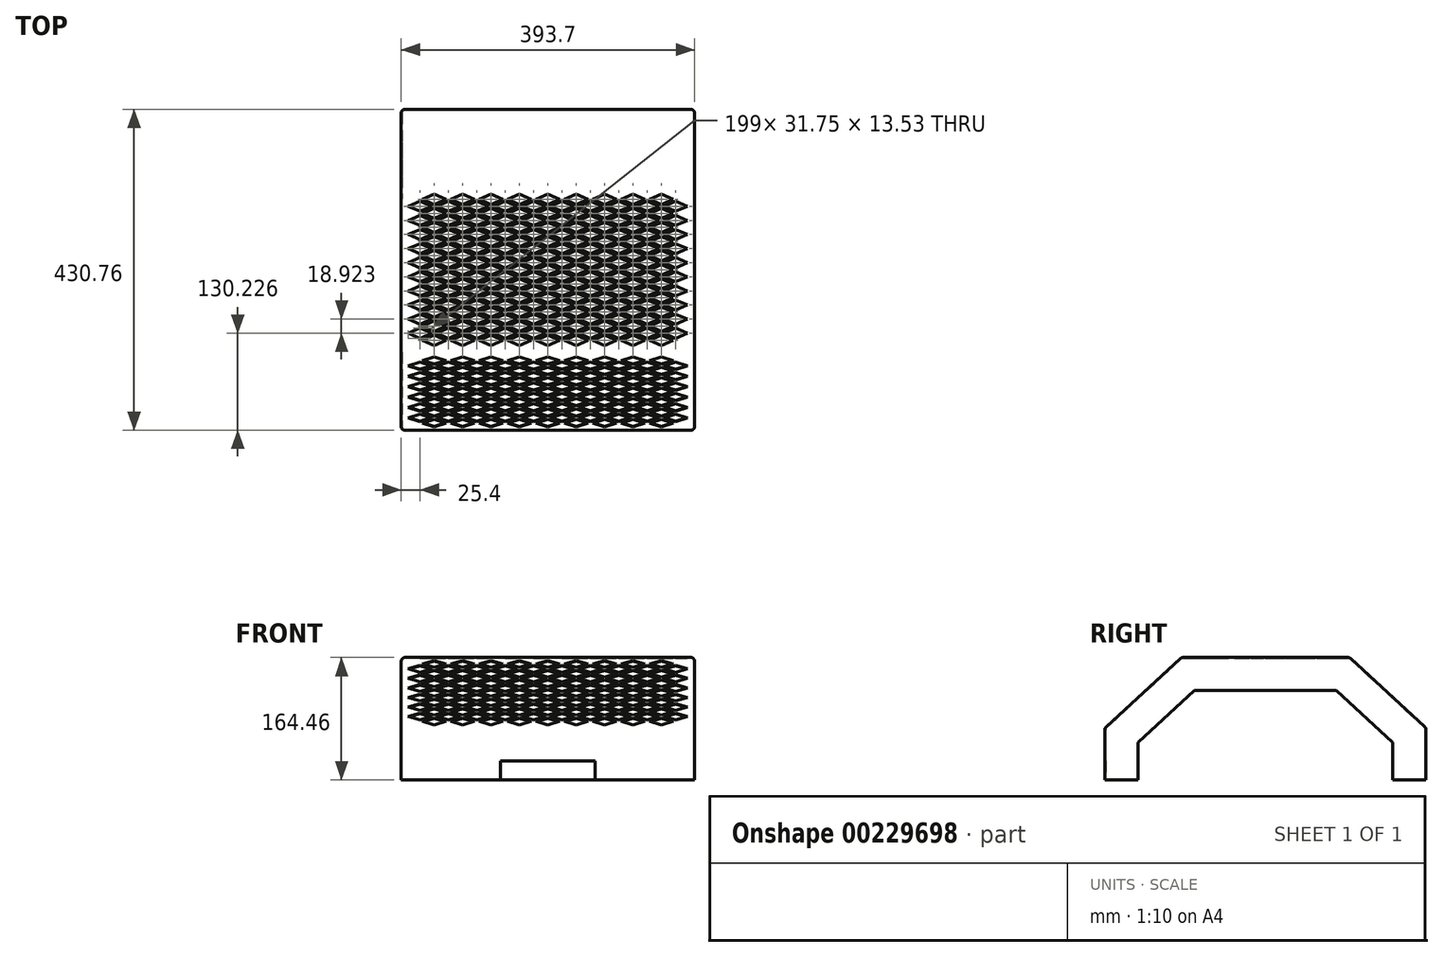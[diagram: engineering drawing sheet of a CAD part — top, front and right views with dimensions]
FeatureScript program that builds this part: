
annotation { "Feature Type Name" : "Feature", "Feature Type Description" : "" }
export const myFeature = defineFeature(function(context is Context, id is Id, definition is map)
    precondition{}
    {
        {
            var Q0;
            Q0=qCreatedBy(makeId("Right.planeOp"),FACE);
            var sketch = newSketch(context, id + "F0", { "sketchPlane" : qUnion([Q0])});
            skLineSegment(sketch, "E0", {"start": v(0, 0) * mm, "end": v(0, 169.27) * mm, "construction": true});
            skLineSegment(sketch, "E1", {"start": v(0, 164.46) * mm, "end": v(112.6, 164.46) * mm});
            skLineSegment(sketch, "E2", {"start": v(112.6, 164.46) * mm, "end": v(215.38, 69.85) * mm});
            skLineSegment(sketch, "E3", {"start": v(215.38, 69.85) * mm, "end": v(215.38, 0) * mm});
            skLineSegment(sketch, "E4", {"start": v(215.38, 0) * mm, "end": v(170.93, 0) * mm});
            skLineSegment(sketch, "E5", {"start": v(170.93, 0) * mm, "end": v(170.93, 50.35) * mm});
            skLineSegment(sketch, "E6", {"start": v(170.93, 50.35) * mm, "end": v(95.25, 120.01) * mm});
            skLineSegment(sketch, "E7", {"start": v(95.25, 120.01) * mm, "end": v(0, 120.01) * mm});
            skLineSegment(sketch, "E8.MirrorCS", {"start": v(0, 164.46) * mm, "end": v(-112.6, 164.46) * mm});
            skLineSegment(sketch, "E9.MirrorCS", {"start": v(-215.38, 0) * mm, "end": v(-170.93, 0) * mm});
            skLineSegment(sketch, "E10.MirrorCS", {"start": v(-170.93, 0) * mm, "end": v(-170.93, 50.35) * mm});
            skLineSegment(sketch, "E11.MirrorCS", {"start": v(-215.38, 69.85) * mm, "end": v(-215.38, 0) * mm});
            skLineSegment(sketch, "E12.MirrorCS", {"start": v(-95.25, 120.01) * mm, "end": v(0, 120.01) * mm});
            skLineSegment(sketch, "E13.MirrorCS", {"start": v(-112.6, 164.46) * mm, "end": v(-215.38, 69.85) * mm});
            skLineSegment(sketch, "E14.MirrorCS", {"start": v(-170.93, 50.35) * mm, "end": v(-95.25, 120.01) * mm});
            skSolve(sketch);
        }
        {
            var Q0;
            Q0 = qSketchRegion(id + "F0", true);
            extrude(context, id + "F1", {"entities" : qUnion([Q0]), "endBound" : BoundingType.SYMMETRIC, "depth" : 393.7 * mm});
        }
        {
            var Q0;
            Q0=makeQuery(id+"F1.opExtrude","CAP_EDGE",EDGE,{"disambiguationData":[OSD([sQuery(id+"F0.wireOp",EDGE,"E1"),sQuery(id+"F0.wireOp",EDGE,"E8.MirrorCS")])],"isStart":true});
            var Q1;
            Q1=makeQuery(id+"F1.opExtrude","CAP_EDGE",EDGE,{"disambiguationData":[OSD([sQuery(id+"F0.wireOp",EDGE,"E1"),sQuery(id+"F0.wireOp",EDGE,"E8.MirrorCS")])],"isStart":false});
            var Q2;
            Q2=makeQuery(id+"F1.opExtrude","CAP_EDGE",EDGE,{"disambiguationData":[OSD([sQuery(id+"F0.wireOp",EDGE,"E13.MirrorCS")])],"isStart":false});
            var Q3;
            Q3=makeQuery(id+"F1.opExtrude","CAP_EDGE",EDGE,{"disambiguationData":[OSD([sQuery(id+"F0.wireOp",EDGE,"E11.MirrorCS")])],"isStart":false});
            var Q4;
            Q4=makeQuery(id+"F1.opExtrude","CAP_EDGE",EDGE,{"disambiguationData":[OSD([sQuery(id+"F0.wireOp",EDGE,"E2")])],"isStart":false});
            var Q5;
            Q5=makeQuery(id+"F1.opExtrude","CAP_EDGE",EDGE,{"disambiguationData":[OSD([sQuery(id+"F0.wireOp",EDGE,"E3")])],"isStart":false});
            var Q6;
            Q6=makeQuery(id+"F1.opExtrude","CAP_EDGE",EDGE,{"disambiguationData":[OSD([sQuery(id+"F0.wireOp",EDGE,"E3")])],"isStart":true});
            var Q7;
            Q7=makeQuery(id+"F1.opExtrude","CAP_EDGE",EDGE,{"disambiguationData":[OSD([sQuery(id+"F0.wireOp",EDGE,"E2")])],"isStart":true});
            var Q8;
            Q8=makeQuery(id+"F1.opExtrude","CAP_EDGE",EDGE,{"disambiguationData":[OSD([sQuery(id+"F0.wireOp",EDGE,"E13.MirrorCS")])],"isStart":true});
            var Q9;
            Q9=makeQuery(id+"F1.opExtrude","CAP_EDGE",EDGE,{"disambiguationData":[OSD([sQuery(id+"F0.wireOp",EDGE,"E11.MirrorCS")])],"isStart":true});
            var Q10;
            Q10=makeQuery(id+"F1.opExtrude","SWEPT_EDGE",EDGE,{"disambiguationData":[OSD([sQuery(id+"F0.wireOp",EDGE,"E11.MirrorCS"),sQuery(id+"F0.wireOp",EDGE,"E13.MirrorCS")])]});
            var Q11;
            Q11=makeQuery(id+"F1.opExtrude","SWEPT_EDGE",EDGE,{"disambiguationData":[OSD([sQuery(id+"F0.wireOp",EDGE,"E8.MirrorCS"),sQuery(id+"F0.wireOp",EDGE,"E13.MirrorCS")])]});
            var Q12;
            Q12=makeQuery(id+"F1.opExtrude","SWEPT_EDGE",EDGE,{"disambiguationData":[OSD([sQuery(id+"F0.wireOp",EDGE,"E1"),sQuery(id+"F0.wireOp",EDGE,"E2")])]});
            var Q13;
            Q13=makeQuery(id+"F1.opExtrude","SWEPT_EDGE",EDGE,{"disambiguationData":[OSD([sQuery(id+"F0.wireOp",EDGE,"E2"),sQuery(id+"F0.wireOp",EDGE,"E3")])]});
            fillet(context, id + "F2", {"entities" : qUnion([Q0, Q1, Q2, Q3, Q4, Q5, Q6, Q7, Q8, Q9, Q10, Q11, Q12, Q13]), "radius" : 5.08 * mm, "tangentPropagation" : true, "allowEdgeOverflow" : false});
        }
        {
            var Q0;
            Q0=makeQuery(id+"F1.opExtrude","SWEPT_FACE",FACE,{"disambiguationData":[OSD([sQuery(id+"F0.wireOp",EDGE,"E7"),sQuery(id+"F0.wireOp",EDGE,"E12.MirrorCS")])]});
            var Q1;
            Q1=makeQuery(id+"F1.opExtrude","SWEPT_FACE",FACE,{"disambiguationData":[OSD([sQuery(id+"F0.wireOp",EDGE,"E6")])]});
            var Q2;
            Q2=makeQuery(id+"F1.opExtrude","SWEPT_FACE",FACE,{"disambiguationData":[OSD([sQuery(id+"F0.wireOp",EDGE,"E5")])]});
            var Q3;
            Q3=makeQuery(id+"F1.opExtrude","SWEPT_FACE",FACE,{"disambiguationData":[OSD([sQuery(id+"F0.wireOp",EDGE,"E4")])]});
            var Q4;
            Q4=makeQuery(id+"F1.opExtrude","SWEPT_FACE",FACE,{"disambiguationData":[OSD([sQuery(id+"F0.wireOp",EDGE,"E14.MirrorCS")])]});
            var Q5;
            Q5=makeQuery(id+"F1.opExtrude","SWEPT_FACE",FACE,{"disambiguationData":[OSD([sQuery(id+"F0.wireOp",EDGE,"E10.MirrorCS")])]});
            var Q6;
            Q6=makeQuery(id+"F1.opExtrude","SWEPT_FACE",FACE,{"disambiguationData":[OSD([sQuery(id+"F0.wireOp",EDGE,"E9.MirrorCS")])]});
            shell(context, id + "F3", {"entities" : qUnion([Q0, Q1, Q2, Q3, Q4, Q5, Q6]), "thickness" : 0.95 * mm});
        }
        {
            var Q0;
            Q0=makeQuery(id+"F1.opExtrude","SWEPT_FACE",FACE,{"disambiguationData":[OSD([sQuery(id+"F0.wireOp",EDGE,"E11.MirrorCS")])]});
            var sketch = newSketch(context, id + "F4", { "sketchPlane" : qUnion([Q0])});
            skLineSegment(sketch, "E15.bottom", {"start": v(-63.5, 0) * mm, "end": v(63.5, 0) * mm});
            skLineSegment(sketch, "E15.top", {"start": v(-63.5, 25.4) * mm, "end": v(63.5, 25.4) * mm});
            skLineSegment(sketch, "E15.left", {"start": v(-63.5, 0) * mm, "end": v(-63.5, 25.4) * mm});
            skLineSegment(sketch, "E15.right", {"start": v(63.5, 0) * mm, "end": v(63.5, 25.4) * mm});
            skSolve(sketch);
        }
        {
            var Q0;
            Q0 = qSketchRegion(id + "F4", true);
            extrude(context, id + "F5", {"entities" : qUnion([Q0]), "operationType" : NewBodyOperationType.REMOVE, "oppositeDirection" : true, "depth" : 25.4 * mm});
        }
        {
            var Q0;
            Q0=makeQuery(id+"F1.opExtrude","SWEPT_FACE",FACE,{"disambiguationData":[OSD([sQuery(id+"F0.wireOp",EDGE,"E1"),sQuery(id+"F0.wireOp",EDGE,"E8.MirrorCS")])]});
            var sketch = newSketch(context, id + "F6", { "sketchPlane" : qUnion([Q0])});
            skLineSegment(sketch, "E16", {"start": v(-15.88, 0) * mm, "end": v(0, 6.76) * mm});
            skLineSegment(sketch, "E17", {"start": v(0, 6.76) * mm, "end": v(15.88, 0) * mm});
            skLineSegment(sketch, "E18", {"start": v(15.88, 0) * mm, "end": v(0, -6.76) * mm});
            skLineSegment(sketch, "E19", {"start": v(0, -6.76) * mm, "end": v(-15.88, 0) * mm});
            skLineSegment(sketch, "E20.0.1.0", {"start": v(-15.88, 18.92) * mm, "end": v(0, 25.69) * mm});
            skLineSegment(sketch, "E20.0.1.1", {"start": v(15.88, 18.92) * mm, "end": v(0, 12.16) * mm});
            skLineSegment(sketch, "E20.0.1.2", {"start": v(0, 12.16) * mm, "end": v(-15.88, 18.92) * mm});
            skLineSegment(sketch, "E20.0.1.3", {"start": v(0, 25.69) * mm, "end": v(15.88, 18.92) * mm});
            skLineSegment(sketch, "E20.0.2.0", {"start": v(-15.88, 37.85) * mm, "end": v(0, 44.6) * mm});
            skLineSegment(sketch, "E20.0.2.1", {"start": v(15.88, 37.85) * mm, "end": v(0, 31.08) * mm});
            skLineSegment(sketch, "E20.0.2.2", {"start": v(0, 31.08) * mm, "end": v(-15.88, 37.85) * mm});
            skLineSegment(sketch, "E20.0.2.3", {"start": v(0, 44.6) * mm, "end": v(15.88, 37.85) * mm});
            skLineSegment(sketch, "E20.0.3.0", {"start": v(-15.88, 56.77) * mm, "end": v(0, 63.53) * mm});
            skLineSegment(sketch, "E20.0.3.1", {"start": v(15.88, 56.77) * mm, "end": v(0, 50) * mm});
            skLineSegment(sketch, "E20.0.3.2", {"start": v(0, 50) * mm, "end": v(-15.88, 56.77) * mm});
            skLineSegment(sketch, "E20.0.3.3", {"start": v(0, 63.53) * mm, "end": v(15.88, 56.77) * mm});
            skLineSegment(sketch, "E20.0.4.0", {"start": v(-15.88, 75.7) * mm, "end": v(0, 82.45) * mm});
            skLineSegment(sketch, "E20.0.4.1", {"start": v(15.88, 75.7) * mm, "end": v(0, 68.93) * mm});
            skLineSegment(sketch, "E20.0.4.2", {"start": v(0, 68.93) * mm, "end": v(-15.88, 75.7) * mm});
            skLineSegment(sketch, "E20.0.4.3", {"start": v(0, 82.45) * mm, "end": v(15.88, 75.7) * mm});
            skLineSegment(sketch, "E20.0.5.0", {"start": v(-15.88, 94.62) * mm, "end": v(0, 101.38) * mm});
            skLineSegment(sketch, "E20.0.5.1", {"start": v(15.88, 94.62) * mm, "end": v(0, 87.85) * mm});
            skLineSegment(sketch, "E20.0.5.2", {"start": v(0, 87.85) * mm, "end": v(-15.88, 94.62) * mm});
            skLineSegment(sketch, "E20.0.5.3", {"start": v(0, 101.38) * mm, "end": v(15.88, 94.62) * mm});
            skLineSegment(sketch, "E20.1.0.0", {"start": v(22.23, 0) * mm, "end": v(38.1, 6.76) * mm});
            skLineSegment(sketch, "E20.1.0.1", {"start": v(53.98, 0) * mm, "end": v(38.1, -6.76) * mm});
            skLineSegment(sketch, "E20.1.0.2", {"start": v(38.1, -6.76) * mm, "end": v(22.22, 0) * mm});
            skLineSegment(sketch, "E20.1.0.3", {"start": v(38.1, 6.76) * mm, "end": v(53.98, 0) * mm});
            skLineSegment(sketch, "E20.1.1.0", {"start": v(22.23, 18.92) * mm, "end": v(38.1, 25.69) * mm});
            skLineSegment(sketch, "E20.1.1.1", {"start": v(53.98, 18.92) * mm, "end": v(38.1, 12.16) * mm});
            skLineSegment(sketch, "E20.1.1.2", {"start": v(38.1, 12.16) * mm, "end": v(22.22, 18.92) * mm});
            skLineSegment(sketch, "E20.1.1.3", {"start": v(38.1, 25.69) * mm, "end": v(53.98, 18.92) * mm});
            skLineSegment(sketch, "E20.1.2.0", {"start": v(22.23, 37.85) * mm, "end": v(38.1, 44.6) * mm});
            skLineSegment(sketch, "E20.1.2.1", {"start": v(53.98, 37.85) * mm, "end": v(38.1, 31.08) * mm});
            skLineSegment(sketch, "E20.1.2.2", {"start": v(38.1, 31.08) * mm, "end": v(22.22, 37.85) * mm});
            skLineSegment(sketch, "E20.1.2.3", {"start": v(38.1, 44.6) * mm, "end": v(53.98, 37.85) * mm});
            skLineSegment(sketch, "E20.1.3.0", {"start": v(22.23, 56.77) * mm, "end": v(38.1, 63.53) * mm});
            skLineSegment(sketch, "E20.1.3.1", {"start": v(53.98, 56.77) * mm, "end": v(38.1, 50) * mm});
            skLineSegment(sketch, "E20.1.3.2", {"start": v(38.1, 50) * mm, "end": v(22.22, 56.77) * mm});
            skLineSegment(sketch, "E20.1.3.3", {"start": v(38.1, 63.53) * mm, "end": v(53.98, 56.77) * mm});
            skLineSegment(sketch, "E20.1.4.0", {"start": v(22.23, 75.7) * mm, "end": v(38.1, 82.45) * mm});
            skLineSegment(sketch, "E20.1.4.1", {"start": v(53.98, 75.7) * mm, "end": v(38.1, 68.93) * mm});
            skLineSegment(sketch, "E20.1.4.2", {"start": v(38.1, 68.93) * mm, "end": v(22.22, 75.7) * mm});
            skLineSegment(sketch, "E20.1.4.3", {"start": v(38.1, 82.45) * mm, "end": v(53.98, 75.7) * mm});
            skLineSegment(sketch, "E20.1.5.0", {"start": v(22.23, 94.62) * mm, "end": v(38.1, 101.38) * mm});
            skLineSegment(sketch, "E20.1.5.1", {"start": v(53.98, 94.62) * mm, "end": v(38.1, 87.85) * mm});
            skLineSegment(sketch, "E20.1.5.2", {"start": v(38.1, 87.85) * mm, "end": v(22.22, 94.62) * mm});
            skLineSegment(sketch, "E20.1.5.3", {"start": v(38.1, 101.38) * mm, "end": v(53.98, 94.62) * mm});
            skLineSegment(sketch, "E20.2.0.0", {"start": v(60.33, 0) * mm, "end": v(76.2, 6.76) * mm});
            skLineSegment(sketch, "E20.2.0.1", {"start": v(92.08, 0) * mm, "end": v(76.2, -6.76) * mm});
            skLineSegment(sketch, "E20.2.0.2", {"start": v(76.2, -6.76) * mm, "end": v(60.33, 0) * mm});
            skLineSegment(sketch, "E20.2.0.3", {"start": v(76.2, 6.76) * mm, "end": v(92.08, 0) * mm});
            skLineSegment(sketch, "E20.2.1.0", {"start": v(60.33, 18.92) * mm, "end": v(76.2, 25.69) * mm});
            skLineSegment(sketch, "E20.2.1.1", {"start": v(92.08, 18.92) * mm, "end": v(76.2, 12.16) * mm});
            skLineSegment(sketch, "E20.2.1.2", {"start": v(76.2, 12.16) * mm, "end": v(60.33, 18.92) * mm});
            skLineSegment(sketch, "E20.2.1.3", {"start": v(76.2, 25.69) * mm, "end": v(92.08, 18.92) * mm});
            skLineSegment(sketch, "E20.2.2.0", {"start": v(60.33, 37.85) * mm, "end": v(76.2, 44.6) * mm});
            skLineSegment(sketch, "E20.2.2.1", {"start": v(92.08, 37.85) * mm, "end": v(76.2, 31.08) * mm});
            skLineSegment(sketch, "E20.2.2.2", {"start": v(76.2, 31.08) * mm, "end": v(60.33, 37.85) * mm});
            skLineSegment(sketch, "E20.2.2.3", {"start": v(76.2, 44.6) * mm, "end": v(92.08, 37.85) * mm});
            skLineSegment(sketch, "E20.2.3.0", {"start": v(60.33, 56.77) * mm, "end": v(76.2, 63.53) * mm});
            skLineSegment(sketch, "E20.2.3.1", {"start": v(92.08, 56.77) * mm, "end": v(76.2, 50) * mm});
            skLineSegment(sketch, "E20.2.3.2", {"start": v(76.2, 50) * mm, "end": v(60.33, 56.77) * mm});
            skLineSegment(sketch, "E20.2.3.3", {"start": v(76.2, 63.53) * mm, "end": v(92.08, 56.77) * mm});
            skLineSegment(sketch, "E20.2.4.0", {"start": v(60.33, 75.7) * mm, "end": v(76.2, 82.45) * mm});
            skLineSegment(sketch, "E20.2.4.1", {"start": v(92.08, 75.7) * mm, "end": v(76.2, 68.93) * mm});
            skLineSegment(sketch, "E20.2.4.2", {"start": v(76.2, 68.93) * mm, "end": v(60.33, 75.7) * mm});
            skLineSegment(sketch, "E20.2.4.3", {"start": v(76.2, 82.45) * mm, "end": v(92.08, 75.7) * mm});
            skLineSegment(sketch, "E20.2.5.0", {"start": v(60.33, 94.62) * mm, "end": v(76.2, 101.38) * mm});
            skLineSegment(sketch, "E20.2.5.1", {"start": v(92.08, 94.62) * mm, "end": v(76.2, 87.85) * mm});
            skLineSegment(sketch, "E20.2.5.2", {"start": v(76.2, 87.85) * mm, "end": v(60.33, 94.62) * mm});
            skLineSegment(sketch, "E20.2.5.3", {"start": v(76.2, 101.38) * mm, "end": v(92.08, 94.62) * mm});
            skLineSegment(sketch, "E20.3.0.0", {"start": v(98.43, 0) * mm, "end": v(114.3, 6.76) * mm});
            skLineSegment(sketch, "E20.3.0.1", {"start": v(130.18, 0) * mm, "end": v(114.3, -6.76) * mm});
            skLineSegment(sketch, "E20.3.0.2", {"start": v(114.3, -6.76) * mm, "end": v(98.43, 0) * mm});
            skLineSegment(sketch, "E20.3.0.3", {"start": v(114.3, 6.76) * mm, "end": v(130.18, 0) * mm});
            skLineSegment(sketch, "E20.3.1.0", {"start": v(98.43, 18.92) * mm, "end": v(114.3, 25.69) * mm});
            skLineSegment(sketch, "E20.3.1.1", {"start": v(130.18, 18.92) * mm, "end": v(114.3, 12.16) * mm});
            skLineSegment(sketch, "E20.3.1.2", {"start": v(114.3, 12.16) * mm, "end": v(98.43, 18.92) * mm});
            skLineSegment(sketch, "E20.3.1.3", {"start": v(114.3, 25.69) * mm, "end": v(130.18, 18.92) * mm});
            skLineSegment(sketch, "E20.3.2.0", {"start": v(98.43, 37.85) * mm, "end": v(114.3, 44.6) * mm});
            skLineSegment(sketch, "E20.3.2.1", {"start": v(130.18, 37.85) * mm, "end": v(114.3, 31.08) * mm});
            skLineSegment(sketch, "E20.3.2.2", {"start": v(114.3, 31.08) * mm, "end": v(98.43, 37.85) * mm});
            skLineSegment(sketch, "E20.3.2.3", {"start": v(114.3, 44.6) * mm, "end": v(130.18, 37.85) * mm});
            skLineSegment(sketch, "E20.3.3.0", {"start": v(98.43, 56.77) * mm, "end": v(114.3, 63.53) * mm});
            skLineSegment(sketch, "E20.3.3.1", {"start": v(130.18, 56.77) * mm, "end": v(114.3, 50) * mm});
            skLineSegment(sketch, "E20.3.3.2", {"start": v(114.3, 50) * mm, "end": v(98.43, 56.77) * mm});
            skLineSegment(sketch, "E20.3.3.3", {"start": v(114.3, 63.53) * mm, "end": v(130.18, 56.77) * mm});
            skLineSegment(sketch, "E20.3.4.0", {"start": v(98.43, 75.7) * mm, "end": v(114.3, 82.45) * mm});
            skLineSegment(sketch, "E20.3.4.1", {"start": v(130.18, 75.7) * mm, "end": v(114.3, 68.93) * mm});
            skLineSegment(sketch, "E20.3.4.2", {"start": v(114.3, 68.93) * mm, "end": v(98.43, 75.7) * mm});
            skLineSegment(sketch, "E20.3.4.3", {"start": v(114.3, 82.45) * mm, "end": v(130.18, 75.7) * mm});
            skLineSegment(sketch, "E20.3.5.0", {"start": v(98.43, 94.62) * mm, "end": v(114.3, 101.38) * mm});
            skLineSegment(sketch, "E20.3.5.1", {"start": v(130.18, 94.62) * mm, "end": v(114.3, 87.85) * mm});
            skLineSegment(sketch, "E20.3.5.2", {"start": v(114.3, 87.85) * mm, "end": v(98.43, 94.62) * mm});
            skLineSegment(sketch, "E20.3.5.3", {"start": v(114.3, 101.38) * mm, "end": v(130.18, 94.62) * mm});
            skLineSegment(sketch, "E20.4.0.0", {"start": v(136.53, 0) * mm, "end": v(152.4, 6.76) * mm});
            skLineSegment(sketch, "E20.4.0.1", {"start": v(168.28, 0) * mm, "end": v(152.4, -6.76) * mm});
            skLineSegment(sketch, "E20.4.0.2", {"start": v(152.4, -6.76) * mm, "end": v(136.53, 0) * mm});
            skLineSegment(sketch, "E20.4.0.3", {"start": v(152.4, 6.76) * mm, "end": v(168.28, 0) * mm});
            skLineSegment(sketch, "E20.4.1.0", {"start": v(136.53, 18.92) * mm, "end": v(152.4, 25.69) * mm});
            skLineSegment(sketch, "E20.4.1.1", {"start": v(168.28, 18.92) * mm, "end": v(152.4, 12.16) * mm});
            skLineSegment(sketch, "E20.4.1.2", {"start": v(152.4, 12.16) * mm, "end": v(136.53, 18.92) * mm});
            skLineSegment(sketch, "E20.4.1.3", {"start": v(152.4, 25.69) * mm, "end": v(168.28, 18.92) * mm});
            skLineSegment(sketch, "E20.4.2.0", {"start": v(136.53, 37.85) * mm, "end": v(152.4, 44.6) * mm});
            skLineSegment(sketch, "E20.4.2.1", {"start": v(168.28, 37.85) * mm, "end": v(152.4, 31.08) * mm});
            skLineSegment(sketch, "E20.4.2.2", {"start": v(152.4, 31.08) * mm, "end": v(136.53, 37.85) * mm});
            skLineSegment(sketch, "E20.4.2.3", {"start": v(152.4, 44.6) * mm, "end": v(168.28, 37.85) * mm});
            skLineSegment(sketch, "E20.4.3.0", {"start": v(136.53, 56.77) * mm, "end": v(152.4, 63.53) * mm});
            skLineSegment(sketch, "E20.4.3.1", {"start": v(168.28, 56.77) * mm, "end": v(152.4, 50) * mm});
            skLineSegment(sketch, "E20.4.3.2", {"start": v(152.4, 50) * mm, "end": v(136.53, 56.77) * mm});
            skLineSegment(sketch, "E20.4.3.3", {"start": v(152.4, 63.53) * mm, "end": v(168.28, 56.77) * mm});
            skLineSegment(sketch, "E20.4.4.0", {"start": v(136.53, 75.7) * mm, "end": v(152.4, 82.45) * mm});
            skLineSegment(sketch, "E20.4.4.1", {"start": v(168.28, 75.7) * mm, "end": v(152.4, 68.93) * mm});
            skLineSegment(sketch, "E20.4.4.2", {"start": v(152.4, 68.93) * mm, "end": v(136.53, 75.7) * mm});
            skLineSegment(sketch, "E20.4.4.3", {"start": v(152.4, 82.45) * mm, "end": v(168.28, 75.7) * mm});
            skLineSegment(sketch, "E20.4.5.0", {"start": v(136.53, 94.62) * mm, "end": v(152.4, 101.38) * mm});
            skLineSegment(sketch, "E20.4.5.1", {"start": v(168.28, 94.62) * mm, "end": v(152.4, 87.85) * mm});
            skLineSegment(sketch, "E20.4.5.2", {"start": v(152.4, 87.85) * mm, "end": v(136.53, 94.62) * mm});
            skLineSegment(sketch, "E20.4.5.3", {"start": v(152.4, 101.38) * mm, "end": v(168.28, 94.62) * mm});
            skLineSegment(sketch, "E20.direction1", {"start": v(-15.88, 0) * mm, "end": v(22.22, 0) * mm, "construction": true});
            skLineSegment(sketch, "E20.direction2", {"start": v(-15.88, 0) * mm, "end": v(-15.88, 18.92) * mm, "construction": true});
            skLineSegment(sketch, "E21.0.1.0", {"start": v(0, -25.69) * mm, "end": v(-15.88, -18.92) * mm});
            skLineSegment(sketch, "E21.0.1.1", {"start": v(15.88, -18.92) * mm, "end": v(0, -25.69) * mm});
            skLineSegment(sketch, "E21.0.1.2", {"start": v(0, -12.16) * mm, "end": v(15.88, -18.92) * mm});
            skLineSegment(sketch, "E21.0.1.3", {"start": v(-15.88, -18.92) * mm, "end": v(0, -12.16) * mm});
            skLineSegment(sketch, "E21.0.1.4", {"start": v(114.3, -12.16) * mm, "end": v(130.18, -18.92) * mm});
            skLineSegment(sketch, "E21.0.1.5", {"start": v(38.1, -12.16) * mm, "end": v(53.98, -18.92) * mm});
            skLineSegment(sketch, "E21.0.1.6", {"start": v(152.4, -12.16) * mm, "end": v(168.28, -18.92) * mm});
            skLineSegment(sketch, "E21.0.1.7", {"start": v(76.2, -12.16) * mm, "end": v(92.08, -18.92) * mm});
            skLineSegment(sketch, "E21.0.1.8", {"start": v(114.3, -25.69) * mm, "end": v(98.43, -18.92) * mm});
            skLineSegment(sketch, "E21.0.1.9", {"start": v(38.1, -25.69) * mm, "end": v(22.22, -18.92) * mm});
            skLineSegment(sketch, "E21.0.1.10", {"start": v(76.2, -25.69) * mm, "end": v(60.33, -18.92) * mm});
            skLineSegment(sketch, "E21.0.1.11", {"start": v(130.18, -18.92) * mm, "end": v(114.3, -25.69) * mm});
            skLineSegment(sketch, "E21.0.1.12", {"start": v(53.98, -18.92) * mm, "end": v(38.1, -25.69) * mm});
            skLineSegment(sketch, "E21.0.1.13", {"start": v(152.4, -25.69) * mm, "end": v(136.53, -18.92) * mm});
            skLineSegment(sketch, "E21.0.1.14", {"start": v(98.43, -18.92) * mm, "end": v(114.3, -12.16) * mm});
            skLineSegment(sketch, "E21.0.1.15", {"start": v(-15.88, -18.92) * mm, "end": v(22.22, -18.92) * mm, "construction": true});
            skLineSegment(sketch, "E21.0.1.16", {"start": v(22.23, -18.92) * mm, "end": v(38.1, -12.16) * mm});
            skLineSegment(sketch, "E21.0.1.17", {"start": v(168.28, -18.92) * mm, "end": v(152.4, -25.69) * mm});
            skLineSegment(sketch, "E21.0.1.18", {"start": v(92.08, -18.92) * mm, "end": v(76.2, -25.69) * mm});
            skLineSegment(sketch, "E21.0.1.19", {"start": v(136.53, -18.92) * mm, "end": v(152.4, -12.16) * mm});
            skLineSegment(sketch, "E21.0.1.20", {"start": v(60.33, -18.92) * mm, "end": v(76.2, -12.16) * mm});
            skLineSegment(sketch, "E21.0.2.0", {"start": v(0, -44.6) * mm, "end": v(-15.88, -37.85) * mm});
            skLineSegment(sketch, "E21.0.2.1", {"start": v(15.88, -37.85) * mm, "end": v(0, -44.6) * mm});
            skLineSegment(sketch, "E21.0.2.2", {"start": v(0, -31.08) * mm, "end": v(15.88, -37.85) * mm});
            skLineSegment(sketch, "E21.0.2.3", {"start": v(-15.88, -37.85) * mm, "end": v(0, -31.08) * mm});
            skLineSegment(sketch, "E21.0.2.4", {"start": v(114.3, -31.08) * mm, "end": v(130.18, -37.85) * mm});
            skLineSegment(sketch, "E21.0.2.5", {"start": v(38.1, -31.08) * mm, "end": v(53.98, -37.85) * mm});
            skLineSegment(sketch, "E21.0.2.6", {"start": v(152.4, -31.08) * mm, "end": v(168.28, -37.85) * mm});
            skLineSegment(sketch, "E21.0.2.7", {"start": v(76.2, -31.08) * mm, "end": v(92.08, -37.85) * mm});
            skLineSegment(sketch, "E21.0.2.8", {"start": v(114.3, -44.6) * mm, "end": v(98.43, -37.85) * mm});
            skLineSegment(sketch, "E21.0.2.9", {"start": v(38.1, -44.6) * mm, "end": v(22.22, -37.85) * mm});
            skLineSegment(sketch, "E21.0.2.10", {"start": v(76.2, -44.6) * mm, "end": v(60.33, -37.85) * mm});
            skLineSegment(sketch, "E21.0.2.11", {"start": v(130.18, -37.85) * mm, "end": v(114.3, -44.6) * mm});
            skLineSegment(sketch, "E21.0.2.12", {"start": v(53.98, -37.85) * mm, "end": v(38.1, -44.6) * mm});
            skLineSegment(sketch, "E21.0.2.13", {"start": v(152.4, -44.6) * mm, "end": v(136.53, -37.85) * mm});
            skLineSegment(sketch, "E21.0.2.14", {"start": v(98.43, -37.85) * mm, "end": v(114.3, -31.08) * mm});
            skLineSegment(sketch, "E21.0.2.15", {"start": v(-15.88, -37.85) * mm, "end": v(22.22, -37.85) * mm, "construction": true});
            skLineSegment(sketch, "E21.0.2.16", {"start": v(22.23, -37.85) * mm, "end": v(38.1, -31.08) * mm});
            skLineSegment(sketch, "E21.0.2.17", {"start": v(168.28, -37.85) * mm, "end": v(152.4, -44.6) * mm});
            skLineSegment(sketch, "E21.0.2.18", {"start": v(92.08, -37.85) * mm, "end": v(76.2, -44.6) * mm});
            skLineSegment(sketch, "E21.0.2.19", {"start": v(136.53, -37.85) * mm, "end": v(152.4, -31.08) * mm});
            skLineSegment(sketch, "E21.0.2.20", {"start": v(60.33, -37.85) * mm, "end": v(76.2, -31.08) * mm});
            skLineSegment(sketch, "E21.0.3.0", {"start": v(0, -63.53) * mm, "end": v(-15.88, -56.77) * mm});
            skLineSegment(sketch, "E21.0.3.1", {"start": v(15.88, -56.77) * mm, "end": v(0, -63.53) * mm});
            skLineSegment(sketch, "E21.0.3.2", {"start": v(0, -50) * mm, "end": v(15.88, -56.77) * mm});
            skLineSegment(sketch, "E21.0.3.3", {"start": v(-15.88, -56.77) * mm, "end": v(0, -50) * mm});
            skLineSegment(sketch, "E21.0.3.4", {"start": v(114.3, -50) * mm, "end": v(130.18, -56.77) * mm});
            skLineSegment(sketch, "E21.0.3.5", {"start": v(38.1, -50) * mm, "end": v(53.98, -56.77) * mm});
            skLineSegment(sketch, "E21.0.3.6", {"start": v(152.4, -50) * mm, "end": v(168.28, -56.77) * mm});
            skLineSegment(sketch, "E21.0.3.7", {"start": v(76.2, -50) * mm, "end": v(92.08, -56.77) * mm});
            skLineSegment(sketch, "E21.0.3.8", {"start": v(114.3, -63.53) * mm, "end": v(98.43, -56.77) * mm});
            skLineSegment(sketch, "E21.0.3.9", {"start": v(38.1, -63.53) * mm, "end": v(22.22, -56.77) * mm});
            skLineSegment(sketch, "E21.0.3.10", {"start": v(76.2, -63.53) * mm, "end": v(60.33, -56.77) * mm});
            skLineSegment(sketch, "E21.0.3.11", {"start": v(130.18, -56.77) * mm, "end": v(114.3, -63.53) * mm});
            skLineSegment(sketch, "E21.0.3.12", {"start": v(53.98, -56.77) * mm, "end": v(38.1, -63.53) * mm});
            skLineSegment(sketch, "E21.0.3.13", {"start": v(152.4, -63.53) * mm, "end": v(136.53, -56.77) * mm});
            skLineSegment(sketch, "E21.0.3.14", {"start": v(98.43, -56.77) * mm, "end": v(114.3, -50) * mm});
            skLineSegment(sketch, "E21.0.3.15", {"start": v(-15.88, -56.77) * mm, "end": v(22.22, -56.77) * mm, "construction": true});
            skLineSegment(sketch, "E21.0.3.16", {"start": v(22.23, -56.77) * mm, "end": v(38.1, -50) * mm});
            skLineSegment(sketch, "E21.0.3.17", {"start": v(168.28, -56.77) * mm, "end": v(152.4, -63.53) * mm});
            skLineSegment(sketch, "E21.0.3.18", {"start": v(92.08, -56.77) * mm, "end": v(76.2, -63.53) * mm});
            skLineSegment(sketch, "E21.0.3.19", {"start": v(136.53, -56.77) * mm, "end": v(152.4, -50) * mm});
            skLineSegment(sketch, "E21.0.3.20", {"start": v(60.33, -56.77) * mm, "end": v(76.2, -50) * mm});
            skLineSegment(sketch, "E21.0.4.0", {"start": v(0, -82.45) * mm, "end": v(-15.88, -75.7) * mm});
            skLineSegment(sketch, "E21.0.4.1", {"start": v(15.88, -75.7) * mm, "end": v(0, -82.45) * mm});
            skLineSegment(sketch, "E21.0.4.2", {"start": v(0, -68.93) * mm, "end": v(15.88, -75.7) * mm});
            skLineSegment(sketch, "E21.0.4.3", {"start": v(-15.88, -75.7) * mm, "end": v(0, -68.93) * mm});
            skLineSegment(sketch, "E21.0.4.4", {"start": v(114.3, -68.93) * mm, "end": v(130.18, -75.7) * mm});
            skLineSegment(sketch, "E21.0.4.5", {"start": v(38.1, -68.93) * mm, "end": v(53.98, -75.7) * mm});
            skLineSegment(sketch, "E21.0.4.6", {"start": v(152.4, -68.93) * mm, "end": v(168.28, -75.7) * mm});
            skLineSegment(sketch, "E21.0.4.7", {"start": v(76.2, -68.93) * mm, "end": v(92.08, -75.7) * mm});
            skLineSegment(sketch, "E21.0.4.8", {"start": v(114.3, -82.45) * mm, "end": v(98.43, -75.7) * mm});
            skLineSegment(sketch, "E21.0.4.9", {"start": v(38.1, -82.45) * mm, "end": v(22.22, -75.7) * mm});
            skLineSegment(sketch, "E21.0.4.10", {"start": v(76.2, -82.45) * mm, "end": v(60.33, -75.7) * mm});
            skLineSegment(sketch, "E21.0.4.11", {"start": v(130.18, -75.7) * mm, "end": v(114.3, -82.45) * mm});
            skLineSegment(sketch, "E21.0.4.12", {"start": v(53.98, -75.7) * mm, "end": v(38.1, -82.45) * mm});
            skLineSegment(sketch, "E21.0.4.13", {"start": v(152.4, -82.45) * mm, "end": v(136.53, -75.7) * mm});
            skLineSegment(sketch, "E21.0.4.14", {"start": v(98.43, -75.7) * mm, "end": v(114.3, -68.93) * mm});
            skLineSegment(sketch, "E21.0.4.15", {"start": v(-15.88, -75.7) * mm, "end": v(22.22, -75.7) * mm, "construction": true});
            skLineSegment(sketch, "E21.0.4.16", {"start": v(22.23, -75.7) * mm, "end": v(38.1, -68.93) * mm});
            skLineSegment(sketch, "E21.0.4.17", {"start": v(168.28, -75.7) * mm, "end": v(152.4, -82.45) * mm});
            skLineSegment(sketch, "E21.0.4.18", {"start": v(92.08, -75.7) * mm, "end": v(76.2, -82.45) * mm});
            skLineSegment(sketch, "E21.0.4.19", {"start": v(136.53, -75.7) * mm, "end": v(152.4, -68.93) * mm});
            skLineSegment(sketch, "E21.0.4.20", {"start": v(60.33, -75.7) * mm, "end": v(76.2, -68.93) * mm});
            skLineSegment(sketch, "E21.0.5.0", {"start": v(0, -101.38) * mm, "end": v(-15.88, -94.61) * mm});
            skLineSegment(sketch, "E21.0.5.1", {"start": v(15.88, -94.62) * mm, "end": v(0, -101.38) * mm});
            skLineSegment(sketch, "E21.0.5.2", {"start": v(0, -87.85) * mm, "end": v(15.88, -94.62) * mm});
            skLineSegment(sketch, "E21.0.5.3", {"start": v(-15.88, -94.62) * mm, "end": v(0, -87.85) * mm});
            skLineSegment(sketch, "E21.0.5.4", {"start": v(114.3, -87.85) * mm, "end": v(130.18, -94.62) * mm});
            skLineSegment(sketch, "E21.0.5.5", {"start": v(38.1, -87.85) * mm, "end": v(53.98, -94.62) * mm});
            skLineSegment(sketch, "E21.0.5.6", {"start": v(152.4, -87.85) * mm, "end": v(168.28, -94.62) * mm});
            skLineSegment(sketch, "E21.0.5.7", {"start": v(76.2, -87.85) * mm, "end": v(92.08, -94.62) * mm});
            skLineSegment(sketch, "E21.0.5.8", {"start": v(114.3, -101.38) * mm, "end": v(98.43, -94.61) * mm});
            skLineSegment(sketch, "E21.0.5.9", {"start": v(38.1, -101.38) * mm, "end": v(22.22, -94.61) * mm});
            skLineSegment(sketch, "E21.0.5.10", {"start": v(76.2, -101.38) * mm, "end": v(60.33, -94.61) * mm});
            skLineSegment(sketch, "E21.0.5.11", {"start": v(130.18, -94.62) * mm, "end": v(114.3, -101.38) * mm});
            skLineSegment(sketch, "E21.0.5.12", {"start": v(53.98, -94.62) * mm, "end": v(38.1, -101.38) * mm});
            skLineSegment(sketch, "E21.0.5.13", {"start": v(152.4, -101.38) * mm, "end": v(136.53, -94.61) * mm});
            skLineSegment(sketch, "E21.0.5.14", {"start": v(98.43, -94.62) * mm, "end": v(114.3, -87.85) * mm});
            skLineSegment(sketch, "E21.0.5.15", {"start": v(-15.88, -94.62) * mm, "end": v(22.22, -94.62) * mm, "construction": true});
            skLineSegment(sketch, "E21.0.5.16", {"start": v(22.23, -94.62) * mm, "end": v(38.1, -87.85) * mm});
            skLineSegment(sketch, "E21.0.5.17", {"start": v(168.28, -94.62) * mm, "end": v(152.4, -101.38) * mm});
            skLineSegment(sketch, "E21.0.5.18", {"start": v(92.08, -94.62) * mm, "end": v(76.2, -101.38) * mm});
            skLineSegment(sketch, "E21.0.5.19", {"start": v(136.53, -94.62) * mm, "end": v(152.4, -87.85) * mm});
            skLineSegment(sketch, "E21.0.5.20", {"start": v(60.33, -94.62) * mm, "end": v(76.2, -87.85) * mm});
            skLineSegment(sketch, "E21.direction1", {"start": v(-15.88, 0) * mm, "end": v(9.52, 0) * mm, "construction": true});
            skLineSegment(sketch, "E21.direction2", {"start": v(-15.88, 0) * mm, "end": v(-15.88, -18.92) * mm, "construction": true});
            skLineSegment(sketch, "E22.1.0.0", {"start": v(-38.1, -50) * mm, "end": v(-22.23, -56.77) * mm});
            skLineSegment(sketch, "E22.1.0.1", {"start": v(-38.1, 87.85) * mm, "end": v(-53.98, 94.62) * mm});
            skLineSegment(sketch, "E22.1.0.2", {"start": v(-53.98, 56.77) * mm, "end": v(-38.1, 63.53) * mm});
            skLineSegment(sketch, "E22.1.0.3", {"start": v(-38.1, 44.6) * mm, "end": v(-22.23, 37.85) * mm});
            skLineSegment(sketch, "E22.1.0.4", {"start": v(-38.1, 31.08) * mm, "end": v(-53.98, 37.85) * mm});
            skLineSegment(sketch, "E22.1.0.5", {"start": v(-22.23, 37.85) * mm, "end": v(-38.1, 31.08) * mm});
            skLineSegment(sketch, "E22.1.0.6", {"start": v(-53.98, 37.85) * mm, "end": v(-38.1, 44.6) * mm});
            skLineSegment(sketch, "E22.1.0.7", {"start": v(-38.1, 25.69) * mm, "end": v(-22.23, 18.92) * mm});
            skLineSegment(sketch, "E22.1.0.8", {"start": v(-38.1, 12.16) * mm, "end": v(-53.98, 18.92) * mm});
            skLineSegment(sketch, "E22.1.0.9", {"start": v(-22.23, 18.92) * mm, "end": v(-38.1, 12.16) * mm});
            skLineSegment(sketch, "E22.1.0.10", {"start": v(-53.98, 18.92) * mm, "end": v(-38.1, 25.69) * mm});
            skLineSegment(sketch, "E22.1.0.11", {"start": v(-38.1, -6.76) * mm, "end": v(-53.98, 0) * mm});
            skLineSegment(sketch, "E22.1.0.12", {"start": v(-22.23, 0) * mm, "end": v(-38.1, -6.76) * mm});
            skLineSegment(sketch, "E22.1.0.13", {"start": v(-38.1, 6.76) * mm, "end": v(-22.23, 0) * mm});
            skLineSegment(sketch, "E22.1.0.14", {"start": v(-53.98, 0) * mm, "end": v(-38.1, 6.76) * mm});
            skLineSegment(sketch, "E22.1.0.15", {"start": v(-22.23, -56.77) * mm, "end": v(-38.1, -63.53) * mm});
            skLineSegment(sketch, "E22.1.0.16", {"start": v(-38.1, 63.53) * mm, "end": v(-22.23, 56.77) * mm});
            skLineSegment(sketch, "E22.1.0.17", {"start": v(-38.1, 50) * mm, "end": v(-53.98, 56.77) * mm});
            skLineSegment(sketch, "E22.1.0.18", {"start": v(-22.23, 56.77) * mm, "end": v(-38.1, 50) * mm});
            skLineSegment(sketch, "E22.1.0.19", {"start": v(-22.23, 94.62) * mm, "end": v(-38.1, 87.85) * mm});
            skLineSegment(sketch, "E22.1.0.20", {"start": v(-38.1, -63.53) * mm, "end": v(-53.98, -56.77) * mm});
            skLineSegment(sketch, "E22.1.0.21", {"start": v(-53.98, 94.62) * mm, "end": v(-38.1, 101.38) * mm});
            skLineSegment(sketch, "E22.1.0.22", {"start": v(-38.1, 82.45) * mm, "end": v(-22.23, 75.7) * mm});
            skLineSegment(sketch, "E22.1.0.23", {"start": v(-38.1, 68.93) * mm, "end": v(-53.98, 75.7) * mm});
            skLineSegment(sketch, "E22.1.0.24", {"start": v(-53.98, -37.85) * mm, "end": v(-38.1, -31.08) * mm});
            skLineSegment(sketch, "E22.1.0.25", {"start": v(-22.23, 75.7) * mm, "end": v(-38.1, 68.93) * mm});
            skLineSegment(sketch, "E22.1.0.26", {"start": v(-53.98, -94.62) * mm, "end": v(-38.1, -87.85) * mm});
            skLineSegment(sketch, "E22.1.0.27", {"start": v(-38.1, -31.08) * mm, "end": v(-22.23, -37.85) * mm});
            skLineSegment(sketch, "E22.1.0.28", {"start": v(-38.1, -87.85) * mm, "end": v(-22.23, -94.62) * mm});
            skLineSegment(sketch, "E22.1.0.29", {"start": v(-22.23, -37.85) * mm, "end": v(-38.1, -44.6) * mm});
            skLineSegment(sketch, "E22.1.0.30", {"start": v(-53.98, 75.7) * mm, "end": v(-38.1, 82.45) * mm});
            skLineSegment(sketch, "E22.1.0.31", {"start": v(-22.23, -94.62) * mm, "end": v(-38.1, -101.38) * mm});
            skLineSegment(sketch, "E22.1.0.32", {"start": v(-38.1, -44.6) * mm, "end": v(-53.98, -37.85) * mm});
            skLineSegment(sketch, "E22.1.0.33", {"start": v(-22.23, -75.7) * mm, "end": v(-38.1, -82.45) * mm});
            skLineSegment(sketch, "E22.1.0.34", {"start": v(-38.1, -25.69) * mm, "end": v(-53.98, -18.92) * mm});
            skLineSegment(sketch, "E22.1.0.35", {"start": v(-38.1, -101.38) * mm, "end": v(-53.98, -94.61) * mm});
            skLineSegment(sketch, "E22.1.0.36", {"start": v(-38.1, -82.45) * mm, "end": v(-53.98, -75.7) * mm});
            skLineSegment(sketch, "E22.1.0.37", {"start": v(-53.98, -75.7) * mm, "end": v(-38.1, -68.93) * mm});
            skLineSegment(sketch, "E22.1.0.38", {"start": v(-38.1, -12.16) * mm, "end": v(-22.23, -18.92) * mm});
            skLineSegment(sketch, "E22.1.0.39", {"start": v(-53.98, -18.92) * mm, "end": v(-38.1, -12.16) * mm});
            skLineSegment(sketch, "E22.1.0.40", {"start": v(-53.98, -56.77) * mm, "end": v(-38.1, -50) * mm});
            skLineSegment(sketch, "E22.1.0.41", {"start": v(-38.1, 101.38) * mm, "end": v(-22.23, 94.62) * mm});
            skLineSegment(sketch, "E22.1.0.42", {"start": v(-22.23, -18.92) * mm, "end": v(-38.1, -25.69) * mm});
            skLineSegment(sketch, "E22.1.0.43", {"start": v(-38.1, -68.93) * mm, "end": v(-22.23, -75.7) * mm});
            skLineSegment(sketch, "E22.2.0.0", {"start": v(-76.2, -50) * mm, "end": v(-60.33, -56.77) * mm});
            skLineSegment(sketch, "E22.2.0.1", {"start": v(-76.2, 87.85) * mm, "end": v(-92.08, 94.62) * mm});
            skLineSegment(sketch, "E22.2.0.2", {"start": v(-92.08, 56.77) * mm, "end": v(-76.2, 63.53) * mm});
            skLineSegment(sketch, "E22.2.0.3", {"start": v(-76.2, 44.6) * mm, "end": v(-60.33, 37.85) * mm});
            skLineSegment(sketch, "E22.2.0.4", {"start": v(-76.2, 31.08) * mm, "end": v(-92.08, 37.85) * mm});
            skLineSegment(sketch, "E22.2.0.5", {"start": v(-60.33, 37.85) * mm, "end": v(-76.2, 31.08) * mm});
            skLineSegment(sketch, "E22.2.0.6", {"start": v(-92.08, 37.85) * mm, "end": v(-76.2, 44.6) * mm});
            skLineSegment(sketch, "E22.2.0.7", {"start": v(-76.2, 25.69) * mm, "end": v(-60.33, 18.92) * mm});
            skLineSegment(sketch, "E22.2.0.8", {"start": v(-76.2, 12.16) * mm, "end": v(-92.08, 18.92) * mm});
            skLineSegment(sketch, "E22.2.0.9", {"start": v(-60.33, 18.92) * mm, "end": v(-76.2, 12.16) * mm});
            skLineSegment(sketch, "E22.2.0.10", {"start": v(-92.08, 18.92) * mm, "end": v(-76.2, 25.69) * mm});
            skLineSegment(sketch, "E22.2.0.11", {"start": v(-76.2, -6.76) * mm, "end": v(-92.08, 0) * mm});
            skLineSegment(sketch, "E22.2.0.12", {"start": v(-60.33, 0) * mm, "end": v(-76.2, -6.76) * mm});
            skLineSegment(sketch, "E22.2.0.13", {"start": v(-76.2, 6.76) * mm, "end": v(-60.33, 0) * mm});
            skLineSegment(sketch, "E22.2.0.14", {"start": v(-92.08, 0) * mm, "end": v(-76.2, 6.76) * mm});
            skLineSegment(sketch, "E22.2.0.15", {"start": v(-60.33, -56.77) * mm, "end": v(-76.2, -63.53) * mm});
            skLineSegment(sketch, "E22.2.0.16", {"start": v(-76.2, 63.53) * mm, "end": v(-60.33, 56.77) * mm});
            skLineSegment(sketch, "E22.2.0.17", {"start": v(-76.2, 50) * mm, "end": v(-92.08, 56.77) * mm});
            skLineSegment(sketch, "E22.2.0.18", {"start": v(-60.33, 56.77) * mm, "end": v(-76.2, 50) * mm});
            skLineSegment(sketch, "E22.2.0.19", {"start": v(-60.33, 94.62) * mm, "end": v(-76.2, 87.85) * mm});
            skLineSegment(sketch, "E22.2.0.20", {"start": v(-76.2, -63.53) * mm, "end": v(-92.08, -56.77) * mm});
            skLineSegment(sketch, "E22.2.0.21", {"start": v(-92.08, 94.62) * mm, "end": v(-76.2, 101.38) * mm});
            skLineSegment(sketch, "E22.2.0.22", {"start": v(-76.2, 82.45) * mm, "end": v(-60.33, 75.7) * mm});
            skLineSegment(sketch, "E22.2.0.23", {"start": v(-76.2, 68.93) * mm, "end": v(-92.08, 75.7) * mm});
            skLineSegment(sketch, "E22.2.0.24", {"start": v(-92.08, -37.85) * mm, "end": v(-76.2, -31.08) * mm});
            skLineSegment(sketch, "E22.2.0.25", {"start": v(-60.33, 75.7) * mm, "end": v(-76.2, 68.93) * mm});
            skLineSegment(sketch, "E22.2.0.26", {"start": v(-92.08, -94.62) * mm, "end": v(-76.2, -87.85) * mm});
            skLineSegment(sketch, "E22.2.0.27", {"start": v(-76.2, -31.08) * mm, "end": v(-60.33, -37.85) * mm});
            skLineSegment(sketch, "E22.2.0.28", {"start": v(-76.2, -87.85) * mm, "end": v(-60.33, -94.62) * mm});
            skLineSegment(sketch, "E22.2.0.29", {"start": v(-60.33, -37.85) * mm, "end": v(-76.2, -44.6) * mm});
            skLineSegment(sketch, "E22.2.0.30", {"start": v(-92.08, 75.7) * mm, "end": v(-76.2, 82.45) * mm});
            skLineSegment(sketch, "E22.2.0.31", {"start": v(-60.33, -94.62) * mm, "end": v(-76.2, -101.38) * mm});
            skLineSegment(sketch, "E22.2.0.32", {"start": v(-76.2, -44.6) * mm, "end": v(-92.08, -37.85) * mm});
            skLineSegment(sketch, "E22.2.0.33", {"start": v(-60.33, -75.7) * mm, "end": v(-76.2, -82.45) * mm});
            skLineSegment(sketch, "E22.2.0.34", {"start": v(-76.2, -25.69) * mm, "end": v(-92.08, -18.92) * mm});
            skLineSegment(sketch, "E22.2.0.35", {"start": v(-76.2, -101.38) * mm, "end": v(-92.08, -94.61) * mm});
            skLineSegment(sketch, "E22.2.0.36", {"start": v(-76.2, -82.45) * mm, "end": v(-92.08, -75.7) * mm});
            skLineSegment(sketch, "E22.2.0.37", {"start": v(-92.08, -75.7) * mm, "end": v(-76.2, -68.93) * mm});
            skLineSegment(sketch, "E22.2.0.38", {"start": v(-76.2, -12.16) * mm, "end": v(-60.33, -18.92) * mm});
            skLineSegment(sketch, "E22.2.0.39", {"start": v(-92.08, -18.92) * mm, "end": v(-76.2, -12.16) * mm});
            skLineSegment(sketch, "E22.2.0.40", {"start": v(-92.08, -56.77) * mm, "end": v(-76.2, -50) * mm});
            skLineSegment(sketch, "E22.2.0.41", {"start": v(-76.2, 101.38) * mm, "end": v(-60.33, 94.62) * mm});
            skLineSegment(sketch, "E22.2.0.42", {"start": v(-60.33, -18.92) * mm, "end": v(-76.2, -25.69) * mm});
            skLineSegment(sketch, "E22.2.0.43", {"start": v(-76.2, -68.93) * mm, "end": v(-60.33, -75.7) * mm});
            skLineSegment(sketch, "E22.3.0.0", {"start": v(-114.3, -50) * mm, "end": v(-98.43, -56.77) * mm});
            skLineSegment(sketch, "E22.3.0.1", {"start": v(-114.3, 87.85) * mm, "end": v(-130.18, 94.62) * mm});
            skLineSegment(sketch, "E22.3.0.2", {"start": v(-130.18, 56.77) * mm, "end": v(-114.3, 63.53) * mm});
            skLineSegment(sketch, "E22.3.0.3", {"start": v(-114.3, 44.6) * mm, "end": v(-98.43, 37.85) * mm});
            skLineSegment(sketch, "E22.3.0.4", {"start": v(-114.3, 31.08) * mm, "end": v(-130.18, 37.85) * mm});
            skLineSegment(sketch, "E22.3.0.5", {"start": v(-98.43, 37.85) * mm, "end": v(-114.3, 31.08) * mm});
            skLineSegment(sketch, "E22.3.0.6", {"start": v(-130.18, 37.85) * mm, "end": v(-114.3, 44.6) * mm});
            skLineSegment(sketch, "E22.3.0.7", {"start": v(-114.3, 25.69) * mm, "end": v(-98.43, 18.92) * mm});
            skLineSegment(sketch, "E22.3.0.8", {"start": v(-114.3, 12.16) * mm, "end": v(-130.18, 18.92) * mm});
            skLineSegment(sketch, "E22.3.0.9", {"start": v(-98.43, 18.92) * mm, "end": v(-114.3, 12.16) * mm});
            skLineSegment(sketch, "E22.3.0.10", {"start": v(-130.18, 18.92) * mm, "end": v(-114.3, 25.69) * mm});
            skLineSegment(sketch, "E22.3.0.11", {"start": v(-114.3, -6.76) * mm, "end": v(-130.18, 0) * mm});
            skLineSegment(sketch, "E22.3.0.12", {"start": v(-98.43, 0) * mm, "end": v(-114.3, -6.76) * mm});
            skLineSegment(sketch, "E22.3.0.13", {"start": v(-114.3, 6.76) * mm, "end": v(-98.43, 0) * mm});
            skLineSegment(sketch, "E22.3.0.14", {"start": v(-130.18, 0) * mm, "end": v(-114.3, 6.76) * mm});
            skLineSegment(sketch, "E22.3.0.15", {"start": v(-98.43, -56.77) * mm, "end": v(-114.3, -63.53) * mm});
            skLineSegment(sketch, "E22.3.0.16", {"start": v(-114.3, 63.53) * mm, "end": v(-98.43, 56.77) * mm});
            skLineSegment(sketch, "E22.3.0.17", {"start": v(-114.3, 50) * mm, "end": v(-130.18, 56.77) * mm});
            skLineSegment(sketch, "E22.3.0.18", {"start": v(-98.43, 56.77) * mm, "end": v(-114.3, 50) * mm});
            skLineSegment(sketch, "E22.3.0.19", {"start": v(-98.43, 94.62) * mm, "end": v(-114.3, 87.85) * mm});
            skLineSegment(sketch, "E22.3.0.20", {"start": v(-114.3, -63.53) * mm, "end": v(-130.18, -56.77) * mm});
            skLineSegment(sketch, "E22.3.0.21", {"start": v(-130.18, 94.62) * mm, "end": v(-114.3, 101.38) * mm});
            skLineSegment(sketch, "E22.3.0.22", {"start": v(-114.3, 82.45) * mm, "end": v(-98.43, 75.7) * mm});
            skLineSegment(sketch, "E22.3.0.23", {"start": v(-114.3, 68.93) * mm, "end": v(-130.18, 75.7) * mm});
            skLineSegment(sketch, "E22.3.0.24", {"start": v(-130.18, -37.85) * mm, "end": v(-114.3, -31.08) * mm});
            skLineSegment(sketch, "E22.3.0.25", {"start": v(-98.43, 75.7) * mm, "end": v(-114.3, 68.93) * mm});
            skLineSegment(sketch, "E22.3.0.26", {"start": v(-130.18, -94.62) * mm, "end": v(-114.3, -87.85) * mm});
            skLineSegment(sketch, "E22.3.0.27", {"start": v(-114.3, -31.08) * mm, "end": v(-98.43, -37.85) * mm});
            skLineSegment(sketch, "E22.3.0.28", {"start": v(-114.3, -87.85) * mm, "end": v(-98.43, -94.62) * mm});
            skLineSegment(sketch, "E22.3.0.29", {"start": v(-98.43, -37.85) * mm, "end": v(-114.3, -44.6) * mm});
            skLineSegment(sketch, "E22.3.0.30", {"start": v(-130.18, 75.7) * mm, "end": v(-114.3, 82.45) * mm});
            skLineSegment(sketch, "E22.3.0.31", {"start": v(-98.43, -94.62) * mm, "end": v(-114.3, -101.38) * mm});
            skLineSegment(sketch, "E22.3.0.32", {"start": v(-114.3, -44.6) * mm, "end": v(-130.18, -37.85) * mm});
            skLineSegment(sketch, "E22.3.0.33", {"start": v(-98.43, -75.7) * mm, "end": v(-114.3, -82.45) * mm});
            skLineSegment(sketch, "E22.3.0.34", {"start": v(-114.3, -25.69) * mm, "end": v(-130.18, -18.92) * mm});
            skLineSegment(sketch, "E22.3.0.35", {"start": v(-114.3, -101.38) * mm, "end": v(-130.18, -94.61) * mm});
            skLineSegment(sketch, "E22.3.0.36", {"start": v(-114.3, -82.45) * mm, "end": v(-130.18, -75.7) * mm});
            skLineSegment(sketch, "E22.3.0.37", {"start": v(-130.18, -75.7) * mm, "end": v(-114.3, -68.93) * mm});
            skLineSegment(sketch, "E22.3.0.38", {"start": v(-114.3, -12.16) * mm, "end": v(-98.43, -18.92) * mm});
            skLineSegment(sketch, "E22.3.0.39", {"start": v(-130.18, -18.92) * mm, "end": v(-114.3, -12.16) * mm});
            skLineSegment(sketch, "E22.3.0.40", {"start": v(-130.18, -56.77) * mm, "end": v(-114.3, -50) * mm});
            skLineSegment(sketch, "E22.3.0.41", {"start": v(-114.3, 101.38) * mm, "end": v(-98.43, 94.62) * mm});
            skLineSegment(sketch, "E22.3.0.42", {"start": v(-98.43, -18.92) * mm, "end": v(-114.3, -25.69) * mm});
            skLineSegment(sketch, "E22.3.0.43", {"start": v(-114.3, -68.93) * mm, "end": v(-98.43, -75.7) * mm});
            skLineSegment(sketch, "E22.4.0.0", {"start": v(-152.4, -50) * mm, "end": v(-136.53, -56.77) * mm});
            skLineSegment(sketch, "E22.4.0.1", {"start": v(-152.4, 87.85) * mm, "end": v(-168.28, 94.62) * mm});
            skLineSegment(sketch, "E22.4.0.2", {"start": v(-168.28, 56.77) * mm, "end": v(-152.4, 63.53) * mm});
            skLineSegment(sketch, "E22.4.0.3", {"start": v(-152.4, 44.6) * mm, "end": v(-136.53, 37.85) * mm});
            skLineSegment(sketch, "E22.4.0.4", {"start": v(-152.4, 31.08) * mm, "end": v(-168.28, 37.85) * mm});
            skLineSegment(sketch, "E22.4.0.5", {"start": v(-136.53, 37.85) * mm, "end": v(-152.4, 31.08) * mm});
            skLineSegment(sketch, "E22.4.0.6", {"start": v(-168.28, 37.85) * mm, "end": v(-152.4, 44.6) * mm});
            skLineSegment(sketch, "E22.4.0.7", {"start": v(-152.4, 25.69) * mm, "end": v(-136.53, 18.92) * mm});
            skLineSegment(sketch, "E22.4.0.8", {"start": v(-152.4, 12.16) * mm, "end": v(-168.28, 18.92) * mm});
            skLineSegment(sketch, "E22.4.0.9", {"start": v(-136.53, 18.92) * mm, "end": v(-152.4, 12.16) * mm});
            skLineSegment(sketch, "E22.4.0.10", {"start": v(-168.28, 18.92) * mm, "end": v(-152.4, 25.69) * mm});
            skLineSegment(sketch, "E22.4.0.11", {"start": v(-152.4, -6.76) * mm, "end": v(-168.28, 0) * mm});
            skLineSegment(sketch, "E22.4.0.12", {"start": v(-136.53, 0) * mm, "end": v(-152.4, -6.76) * mm});
            skLineSegment(sketch, "E22.4.0.13", {"start": v(-152.4, 6.76) * mm, "end": v(-136.53, 0) * mm});
            skLineSegment(sketch, "E22.4.0.14", {"start": v(-168.28, 0) * mm, "end": v(-152.4, 6.76) * mm});
            skLineSegment(sketch, "E22.4.0.15", {"start": v(-136.53, -56.77) * mm, "end": v(-152.4, -63.53) * mm});
            skLineSegment(sketch, "E22.4.0.16", {"start": v(-152.4, 63.53) * mm, "end": v(-136.53, 56.77) * mm});
            skLineSegment(sketch, "E22.4.0.17", {"start": v(-152.4, 50) * mm, "end": v(-168.28, 56.77) * mm});
            skLineSegment(sketch, "E22.4.0.18", {"start": v(-136.53, 56.77) * mm, "end": v(-152.4, 50) * mm});
            skLineSegment(sketch, "E22.4.0.19", {"start": v(-136.53, 94.62) * mm, "end": v(-152.4, 87.85) * mm});
            skLineSegment(sketch, "E22.4.0.20", {"start": v(-152.4, -63.53) * mm, "end": v(-168.28, -56.77) * mm});
            skLineSegment(sketch, "E22.4.0.21", {"start": v(-168.28, 94.62) * mm, "end": v(-152.4, 101.38) * mm});
            skLineSegment(sketch, "E22.4.0.22", {"start": v(-152.4, 82.45) * mm, "end": v(-136.53, 75.7) * mm});
            skLineSegment(sketch, "E22.4.0.23", {"start": v(-152.4, 68.93) * mm, "end": v(-168.28, 75.7) * mm});
            skLineSegment(sketch, "E22.4.0.24", {"start": v(-168.28, -37.85) * mm, "end": v(-152.4, -31.08) * mm});
            skLineSegment(sketch, "E22.4.0.25", {"start": v(-136.53, 75.7) * mm, "end": v(-152.4, 68.93) * mm});
            skLineSegment(sketch, "E22.4.0.26", {"start": v(-168.28, -94.62) * mm, "end": v(-152.4, -87.85) * mm});
            skLineSegment(sketch, "E22.4.0.27", {"start": v(-152.4, -31.08) * mm, "end": v(-136.53, -37.85) * mm});
            skLineSegment(sketch, "E22.4.0.28", {"start": v(-152.4, -87.85) * mm, "end": v(-136.53, -94.62) * mm});
            skLineSegment(sketch, "E22.4.0.29", {"start": v(-136.53, -37.85) * mm, "end": v(-152.4, -44.6) * mm});
            skLineSegment(sketch, "E22.4.0.30", {"start": v(-168.28, 75.7) * mm, "end": v(-152.4, 82.45) * mm});
            skLineSegment(sketch, "E22.4.0.31", {"start": v(-136.53, -94.62) * mm, "end": v(-152.4, -101.38) * mm});
            skLineSegment(sketch, "E22.4.0.32", {"start": v(-152.4, -44.6) * mm, "end": v(-168.28, -37.85) * mm});
            skLineSegment(sketch, "E22.4.0.33", {"start": v(-136.53, -75.7) * mm, "end": v(-152.4, -82.45) * mm});
            skLineSegment(sketch, "E22.4.0.34", {"start": v(-152.4, -25.69) * mm, "end": v(-168.28, -18.92) * mm});
            skLineSegment(sketch, "E22.4.0.35", {"start": v(-152.4, -101.38) * mm, "end": v(-168.28, -94.61) * mm});
            skLineSegment(sketch, "E22.4.0.36", {"start": v(-152.4, -82.45) * mm, "end": v(-168.28, -75.7) * mm});
            skLineSegment(sketch, "E22.4.0.37", {"start": v(-168.28, -75.7) * mm, "end": v(-152.4, -68.93) * mm});
            skLineSegment(sketch, "E22.4.0.38", {"start": v(-152.4, -12.16) * mm, "end": v(-136.53, -18.92) * mm});
            skLineSegment(sketch, "E22.4.0.39", {"start": v(-168.28, -18.92) * mm, "end": v(-152.4, -12.16) * mm});
            skLineSegment(sketch, "E22.4.0.40", {"start": v(-168.28, -56.77) * mm, "end": v(-152.4, -50) * mm});
            skLineSegment(sketch, "E22.4.0.41", {"start": v(-152.4, 101.38) * mm, "end": v(-136.53, 94.62) * mm});
            skLineSegment(sketch, "E22.4.0.42", {"start": v(-136.53, -18.92) * mm, "end": v(-152.4, -25.69) * mm});
            skLineSegment(sketch, "E22.4.0.43", {"start": v(-152.4, -68.93) * mm, "end": v(-136.53, -75.7) * mm});
            skLineSegment(sketch, "E22.direction1", {"start": v(-15.88, -94.62) * mm, "end": v(-53.98, -94.62) * mm, "construction": true});
            skLineSegment(sketch, "E23", {"start": v(155.57, -85.15) * mm, "end": v(171.45, -78.4) * mm});
            skLineSegment(sketch, "E24", {"start": v(171.45, -78.4) * mm, "end": v(187.32, -85.15) * mm});
            skLineSegment(sketch, "E25", {"start": v(187.32, -85.15) * mm, "end": v(171.45, -91.92) * mm});
            skLineSegment(sketch, "E26", {"start": v(171.45, -91.92) * mm, "end": v(155.57, -85.15) * mm});
            skLineSegment(sketch, "E27.0.1.0", {"start": v(171.45, -73) * mm, "end": v(155.57, -66.23) * mm});
            skLineSegment(sketch, "E27.0.1.1", {"start": v(155.57, -66.23) * mm, "end": v(171.45, -59.47) * mm});
            skLineSegment(sketch, "E27.0.1.2", {"start": v(171.45, -59.47) * mm, "end": v(187.32, -66.23) * mm});
            skLineSegment(sketch, "E27.0.1.3", {"start": v(187.32, -66.23) * mm, "end": v(171.45, -73) * mm});
            skLineSegment(sketch, "E27.0.2.0", {"start": v(171.45, -54.07) * mm, "end": v(155.57, -47.3) * mm});
            skLineSegment(sketch, "E27.0.2.1", {"start": v(155.57, -47.3) * mm, "end": v(171.45, -40.54) * mm});
            skLineSegment(sketch, "E27.0.2.2", {"start": v(171.45, -40.54) * mm, "end": v(187.32, -47.3) * mm});
            skLineSegment(sketch, "E27.0.2.3", {"start": v(187.32, -47.3) * mm, "end": v(171.45, -54.07) * mm});
            skLineSegment(sketch, "E27.0.3.0", {"start": v(171.45, -35.15) * mm, "end": v(155.57, -28.38) * mm});
            skLineSegment(sketch, "E27.0.3.1", {"start": v(155.57, -28.38) * mm, "end": v(171.45, -21.62) * mm});
            skLineSegment(sketch, "E27.0.3.2", {"start": v(171.45, -21.62) * mm, "end": v(187.32, -28.38) * mm});
            skLineSegment(sketch, "E27.0.3.3", {"start": v(187.32, -28.38) * mm, "end": v(171.45, -35.15) * mm});
            skLineSegment(sketch, "E27.0.4.0", {"start": v(171.45, -16.22) * mm, "end": v(155.57, -9.46) * mm});
            skLineSegment(sketch, "E27.0.4.1", {"start": v(155.57, -9.46) * mm, "end": v(171.45, -2.7) * mm});
            skLineSegment(sketch, "E27.0.4.2", {"start": v(171.45, -2.7) * mm, "end": v(187.32, -9.46) * mm});
            skLineSegment(sketch, "E27.0.4.3", {"start": v(187.32, -9.46) * mm, "end": v(171.45, -16.22) * mm});
            skLineSegment(sketch, "E27.0.5.0", {"start": v(171.45, 2.7) * mm, "end": v(155.57, 9.46) * mm});
            skLineSegment(sketch, "E27.0.5.1", {"start": v(155.57, 9.46) * mm, "end": v(171.45, 16.22) * mm});
            skLineSegment(sketch, "E27.0.5.2", {"start": v(171.45, 16.22) * mm, "end": v(187.32, 9.46) * mm});
            skLineSegment(sketch, "E27.0.5.3", {"start": v(187.32, 9.46) * mm, "end": v(171.45, 2.7) * mm});
            skLineSegment(sketch, "E27.0.6.0", {"start": v(171.45, 21.62) * mm, "end": v(155.57, 28.38) * mm});
            skLineSegment(sketch, "E27.0.6.1", {"start": v(155.57, 28.38) * mm, "end": v(171.45, 35.15) * mm});
            skLineSegment(sketch, "E27.0.6.2", {"start": v(171.45, 35.15) * mm, "end": v(187.32, 28.38) * mm});
            skLineSegment(sketch, "E27.0.6.3", {"start": v(187.32, 28.38) * mm, "end": v(171.45, 21.62) * mm});
            skLineSegment(sketch, "E27.0.7.0", {"start": v(171.45, 40.54) * mm, "end": v(155.57, 47.3) * mm});
            skLineSegment(sketch, "E27.0.7.1", {"start": v(155.57, 47.3) * mm, "end": v(171.45, 54.07) * mm});
            skLineSegment(sketch, "E27.0.7.2", {"start": v(171.45, 54.07) * mm, "end": v(187.32, 47.3) * mm});
            skLineSegment(sketch, "E27.0.7.3", {"start": v(187.32, 47.3) * mm, "end": v(171.45, 40.54) * mm});
            skLineSegment(sketch, "E27.0.8.0", {"start": v(171.45, 59.47) * mm, "end": v(155.57, 66.23) * mm});
            skLineSegment(sketch, "E27.0.8.1", {"start": v(155.57, 66.23) * mm, "end": v(171.45, 73) * mm});
            skLineSegment(sketch, "E27.0.8.2", {"start": v(171.45, 73) * mm, "end": v(187.32, 66.23) * mm});
            skLineSegment(sketch, "E27.0.8.3", {"start": v(187.32, 66.23) * mm, "end": v(171.45, 59.47) * mm});
            skLineSegment(sketch, "E27.0.9.0", {"start": v(171.45, 78.4) * mm, "end": v(155.57, 85.15) * mm});
            skLineSegment(sketch, "E27.0.9.1", {"start": v(155.57, 85.15) * mm, "end": v(171.45, 91.92) * mm});
            skLineSegment(sketch, "E27.0.9.2", {"start": v(171.45, 91.92) * mm, "end": v(187.32, 85.15) * mm});
            skLineSegment(sketch, "E27.0.9.3", {"start": v(187.32, 85.15) * mm, "end": v(171.45, 78.4) * mm});
            skLineSegment(sketch, "E27.1.0.0", {"start": v(133.35, -91.92) * mm, "end": v(117.47, -85.15) * mm});
            skLineSegment(sketch, "E27.1.0.1", {"start": v(117.47, -85.15) * mm, "end": v(133.35, -78.4) * mm});
            skLineSegment(sketch, "E27.1.0.2", {"start": v(133.35, -78.4) * mm, "end": v(149.22, -85.15) * mm});
            skLineSegment(sketch, "E27.1.0.3", {"start": v(149.22, -85.15) * mm, "end": v(133.35, -91.92) * mm});
            skLineSegment(sketch, "E27.1.1.0", {"start": v(133.35, -73) * mm, "end": v(117.47, -66.23) * mm});
            skLineSegment(sketch, "E27.1.1.1", {"start": v(117.47, -66.23) * mm, "end": v(133.35, -59.47) * mm});
            skLineSegment(sketch, "E27.1.1.2", {"start": v(133.35, -59.47) * mm, "end": v(149.22, -66.23) * mm});
            skLineSegment(sketch, "E27.1.1.3", {"start": v(149.22, -66.23) * mm, "end": v(133.35, -73) * mm});
            skLineSegment(sketch, "E27.1.2.0", {"start": v(133.35, -54.07) * mm, "end": v(117.47, -47.3) * mm});
            skLineSegment(sketch, "E27.1.2.1", {"start": v(117.47, -47.3) * mm, "end": v(133.35, -40.54) * mm});
            skLineSegment(sketch, "E27.1.2.2", {"start": v(133.35, -40.54) * mm, "end": v(149.22, -47.3) * mm});
            skLineSegment(sketch, "E27.1.2.3", {"start": v(149.22, -47.3) * mm, "end": v(133.35, -54.07) * mm});
            skLineSegment(sketch, "E27.1.3.0", {"start": v(133.35, -35.15) * mm, "end": v(117.47, -28.38) * mm});
            skLineSegment(sketch, "E27.1.3.1", {"start": v(117.47, -28.38) * mm, "end": v(133.35, -21.62) * mm});
            skLineSegment(sketch, "E27.1.3.2", {"start": v(133.35, -21.62) * mm, "end": v(149.22, -28.38) * mm});
            skLineSegment(sketch, "E27.1.3.3", {"start": v(149.22, -28.38) * mm, "end": v(133.35, -35.15) * mm});
            skLineSegment(sketch, "E27.1.4.0", {"start": v(133.35, -16.22) * mm, "end": v(117.47, -9.46) * mm});
            skLineSegment(sketch, "E27.1.4.1", {"start": v(117.47, -9.46) * mm, "end": v(133.35, -2.7) * mm});
            skLineSegment(sketch, "E27.1.4.2", {"start": v(133.35, -2.7) * mm, "end": v(149.22, -9.46) * mm});
            skLineSegment(sketch, "E27.1.4.3", {"start": v(149.22, -9.46) * mm, "end": v(133.35, -16.22) * mm});
            skLineSegment(sketch, "E27.1.5.0", {"start": v(133.35, 2.7) * mm, "end": v(117.47, 9.46) * mm});
            skLineSegment(sketch, "E27.1.5.1", {"start": v(117.47, 9.46) * mm, "end": v(133.35, 16.22) * mm});
            skLineSegment(sketch, "E27.1.5.2", {"start": v(133.35, 16.22) * mm, "end": v(149.22, 9.46) * mm});
            skLineSegment(sketch, "E27.1.5.3", {"start": v(149.22, 9.46) * mm, "end": v(133.35, 2.7) * mm});
            skLineSegment(sketch, "E27.1.6.0", {"start": v(133.35, 21.62) * mm, "end": v(117.47, 28.38) * mm});
            skLineSegment(sketch, "E27.1.6.1", {"start": v(117.47, 28.38) * mm, "end": v(133.35, 35.15) * mm});
            skLineSegment(sketch, "E27.1.6.2", {"start": v(133.35, 35.15) * mm, "end": v(149.22, 28.38) * mm});
            skLineSegment(sketch, "E27.1.6.3", {"start": v(149.22, 28.38) * mm, "end": v(133.35, 21.62) * mm});
            skLineSegment(sketch, "E27.1.7.0", {"start": v(133.35, 40.54) * mm, "end": v(117.47, 47.3) * mm});
            skLineSegment(sketch, "E27.1.7.1", {"start": v(117.47, 47.3) * mm, "end": v(133.35, 54.07) * mm});
            skLineSegment(sketch, "E27.1.7.2", {"start": v(133.35, 54.07) * mm, "end": v(149.22, 47.3) * mm});
            skLineSegment(sketch, "E27.1.7.3", {"start": v(149.22, 47.3) * mm, "end": v(133.35, 40.54) * mm});
            skLineSegment(sketch, "E27.1.8.0", {"start": v(133.35, 59.47) * mm, "end": v(117.47, 66.23) * mm});
            skLineSegment(sketch, "E27.1.8.1", {"start": v(117.47, 66.23) * mm, "end": v(133.35, 73) * mm});
            skLineSegment(sketch, "E27.1.8.2", {"start": v(133.35, 73) * mm, "end": v(149.22, 66.23) * mm});
            skLineSegment(sketch, "E27.1.8.3", {"start": v(149.22, 66.23) * mm, "end": v(133.35, 59.47) * mm});
            skLineSegment(sketch, "E27.1.9.0", {"start": v(133.35, 78.4) * mm, "end": v(117.47, 85.15) * mm});
            skLineSegment(sketch, "E27.1.9.1", {"start": v(117.47, 85.15) * mm, "end": v(133.35, 91.92) * mm});
            skLineSegment(sketch, "E27.1.9.2", {"start": v(133.35, 91.92) * mm, "end": v(149.22, 85.15) * mm});
            skLineSegment(sketch, "E27.1.9.3", {"start": v(149.22, 85.15) * mm, "end": v(133.35, 78.4) * mm});
            skLineSegment(sketch, "E27.2.0.0", {"start": v(95.25, -91.92) * mm, "end": v(79.37, -85.15) * mm});
            skLineSegment(sketch, "E27.2.0.1", {"start": v(79.37, -85.15) * mm, "end": v(95.25, -78.4) * mm});
            skLineSegment(sketch, "E27.2.0.2", {"start": v(95.25, -78.4) * mm, "end": v(111.12, -85.15) * mm});
            skLineSegment(sketch, "E27.2.0.3", {"start": v(111.12, -85.15) * mm, "end": v(95.25, -91.92) * mm});
            skLineSegment(sketch, "E27.2.1.0", {"start": v(95.25, -73) * mm, "end": v(79.37, -66.23) * mm});
            skLineSegment(sketch, "E27.2.1.1", {"start": v(79.37, -66.23) * mm, "end": v(95.25, -59.47) * mm});
            skLineSegment(sketch, "E27.2.1.2", {"start": v(95.25, -59.47) * mm, "end": v(111.12, -66.23) * mm});
            skLineSegment(sketch, "E27.2.1.3", {"start": v(111.12, -66.23) * mm, "end": v(95.25, -73) * mm});
            skLineSegment(sketch, "E27.2.2.0", {"start": v(95.25, -54.07) * mm, "end": v(79.37, -47.3) * mm});
            skLineSegment(sketch, "E27.2.2.1", {"start": v(79.37, -47.3) * mm, "end": v(95.25, -40.54) * mm});
            skLineSegment(sketch, "E27.2.2.2", {"start": v(95.25, -40.54) * mm, "end": v(111.12, -47.3) * mm});
            skLineSegment(sketch, "E27.2.2.3", {"start": v(111.12, -47.3) * mm, "end": v(95.25, -54.07) * mm});
            skLineSegment(sketch, "E27.2.3.0", {"start": v(95.25, -35.15) * mm, "end": v(79.37, -28.38) * mm});
            skLineSegment(sketch, "E27.2.3.1", {"start": v(79.37, -28.38) * mm, "end": v(95.25, -21.62) * mm});
            skLineSegment(sketch, "E27.2.3.2", {"start": v(95.25, -21.62) * mm, "end": v(111.12, -28.38) * mm});
            skLineSegment(sketch, "E27.2.3.3", {"start": v(111.12, -28.38) * mm, "end": v(95.25, -35.15) * mm});
            skLineSegment(sketch, "E27.2.4.0", {"start": v(95.25, -16.22) * mm, "end": v(79.37, -9.46) * mm});
            skLineSegment(sketch, "E27.2.4.1", {"start": v(79.37, -9.46) * mm, "end": v(95.25, -2.7) * mm});
            skLineSegment(sketch, "E27.2.4.2", {"start": v(95.25, -2.7) * mm, "end": v(111.12, -9.46) * mm});
            skLineSegment(sketch, "E27.2.4.3", {"start": v(111.12, -9.46) * mm, "end": v(95.25, -16.22) * mm});
            skLineSegment(sketch, "E27.2.5.0", {"start": v(95.25, 2.7) * mm, "end": v(79.37, 9.46) * mm});
            skLineSegment(sketch, "E27.2.5.1", {"start": v(79.37, 9.46) * mm, "end": v(95.25, 16.22) * mm});
            skLineSegment(sketch, "E27.2.5.2", {"start": v(95.25, 16.22) * mm, "end": v(111.12, 9.46) * mm});
            skLineSegment(sketch, "E27.2.5.3", {"start": v(111.12, 9.46) * mm, "end": v(95.25, 2.7) * mm});
            skLineSegment(sketch, "E27.2.6.0", {"start": v(95.25, 21.62) * mm, "end": v(79.37, 28.38) * mm});
            skLineSegment(sketch, "E27.2.6.1", {"start": v(79.37, 28.38) * mm, "end": v(95.25, 35.15) * mm});
            skLineSegment(sketch, "E27.2.6.2", {"start": v(95.25, 35.15) * mm, "end": v(111.12, 28.38) * mm});
            skLineSegment(sketch, "E27.2.6.3", {"start": v(111.12, 28.38) * mm, "end": v(95.25, 21.62) * mm});
            skLineSegment(sketch, "E27.2.7.0", {"start": v(95.25, 40.54) * mm, "end": v(79.37, 47.3) * mm});
            skLineSegment(sketch, "E27.2.7.1", {"start": v(79.37, 47.3) * mm, "end": v(95.25, 54.07) * mm});
            skLineSegment(sketch, "E27.2.7.2", {"start": v(95.25, 54.07) * mm, "end": v(111.12, 47.3) * mm});
            skLineSegment(sketch, "E27.2.7.3", {"start": v(111.12, 47.3) * mm, "end": v(95.25, 40.54) * mm});
            skLineSegment(sketch, "E27.2.8.0", {"start": v(95.25, 59.47) * mm, "end": v(79.37, 66.23) * mm});
            skLineSegment(sketch, "E27.2.8.1", {"start": v(79.37, 66.23) * mm, "end": v(95.25, 73) * mm});
            skLineSegment(sketch, "E27.2.8.2", {"start": v(95.25, 73) * mm, "end": v(111.12, 66.23) * mm});
            skLineSegment(sketch, "E27.2.8.3", {"start": v(111.12, 66.23) * mm, "end": v(95.25, 59.47) * mm});
            skLineSegment(sketch, "E27.2.9.0", {"start": v(95.25, 78.4) * mm, "end": v(79.37, 85.15) * mm});
            skLineSegment(sketch, "E27.2.9.1", {"start": v(79.37, 85.15) * mm, "end": v(95.25, 91.92) * mm});
            skLineSegment(sketch, "E27.2.9.2", {"start": v(95.25, 91.92) * mm, "end": v(111.12, 85.15) * mm});
            skLineSegment(sketch, "E27.2.9.3", {"start": v(111.12, 85.15) * mm, "end": v(95.25, 78.4) * mm});
            skLineSegment(sketch, "E27.3.0.0", {"start": v(57.15, -91.92) * mm, "end": v(41.27, -85.15) * mm});
            skLineSegment(sketch, "E27.3.0.1", {"start": v(41.27, -85.15) * mm, "end": v(57.15, -78.4) * mm});
            skLineSegment(sketch, "E27.3.0.2", {"start": v(57.15, -78.4) * mm, "end": v(73.02, -85.15) * mm});
            skLineSegment(sketch, "E27.3.0.3", {"start": v(73.02, -85.15) * mm, "end": v(57.15, -91.92) * mm});
            skLineSegment(sketch, "E27.3.1.0", {"start": v(57.15, -73) * mm, "end": v(41.27, -66.23) * mm});
            skLineSegment(sketch, "E27.3.1.1", {"start": v(41.27, -66.23) * mm, "end": v(57.15, -59.47) * mm});
            skLineSegment(sketch, "E27.3.1.2", {"start": v(57.15, -59.47) * mm, "end": v(73.02, -66.23) * mm});
            skLineSegment(sketch, "E27.3.1.3", {"start": v(73.02, -66.23) * mm, "end": v(57.15, -73) * mm});
            skLineSegment(sketch, "E27.3.2.0", {"start": v(57.15, -54.07) * mm, "end": v(41.27, -47.3) * mm});
            skLineSegment(sketch, "E27.3.2.1", {"start": v(41.27, -47.3) * mm, "end": v(57.15, -40.54) * mm});
            skLineSegment(sketch, "E27.3.2.2", {"start": v(57.15, -40.54) * mm, "end": v(73.02, -47.3) * mm});
            skLineSegment(sketch, "E27.3.2.3", {"start": v(73.02, -47.3) * mm, "end": v(57.15, -54.07) * mm});
            skLineSegment(sketch, "E27.3.3.0", {"start": v(57.15, -35.15) * mm, "end": v(41.27, -28.38) * mm});
            skLineSegment(sketch, "E27.3.3.1", {"start": v(41.27, -28.38) * mm, "end": v(57.15, -21.62) * mm});
            skLineSegment(sketch, "E27.3.3.2", {"start": v(57.15, -21.62) * mm, "end": v(73.02, -28.38) * mm});
            skLineSegment(sketch, "E27.3.3.3", {"start": v(73.02, -28.38) * mm, "end": v(57.15, -35.15) * mm});
            skLineSegment(sketch, "E27.3.4.0", {"start": v(57.15, -16.22) * mm, "end": v(41.27, -9.46) * mm});
            skLineSegment(sketch, "E27.3.4.1", {"start": v(41.27, -9.46) * mm, "end": v(57.15, -2.7) * mm});
            skLineSegment(sketch, "E27.3.4.2", {"start": v(57.15, -2.7) * mm, "end": v(73.02, -9.46) * mm});
            skLineSegment(sketch, "E27.3.4.3", {"start": v(73.02, -9.46) * mm, "end": v(57.15, -16.22) * mm});
            skLineSegment(sketch, "E27.3.5.0", {"start": v(57.15, 2.7) * mm, "end": v(41.27, 9.46) * mm});
            skLineSegment(sketch, "E27.3.5.1", {"start": v(41.27, 9.46) * mm, "end": v(57.15, 16.22) * mm});
            skLineSegment(sketch, "E27.3.5.2", {"start": v(57.15, 16.22) * mm, "end": v(73.02, 9.46) * mm});
            skLineSegment(sketch, "E27.3.5.3", {"start": v(73.02, 9.46) * mm, "end": v(57.15, 2.7) * mm});
            skLineSegment(sketch, "E27.3.6.0", {"start": v(57.15, 21.62) * mm, "end": v(41.27, 28.38) * mm});
            skLineSegment(sketch, "E27.3.6.1", {"start": v(41.27, 28.38) * mm, "end": v(57.15, 35.15) * mm});
            skLineSegment(sketch, "E27.3.6.2", {"start": v(57.15, 35.15) * mm, "end": v(73.02, 28.38) * mm});
            skLineSegment(sketch, "E27.3.6.3", {"start": v(73.02, 28.38) * mm, "end": v(57.15, 21.62) * mm});
            skLineSegment(sketch, "E27.3.7.0", {"start": v(57.15, 40.54) * mm, "end": v(41.27, 47.3) * mm});
            skLineSegment(sketch, "E27.3.7.1", {"start": v(41.27, 47.3) * mm, "end": v(57.15, 54.07) * mm});
            skLineSegment(sketch, "E27.3.7.2", {"start": v(57.15, 54.07) * mm, "end": v(73.02, 47.3) * mm});
            skLineSegment(sketch, "E27.3.7.3", {"start": v(73.02, 47.3) * mm, "end": v(57.15, 40.54) * mm});
            skLineSegment(sketch, "E27.3.8.0", {"start": v(57.15, 59.47) * mm, "end": v(41.27, 66.23) * mm});
            skLineSegment(sketch, "E27.3.8.1", {"start": v(41.27, 66.23) * mm, "end": v(57.15, 73) * mm});
            skLineSegment(sketch, "E27.3.8.2", {"start": v(57.15, 73) * mm, "end": v(73.02, 66.23) * mm});
            skLineSegment(sketch, "E27.3.8.3", {"start": v(73.02, 66.23) * mm, "end": v(57.15, 59.47) * mm});
            skLineSegment(sketch, "E27.3.9.0", {"start": v(57.15, 78.4) * mm, "end": v(41.27, 85.15) * mm});
            skLineSegment(sketch, "E27.3.9.1", {"start": v(41.27, 85.15) * mm, "end": v(57.15, 91.92) * mm});
            skLineSegment(sketch, "E27.3.9.2", {"start": v(57.15, 91.92) * mm, "end": v(73.02, 85.15) * mm});
            skLineSegment(sketch, "E27.3.9.3", {"start": v(73.02, 85.15) * mm, "end": v(57.15, 78.4) * mm});
            skLineSegment(sketch, "E27.4.0.0", {"start": v(19.05, -91.92) * mm, "end": v(3.17, -85.15) * mm});
            skLineSegment(sketch, "E27.4.0.1", {"start": v(3.17, -85.15) * mm, "end": v(19.05, -78.4) * mm});
            skLineSegment(sketch, "E27.4.0.2", {"start": v(19.05, -78.4) * mm, "end": v(34.92, -85.15) * mm});
            skLineSegment(sketch, "E27.4.0.3", {"start": v(34.92, -85.15) * mm, "end": v(19.05, -91.92) * mm});
            skLineSegment(sketch, "E27.4.1.0", {"start": v(19.05, -73) * mm, "end": v(3.17, -66.23) * mm});
            skLineSegment(sketch, "E27.4.1.1", {"start": v(3.17, -66.23) * mm, "end": v(19.05, -59.47) * mm});
            skLineSegment(sketch, "E27.4.1.2", {"start": v(19.05, -59.47) * mm, "end": v(34.92, -66.23) * mm});
            skLineSegment(sketch, "E27.4.1.3", {"start": v(34.92, -66.23) * mm, "end": v(19.05, -73) * mm});
            skLineSegment(sketch, "E27.4.2.0", {"start": v(19.05, -54.07) * mm, "end": v(3.17, -47.3) * mm});
            skLineSegment(sketch, "E27.4.2.1", {"start": v(3.17, -47.3) * mm, "end": v(19.05, -40.54) * mm});
            skLineSegment(sketch, "E27.4.2.2", {"start": v(19.05, -40.54) * mm, "end": v(34.92, -47.3) * mm});
            skLineSegment(sketch, "E27.4.2.3", {"start": v(34.92, -47.3) * mm, "end": v(19.05, -54.07) * mm});
            skLineSegment(sketch, "E27.4.3.0", {"start": v(19.05, -35.15) * mm, "end": v(3.17, -28.38) * mm});
            skLineSegment(sketch, "E27.4.3.1", {"start": v(3.17, -28.38) * mm, "end": v(19.05, -21.62) * mm});
            skLineSegment(sketch, "E27.4.3.2", {"start": v(19.05, -21.62) * mm, "end": v(34.92, -28.38) * mm});
            skLineSegment(sketch, "E27.4.3.3", {"start": v(34.92, -28.38) * mm, "end": v(19.05, -35.15) * mm});
            skLineSegment(sketch, "E27.4.4.0", {"start": v(19.05, -16.22) * mm, "end": v(3.17, -9.46) * mm});
            skLineSegment(sketch, "E27.4.4.1", {"start": v(3.17, -9.46) * mm, "end": v(19.05, -2.7) * mm});
            skLineSegment(sketch, "E27.4.4.2", {"start": v(19.05, -2.7) * mm, "end": v(34.92, -9.46) * mm});
            skLineSegment(sketch, "E27.4.4.3", {"start": v(34.92, -9.46) * mm, "end": v(19.05, -16.22) * mm});
            skLineSegment(sketch, "E27.4.5.0", {"start": v(19.05, 2.7) * mm, "end": v(3.17, 9.46) * mm});
            skLineSegment(sketch, "E27.4.5.1", {"start": v(3.17, 9.46) * mm, "end": v(19.05, 16.22) * mm});
            skLineSegment(sketch, "E27.4.5.2", {"start": v(19.05, 16.22) * mm, "end": v(34.92, 9.46) * mm});
            skLineSegment(sketch, "E27.4.5.3", {"start": v(34.92, 9.46) * mm, "end": v(19.05, 2.7) * mm});
            skLineSegment(sketch, "E27.4.6.0", {"start": v(19.05, 21.62) * mm, "end": v(3.17, 28.38) * mm});
            skLineSegment(sketch, "E27.4.6.1", {"start": v(3.17, 28.38) * mm, "end": v(19.05, 35.15) * mm});
            skLineSegment(sketch, "E27.4.6.2", {"start": v(19.05, 35.15) * mm, "end": v(34.92, 28.38) * mm});
            skLineSegment(sketch, "E27.4.6.3", {"start": v(34.92, 28.38) * mm, "end": v(19.05, 21.62) * mm});
            skLineSegment(sketch, "E27.4.7.0", {"start": v(19.05, 40.54) * mm, "end": v(3.17, 47.3) * mm});
            skLineSegment(sketch, "E27.4.7.1", {"start": v(3.17, 47.3) * mm, "end": v(19.05, 54.07) * mm});
            skLineSegment(sketch, "E27.4.7.2", {"start": v(19.05, 54.07) * mm, "end": v(34.92, 47.3) * mm});
            skLineSegment(sketch, "E27.4.7.3", {"start": v(34.92, 47.3) * mm, "end": v(19.05, 40.54) * mm});
            skLineSegment(sketch, "E27.4.8.0", {"start": v(19.05, 59.47) * mm, "end": v(3.17, 66.23) * mm});
            skLineSegment(sketch, "E27.4.8.1", {"start": v(3.17, 66.23) * mm, "end": v(19.05, 73) * mm});
            skLineSegment(sketch, "E27.4.8.2", {"start": v(19.05, 73) * mm, "end": v(34.92, 66.23) * mm});
            skLineSegment(sketch, "E27.4.8.3", {"start": v(34.92, 66.23) * mm, "end": v(19.05, 59.47) * mm});
            skLineSegment(sketch, "E27.4.9.0", {"start": v(19.05, 78.4) * mm, "end": v(3.17, 85.15) * mm});
            skLineSegment(sketch, "E27.4.9.1", {"start": v(3.17, 85.15) * mm, "end": v(19.05, 91.92) * mm});
            skLineSegment(sketch, "E27.4.9.2", {"start": v(19.05, 91.92) * mm, "end": v(34.92, 85.15) * mm});
            skLineSegment(sketch, "E27.4.9.3", {"start": v(34.92, 85.15) * mm, "end": v(19.05, 78.4) * mm});
            skLineSegment(sketch, "E27.5.0.0", {"start": v(-19.05, -91.92) * mm, "end": v(-34.93, -85.15) * mm});
            skLineSegment(sketch, "E27.5.0.1", {"start": v(-34.93, -85.15) * mm, "end": v(-19.05, -78.4) * mm});
            skLineSegment(sketch, "E27.5.0.2", {"start": v(-19.05, -78.4) * mm, "end": v(-3.18, -85.15) * mm});
            skLineSegment(sketch, "E27.5.0.3", {"start": v(-3.18, -85.15) * mm, "end": v(-19.05, -91.92) * mm});
            skLineSegment(sketch, "E27.5.1.0", {"start": v(-19.05, -73) * mm, "end": v(-34.93, -66.23) * mm});
            skLineSegment(sketch, "E27.5.1.1", {"start": v(-34.93, -66.23) * mm, "end": v(-19.05, -59.47) * mm});
            skLineSegment(sketch, "E27.5.1.2", {"start": v(-19.05, -59.47) * mm, "end": v(-3.18, -66.23) * mm});
            skLineSegment(sketch, "E27.5.1.3", {"start": v(-3.18, -66.23) * mm, "end": v(-19.05, -73) * mm});
            skLineSegment(sketch, "E27.5.2.0", {"start": v(-19.05, -54.07) * mm, "end": v(-34.93, -47.3) * mm});
            skLineSegment(sketch, "E27.5.2.1", {"start": v(-34.93, -47.3) * mm, "end": v(-19.05, -40.54) * mm});
            skLineSegment(sketch, "E27.5.2.2", {"start": v(-19.05, -40.54) * mm, "end": v(-3.18, -47.3) * mm});
            skLineSegment(sketch, "E27.5.2.3", {"start": v(-3.18, -47.3) * mm, "end": v(-19.05, -54.07) * mm});
            skLineSegment(sketch, "E27.5.3.0", {"start": v(-19.05, -35.15) * mm, "end": v(-34.93, -28.38) * mm});
            skLineSegment(sketch, "E27.5.3.1", {"start": v(-34.93, -28.38) * mm, "end": v(-19.05, -21.62) * mm});
            skLineSegment(sketch, "E27.5.3.2", {"start": v(-19.05, -21.62) * mm, "end": v(-3.18, -28.38) * mm});
            skLineSegment(sketch, "E27.5.3.3", {"start": v(-3.18, -28.38) * mm, "end": v(-19.05, -35.15) * mm});
            skLineSegment(sketch, "E27.5.4.0", {"start": v(-19.05, -16.22) * mm, "end": v(-34.93, -9.46) * mm});
            skLineSegment(sketch, "E27.5.4.1", {"start": v(-34.93, -9.46) * mm, "end": v(-19.05, -2.7) * mm});
            skLineSegment(sketch, "E27.5.4.2", {"start": v(-19.05, -2.7) * mm, "end": v(-3.18, -9.46) * mm});
            skLineSegment(sketch, "E27.5.4.3", {"start": v(-3.18, -9.46) * mm, "end": v(-19.05, -16.22) * mm});
            skLineSegment(sketch, "E27.5.5.0", {"start": v(-19.05, 2.7) * mm, "end": v(-34.93, 9.46) * mm});
            skLineSegment(sketch, "E27.5.5.1", {"start": v(-34.93, 9.46) * mm, "end": v(-19.05, 16.22) * mm});
            skLineSegment(sketch, "E27.5.5.2", {"start": v(-19.05, 16.22) * mm, "end": v(-3.18, 9.46) * mm});
            skLineSegment(sketch, "E27.5.5.3", {"start": v(-3.18, 9.46) * mm, "end": v(-19.05, 2.7) * mm});
            skLineSegment(sketch, "E27.5.6.0", {"start": v(-19.05, 21.62) * mm, "end": v(-34.93, 28.38) * mm});
            skLineSegment(sketch, "E27.5.6.1", {"start": v(-34.93, 28.38) * mm, "end": v(-19.05, 35.15) * mm});
            skLineSegment(sketch, "E27.5.6.2", {"start": v(-19.05, 35.15) * mm, "end": v(-3.18, 28.38) * mm});
            skLineSegment(sketch, "E27.5.6.3", {"start": v(-3.18, 28.38) * mm, "end": v(-19.05, 21.62) * mm});
            skLineSegment(sketch, "E27.5.7.0", {"start": v(-19.05, 40.54) * mm, "end": v(-34.93, 47.3) * mm});
            skLineSegment(sketch, "E27.5.7.1", {"start": v(-34.93, 47.3) * mm, "end": v(-19.05, 54.07) * mm});
            skLineSegment(sketch, "E27.5.7.2", {"start": v(-19.05, 54.07) * mm, "end": v(-3.18, 47.3) * mm});
            skLineSegment(sketch, "E27.5.7.3", {"start": v(-3.18, 47.3) * mm, "end": v(-19.05, 40.54) * mm});
            skLineSegment(sketch, "E27.5.8.0", {"start": v(-19.05, 59.47) * mm, "end": v(-34.93, 66.23) * mm});
            skLineSegment(sketch, "E27.5.8.1", {"start": v(-34.93, 66.23) * mm, "end": v(-19.05, 73) * mm});
            skLineSegment(sketch, "E27.5.8.2", {"start": v(-19.05, 73) * mm, "end": v(-3.18, 66.23) * mm});
            skLineSegment(sketch, "E27.5.8.3", {"start": v(-3.18, 66.23) * mm, "end": v(-19.05, 59.47) * mm});
            skLineSegment(sketch, "E27.5.9.0", {"start": v(-19.05, 78.4) * mm, "end": v(-34.93, 85.15) * mm});
            skLineSegment(sketch, "E27.5.9.1", {"start": v(-34.93, 85.15) * mm, "end": v(-19.05, 91.92) * mm});
            skLineSegment(sketch, "E27.5.9.2", {"start": v(-19.05, 91.92) * mm, "end": v(-3.18, 85.15) * mm});
            skLineSegment(sketch, "E27.5.9.3", {"start": v(-3.18, 85.15) * mm, "end": v(-19.05, 78.4) * mm});
            skLineSegment(sketch, "E27.6.0.0", {"start": v(-57.15, -91.92) * mm, "end": v(-73.03, -85.15) * mm});
            skLineSegment(sketch, "E27.6.0.1", {"start": v(-73.03, -85.15) * mm, "end": v(-57.15, -78.4) * mm});
            skLineSegment(sketch, "E27.6.0.2", {"start": v(-57.15, -78.4) * mm, "end": v(-41.28, -85.15) * mm});
            skLineSegment(sketch, "E27.6.0.3", {"start": v(-41.28, -85.15) * mm, "end": v(-57.15, -91.92) * mm});
            skLineSegment(sketch, "E27.6.1.0", {"start": v(-57.15, -73) * mm, "end": v(-73.03, -66.23) * mm});
            skLineSegment(sketch, "E27.6.1.1", {"start": v(-73.03, -66.23) * mm, "end": v(-57.15, -59.47) * mm});
            skLineSegment(sketch, "E27.6.1.2", {"start": v(-57.15, -59.47) * mm, "end": v(-41.28, -66.23) * mm});
            skLineSegment(sketch, "E27.6.1.3", {"start": v(-41.28, -66.23) * mm, "end": v(-57.15, -73) * mm});
            skLineSegment(sketch, "E27.6.2.0", {"start": v(-57.15, -54.07) * mm, "end": v(-73.03, -47.3) * mm});
            skLineSegment(sketch, "E27.6.2.1", {"start": v(-73.03, -47.3) * mm, "end": v(-57.15, -40.54) * mm});
            skLineSegment(sketch, "E27.6.2.2", {"start": v(-57.15, -40.54) * mm, "end": v(-41.28, -47.3) * mm});
            skLineSegment(sketch, "E27.6.2.3", {"start": v(-41.28, -47.3) * mm, "end": v(-57.15, -54.07) * mm});
            skLineSegment(sketch, "E27.6.3.0", {"start": v(-57.15, -35.15) * mm, "end": v(-73.03, -28.38) * mm});
            skLineSegment(sketch, "E27.6.3.1", {"start": v(-73.03, -28.38) * mm, "end": v(-57.15, -21.62) * mm});
            skLineSegment(sketch, "E27.6.3.2", {"start": v(-57.15, -21.62) * mm, "end": v(-41.28, -28.38) * mm});
            skLineSegment(sketch, "E27.6.3.3", {"start": v(-41.28, -28.38) * mm, "end": v(-57.15, -35.15) * mm});
            skLineSegment(sketch, "E27.6.4.0", {"start": v(-57.15, -16.22) * mm, "end": v(-73.03, -9.46) * mm});
            skLineSegment(sketch, "E27.6.4.1", {"start": v(-73.03, -9.46) * mm, "end": v(-57.15, -2.7) * mm});
            skLineSegment(sketch, "E27.6.4.2", {"start": v(-57.15, -2.7) * mm, "end": v(-41.28, -9.46) * mm});
            skLineSegment(sketch, "E27.6.4.3", {"start": v(-41.28, -9.46) * mm, "end": v(-57.15, -16.22) * mm});
            skLineSegment(sketch, "E27.6.5.0", {"start": v(-57.15, 2.7) * mm, "end": v(-73.03, 9.46) * mm});
            skLineSegment(sketch, "E27.6.5.1", {"start": v(-73.03, 9.46) * mm, "end": v(-57.15, 16.22) * mm});
            skLineSegment(sketch, "E27.6.5.2", {"start": v(-57.15, 16.22) * mm, "end": v(-41.28, 9.46) * mm});
            skLineSegment(sketch, "E27.6.5.3", {"start": v(-41.28, 9.46) * mm, "end": v(-57.15, 2.7) * mm});
            skLineSegment(sketch, "E27.6.6.0", {"start": v(-57.15, 21.62) * mm, "end": v(-73.03, 28.38) * mm});
            skLineSegment(sketch, "E27.6.6.1", {"start": v(-73.03, 28.38) * mm, "end": v(-57.15, 35.15) * mm});
            skLineSegment(sketch, "E27.6.6.2", {"start": v(-57.15, 35.15) * mm, "end": v(-41.28, 28.38) * mm});
            skLineSegment(sketch, "E27.6.6.3", {"start": v(-41.28, 28.38) * mm, "end": v(-57.15, 21.62) * mm});
            skLineSegment(sketch, "E27.6.7.0", {"start": v(-57.15, 40.54) * mm, "end": v(-73.03, 47.3) * mm});
            skLineSegment(sketch, "E27.6.7.1", {"start": v(-73.03, 47.3) * mm, "end": v(-57.15, 54.07) * mm});
            skLineSegment(sketch, "E27.6.7.2", {"start": v(-57.15, 54.07) * mm, "end": v(-41.28, 47.3) * mm});
            skLineSegment(sketch, "E27.6.7.3", {"start": v(-41.28, 47.3) * mm, "end": v(-57.15, 40.54) * mm});
            skLineSegment(sketch, "E27.6.8.0", {"start": v(-57.15, 59.47) * mm, "end": v(-73.03, 66.23) * mm});
            skLineSegment(sketch, "E27.6.8.1", {"start": v(-73.03, 66.23) * mm, "end": v(-57.15, 73) * mm});
            skLineSegment(sketch, "E27.6.8.2", {"start": v(-57.15, 73) * mm, "end": v(-41.28, 66.23) * mm});
            skLineSegment(sketch, "E27.6.8.3", {"start": v(-41.28, 66.23) * mm, "end": v(-57.15, 59.47) * mm});
            skLineSegment(sketch, "E27.6.9.0", {"start": v(-57.15, 78.4) * mm, "end": v(-73.03, 85.15) * mm});
            skLineSegment(sketch, "E27.6.9.1", {"start": v(-73.03, 85.15) * mm, "end": v(-57.15, 91.92) * mm});
            skLineSegment(sketch, "E27.6.9.2", {"start": v(-57.15, 91.92) * mm, "end": v(-41.28, 85.15) * mm});
            skLineSegment(sketch, "E27.6.9.3", {"start": v(-41.28, 85.15) * mm, "end": v(-57.15, 78.4) * mm});
            skLineSegment(sketch, "E27.7.0.0", {"start": v(-95.25, -91.92) * mm, "end": v(-111.13, -85.15) * mm});
            skLineSegment(sketch, "E27.7.0.1", {"start": v(-111.13, -85.15) * mm, "end": v(-95.25, -78.4) * mm});
            skLineSegment(sketch, "E27.7.0.2", {"start": v(-95.25, -78.4) * mm, "end": v(-79.38, -85.15) * mm});
            skLineSegment(sketch, "E27.7.0.3", {"start": v(-79.38, -85.15) * mm, "end": v(-95.25, -91.92) * mm});
            skLineSegment(sketch, "E27.7.1.0", {"start": v(-95.25, -73) * mm, "end": v(-111.13, -66.23) * mm});
            skLineSegment(sketch, "E27.7.1.1", {"start": v(-111.13, -66.23) * mm, "end": v(-95.25, -59.47) * mm});
            skLineSegment(sketch, "E27.7.1.2", {"start": v(-95.25, -59.47) * mm, "end": v(-79.38, -66.23) * mm});
            skLineSegment(sketch, "E27.7.1.3", {"start": v(-79.38, -66.23) * mm, "end": v(-95.25, -73) * mm});
            skLineSegment(sketch, "E27.7.2.0", {"start": v(-95.25, -54.07) * mm, "end": v(-111.13, -47.3) * mm});
            skLineSegment(sketch, "E27.7.2.1", {"start": v(-111.13, -47.3) * mm, "end": v(-95.25, -40.54) * mm});
            skLineSegment(sketch, "E27.7.2.2", {"start": v(-95.25, -40.54) * mm, "end": v(-79.38, -47.3) * mm});
            skLineSegment(sketch, "E27.7.2.3", {"start": v(-79.38, -47.3) * mm, "end": v(-95.25, -54.07) * mm});
            skLineSegment(sketch, "E27.7.3.0", {"start": v(-95.25, -35.15) * mm, "end": v(-111.13, -28.38) * mm});
            skLineSegment(sketch, "E27.7.3.1", {"start": v(-111.13, -28.38) * mm, "end": v(-95.25, -21.62) * mm});
            skLineSegment(sketch, "E27.7.3.2", {"start": v(-95.25, -21.62) * mm, "end": v(-79.38, -28.38) * mm});
            skLineSegment(sketch, "E27.7.3.3", {"start": v(-79.38, -28.38) * mm, "end": v(-95.25, -35.15) * mm});
            skLineSegment(sketch, "E27.7.4.0", {"start": v(-95.25, -16.22) * mm, "end": v(-111.13, -9.46) * mm});
            skLineSegment(sketch, "E27.7.4.1", {"start": v(-111.13, -9.46) * mm, "end": v(-95.25, -2.7) * mm});
            skLineSegment(sketch, "E27.7.4.2", {"start": v(-95.25, -2.7) * mm, "end": v(-79.38, -9.46) * mm});
            skLineSegment(sketch, "E27.7.4.3", {"start": v(-79.38, -9.46) * mm, "end": v(-95.25, -16.22) * mm});
            skLineSegment(sketch, "E27.7.5.0", {"start": v(-95.25, 2.7) * mm, "end": v(-111.13, 9.46) * mm});
            skLineSegment(sketch, "E27.7.5.1", {"start": v(-111.13, 9.46) * mm, "end": v(-95.25, 16.22) * mm});
            skLineSegment(sketch, "E27.7.5.2", {"start": v(-95.25, 16.22) * mm, "end": v(-79.38, 9.46) * mm});
            skLineSegment(sketch, "E27.7.5.3", {"start": v(-79.38, 9.46) * mm, "end": v(-95.25, 2.7) * mm});
            skLineSegment(sketch, "E27.7.6.0", {"start": v(-95.25, 21.62) * mm, "end": v(-111.13, 28.38) * mm});
            skLineSegment(sketch, "E27.7.6.1", {"start": v(-111.13, 28.38) * mm, "end": v(-95.25, 35.15) * mm});
            skLineSegment(sketch, "E27.7.6.2", {"start": v(-95.25, 35.15) * mm, "end": v(-79.38, 28.38) * mm});
            skLineSegment(sketch, "E27.7.6.3", {"start": v(-79.38, 28.38) * mm, "end": v(-95.25, 21.62) * mm});
            skLineSegment(sketch, "E27.7.7.0", {"start": v(-95.25, 40.54) * mm, "end": v(-111.13, 47.3) * mm});
            skLineSegment(sketch, "E27.7.7.1", {"start": v(-111.13, 47.3) * mm, "end": v(-95.25, 54.07) * mm});
            skLineSegment(sketch, "E27.7.7.2", {"start": v(-95.25, 54.07) * mm, "end": v(-79.38, 47.3) * mm});
            skLineSegment(sketch, "E27.7.7.3", {"start": v(-79.38, 47.3) * mm, "end": v(-95.25, 40.54) * mm});
            skLineSegment(sketch, "E27.7.8.0", {"start": v(-95.25, 59.47) * mm, "end": v(-111.13, 66.23) * mm});
            skLineSegment(sketch, "E27.7.8.1", {"start": v(-111.13, 66.23) * mm, "end": v(-95.25, 73) * mm});
            skLineSegment(sketch, "E27.7.8.2", {"start": v(-95.25, 73) * mm, "end": v(-79.38, 66.23) * mm});
            skLineSegment(sketch, "E27.7.8.3", {"start": v(-79.38, 66.23) * mm, "end": v(-95.25, 59.47) * mm});
            skLineSegment(sketch, "E27.7.9.0", {"start": v(-95.25, 78.4) * mm, "end": v(-111.13, 85.15) * mm});
            skLineSegment(sketch, "E27.7.9.1", {"start": v(-111.13, 85.15) * mm, "end": v(-95.25, 91.92) * mm});
            skLineSegment(sketch, "E27.7.9.2", {"start": v(-95.25, 91.92) * mm, "end": v(-79.38, 85.15) * mm});
            skLineSegment(sketch, "E27.7.9.3", {"start": v(-79.38, 85.15) * mm, "end": v(-95.25, 78.4) * mm});
            skLineSegment(sketch, "E27.8.0.0", {"start": v(-133.35, -91.92) * mm, "end": v(-149.23, -85.15) * mm});
            skLineSegment(sketch, "E27.8.0.1", {"start": v(-149.23, -85.15) * mm, "end": v(-133.35, -78.4) * mm});
            skLineSegment(sketch, "E27.8.0.2", {"start": v(-133.35, -78.4) * mm, "end": v(-117.48, -85.15) * mm});
            skLineSegment(sketch, "E27.8.0.3", {"start": v(-117.48, -85.15) * mm, "end": v(-133.35, -91.92) * mm});
            skLineSegment(sketch, "E27.8.1.0", {"start": v(-133.35, -73) * mm, "end": v(-149.23, -66.23) * mm});
            skLineSegment(sketch, "E27.8.1.1", {"start": v(-149.23, -66.23) * mm, "end": v(-133.35, -59.47) * mm});
            skLineSegment(sketch, "E27.8.1.2", {"start": v(-133.35, -59.47) * mm, "end": v(-117.48, -66.23) * mm});
            skLineSegment(sketch, "E27.8.1.3", {"start": v(-117.48, -66.23) * mm, "end": v(-133.35, -73) * mm});
            skLineSegment(sketch, "E27.8.2.0", {"start": v(-133.35, -54.07) * mm, "end": v(-149.23, -47.3) * mm});
            skLineSegment(sketch, "E27.8.2.1", {"start": v(-149.23, -47.3) * mm, "end": v(-133.35, -40.54) * mm});
            skLineSegment(sketch, "E27.8.2.2", {"start": v(-133.35, -40.54) * mm, "end": v(-117.48, -47.3) * mm});
            skLineSegment(sketch, "E27.8.2.3", {"start": v(-117.48, -47.3) * mm, "end": v(-133.35, -54.07) * mm});
            skLineSegment(sketch, "E27.8.3.0", {"start": v(-133.35, -35.15) * mm, "end": v(-149.23, -28.38) * mm});
            skLineSegment(sketch, "E27.8.3.1", {"start": v(-149.23, -28.38) * mm, "end": v(-133.35, -21.62) * mm});
            skLineSegment(sketch, "E27.8.3.2", {"start": v(-133.35, -21.62) * mm, "end": v(-117.48, -28.38) * mm});
            skLineSegment(sketch, "E27.8.3.3", {"start": v(-117.48, -28.38) * mm, "end": v(-133.35, -35.15) * mm});
            skLineSegment(sketch, "E27.8.4.0", {"start": v(-133.35, -16.22) * mm, "end": v(-149.23, -9.46) * mm});
            skLineSegment(sketch, "E27.8.4.1", {"start": v(-149.23, -9.46) * mm, "end": v(-133.35, -2.7) * mm});
            skLineSegment(sketch, "E27.8.4.2", {"start": v(-133.35, -2.7) * mm, "end": v(-117.48, -9.46) * mm});
            skLineSegment(sketch, "E27.8.4.3", {"start": v(-117.48, -9.46) * mm, "end": v(-133.35, -16.22) * mm});
            skLineSegment(sketch, "E27.8.5.0", {"start": v(-133.35, 2.7) * mm, "end": v(-149.23, 9.46) * mm});
            skLineSegment(sketch, "E27.8.5.1", {"start": v(-149.23, 9.46) * mm, "end": v(-133.35, 16.22) * mm});
            skLineSegment(sketch, "E27.8.5.2", {"start": v(-133.35, 16.22) * mm, "end": v(-117.48, 9.46) * mm});
            skLineSegment(sketch, "E27.8.5.3", {"start": v(-117.48, 9.46) * mm, "end": v(-133.35, 2.7) * mm});
            skLineSegment(sketch, "E27.8.6.0", {"start": v(-133.35, 21.62) * mm, "end": v(-149.23, 28.38) * mm});
            skLineSegment(sketch, "E27.8.6.1", {"start": v(-149.23, 28.38) * mm, "end": v(-133.35, 35.15) * mm});
            skLineSegment(sketch, "E27.8.6.2", {"start": v(-133.35, 35.15) * mm, "end": v(-117.48, 28.38) * mm});
            skLineSegment(sketch, "E27.8.6.3", {"start": v(-117.48, 28.38) * mm, "end": v(-133.35, 21.62) * mm});
            skLineSegment(sketch, "E27.8.7.0", {"start": v(-133.35, 40.54) * mm, "end": v(-149.23, 47.3) * mm});
            skLineSegment(sketch, "E27.8.7.1", {"start": v(-149.23, 47.3) * mm, "end": v(-133.35, 54.07) * mm});
            skLineSegment(sketch, "E27.8.7.2", {"start": v(-133.35, 54.07) * mm, "end": v(-117.48, 47.3) * mm});
            skLineSegment(sketch, "E27.8.7.3", {"start": v(-117.48, 47.3) * mm, "end": v(-133.35, 40.54) * mm});
            skLineSegment(sketch, "E27.8.8.0", {"start": v(-133.35, 59.47) * mm, "end": v(-149.23, 66.23) * mm});
            skLineSegment(sketch, "E27.8.8.1", {"start": v(-149.23, 66.23) * mm, "end": v(-133.35, 73) * mm});
            skLineSegment(sketch, "E27.8.8.2", {"start": v(-133.35, 73) * mm, "end": v(-117.48, 66.23) * mm});
            skLineSegment(sketch, "E27.8.8.3", {"start": v(-117.48, 66.23) * mm, "end": v(-133.35, 59.47) * mm});
            skLineSegment(sketch, "E27.8.9.0", {"start": v(-133.35, 78.4) * mm, "end": v(-149.23, 85.15) * mm});
            skLineSegment(sketch, "E27.8.9.1", {"start": v(-149.23, 85.15) * mm, "end": v(-133.35, 91.92) * mm});
            skLineSegment(sketch, "E27.8.9.2", {"start": v(-133.35, 91.92) * mm, "end": v(-117.48, 85.15) * mm});
            skLineSegment(sketch, "E27.8.9.3", {"start": v(-117.48, 85.15) * mm, "end": v(-133.35, 78.4) * mm});
            skLineSegment(sketch, "E27.9.0.0", {"start": v(-171.45, -91.92) * mm, "end": v(-187.33, -85.15) * mm});
            skLineSegment(sketch, "E27.9.0.1", {"start": v(-187.33, -85.15) * mm, "end": v(-171.45, -78.4) * mm});
            skLineSegment(sketch, "E27.9.0.2", {"start": v(-171.45, -78.4) * mm, "end": v(-155.58, -85.15) * mm});
            skLineSegment(sketch, "E27.9.0.3", {"start": v(-155.58, -85.15) * mm, "end": v(-171.45, -91.92) * mm});
            skLineSegment(sketch, "E27.9.1.0", {"start": v(-171.45, -73) * mm, "end": v(-187.33, -66.23) * mm});
            skLineSegment(sketch, "E27.9.1.1", {"start": v(-187.33, -66.23) * mm, "end": v(-171.45, -59.47) * mm});
            skLineSegment(sketch, "E27.9.1.2", {"start": v(-171.45, -59.47) * mm, "end": v(-155.58, -66.23) * mm});
            skLineSegment(sketch, "E27.9.1.3", {"start": v(-155.58, -66.23) * mm, "end": v(-171.45, -73) * mm});
            skLineSegment(sketch, "E27.9.2.0", {"start": v(-171.45, -54.07) * mm, "end": v(-187.33, -47.3) * mm});
            skLineSegment(sketch, "E27.9.2.1", {"start": v(-187.33, -47.3) * mm, "end": v(-171.45, -40.54) * mm});
            skLineSegment(sketch, "E27.9.2.2", {"start": v(-171.45, -40.54) * mm, "end": v(-155.58, -47.3) * mm});
            skLineSegment(sketch, "E27.9.2.3", {"start": v(-155.58, -47.3) * mm, "end": v(-171.45, -54.07) * mm});
            skLineSegment(sketch, "E27.9.3.0", {"start": v(-171.45, -35.15) * mm, "end": v(-187.33, -28.38) * mm});
            skLineSegment(sketch, "E27.9.3.1", {"start": v(-187.33, -28.38) * mm, "end": v(-171.45, -21.62) * mm});
            skLineSegment(sketch, "E27.9.3.2", {"start": v(-171.45, -21.62) * mm, "end": v(-155.58, -28.38) * mm});
            skLineSegment(sketch, "E27.9.3.3", {"start": v(-155.58, -28.38) * mm, "end": v(-171.45, -35.15) * mm});
            skLineSegment(sketch, "E27.9.4.0", {"start": v(-171.45, -16.22) * mm, "end": v(-187.33, -9.46) * mm});
            skLineSegment(sketch, "E27.9.4.1", {"start": v(-187.33, -9.46) * mm, "end": v(-171.45, -2.7) * mm});
            skLineSegment(sketch, "E27.9.4.2", {"start": v(-171.45, -2.7) * mm, "end": v(-155.58, -9.46) * mm});
            skLineSegment(sketch, "E27.9.4.3", {"start": v(-155.58, -9.46) * mm, "end": v(-171.45, -16.22) * mm});
            skLineSegment(sketch, "E27.9.5.0", {"start": v(-171.45, 2.7) * mm, "end": v(-187.33, 9.46) * mm});
            skLineSegment(sketch, "E27.9.5.1", {"start": v(-187.33, 9.46) * mm, "end": v(-171.45, 16.22) * mm});
            skLineSegment(sketch, "E27.9.5.2", {"start": v(-171.45, 16.22) * mm, "end": v(-155.58, 9.46) * mm});
            skLineSegment(sketch, "E27.9.5.3", {"start": v(-155.58, 9.46) * mm, "end": v(-171.45, 2.7) * mm});
            skLineSegment(sketch, "E27.9.6.0", {"start": v(-171.45, 21.62) * mm, "end": v(-187.33, 28.38) * mm});
            skLineSegment(sketch, "E27.9.6.1", {"start": v(-187.33, 28.38) * mm, "end": v(-171.45, 35.15) * mm});
            skLineSegment(sketch, "E27.9.6.2", {"start": v(-171.45, 35.15) * mm, "end": v(-155.58, 28.38) * mm});
            skLineSegment(sketch, "E27.9.6.3", {"start": v(-155.58, 28.38) * mm, "end": v(-171.45, 21.62) * mm});
            skLineSegment(sketch, "E27.9.7.0", {"start": v(-171.45, 40.54) * mm, "end": v(-187.33, 47.3) * mm});
            skLineSegment(sketch, "E27.9.7.1", {"start": v(-187.33, 47.3) * mm, "end": v(-171.45, 54.07) * mm});
            skLineSegment(sketch, "E27.9.7.2", {"start": v(-171.45, 54.07) * mm, "end": v(-155.58, 47.3) * mm});
            skLineSegment(sketch, "E27.9.7.3", {"start": v(-155.58, 47.3) * mm, "end": v(-171.45, 40.54) * mm});
            skLineSegment(sketch, "E27.9.8.0", {"start": v(-171.45, 59.47) * mm, "end": v(-187.33, 66.23) * mm});
            skLineSegment(sketch, "E27.9.8.1", {"start": v(-187.33, 66.23) * mm, "end": v(-171.45, 73) * mm});
            skLineSegment(sketch, "E27.9.8.2", {"start": v(-171.45, 73) * mm, "end": v(-155.58, 66.23) * mm});
            skLineSegment(sketch, "E27.9.8.3", {"start": v(-155.58, 66.23) * mm, "end": v(-171.45, 59.47) * mm});
            skLineSegment(sketch, "E27.9.9.0", {"start": v(-171.45, 78.4) * mm, "end": v(-187.33, 85.15) * mm});
            skLineSegment(sketch, "E27.9.9.1", {"start": v(-187.33, 85.15) * mm, "end": v(-171.45, 91.92) * mm});
            skLineSegment(sketch, "E27.9.9.2", {"start": v(-171.45, 91.92) * mm, "end": v(-155.58, 85.15) * mm});
            skLineSegment(sketch, "E27.9.9.3", {"start": v(-155.58, 85.15) * mm, "end": v(-171.45, 78.4) * mm});
            skLineSegment(sketch, "E27.direction1", {"start": v(155.57, -85.15) * mm, "end": v(117.47, -85.15) * mm, "construction": true});
            skLineSegment(sketch, "E27.direction2", {"start": v(155.57, -85.15) * mm, "end": v(155.57, -66.23) * mm, "construction": true});
            skSolve(sketch);
        }
        {
            var Q0;
            Q0 = qSketchRegion(id + "F6", true);
            extrude(context, id + "F7", {"entities" : qUnion([Q0]), "operationType" : NewBodyOperationType.REMOVE, "oppositeDirection" : true, "depth" : 25.4 * mm});
        }
        {
            var Q0;
            Q0=makeQuery(id+"F1.opExtrude","SWEPT_FACE",FACE,{"disambiguationData":[OSD([sQuery(id+"F0.wireOp",EDGE,"E13.MirrorCS")])]});
            var sketch = newSketch(context, id + "F8", { "sketchPlane" : qUnion([Q0])});
            skLineSegment(sketch, "E28", {"start": v(-191.77, 26.55) * mm, "end": v(191.77, -108.93) * mm, "construction": true});
            skLineSegment(sketch, "E29", {"start": v(191.77, 26.55) * mm, "end": v(0, -41.2) * mm, "construction": true});
            skLineSegment(sketch, "E30", {"start": v(0, -34.43) * mm, "end": v(-15.88, -41.2) * mm});
            skLineSegment(sketch, "E31", {"start": v(-15.87, -41.2) * mm, "end": v(0, -47.95) * mm});
            skLineSegment(sketch, "E32", {"start": v(0, -47.95) * mm, "end": v(15.87, -41.2) * mm});
            skLineSegment(sketch, "E33", {"start": v(15.87, -41.2) * mm, "end": v(0, -34.43) * mm});
            skLineSegment(sketch, "E34.0.1.0", {"start": v(15.87, -22.27) * mm, "end": v(0, -15.5) * mm});
            skLineSegment(sketch, "E34.0.1.1", {"start": v(0, -29.03) * mm, "end": v(15.87, -22.27) * mm});
            skLineSegment(sketch, "E34.0.1.2", {"start": v(-15.88, -22.27) * mm, "end": v(0, -29.03) * mm});
            skLineSegment(sketch, "E34.0.1.3", {"start": v(0, -15.5) * mm, "end": v(-15.88, -22.27) * mm});
            skLineSegment(sketch, "E34.0.2.0", {"start": v(15.87, -3.34) * mm, "end": v(0, 3.42) * mm});
            skLineSegment(sketch, "E34.0.2.1", {"start": v(0, -10.1) * mm, "end": v(15.87, -3.34) * mm});
            skLineSegment(sketch, "E34.0.2.2", {"start": v(-15.88, -3.34) * mm, "end": v(0, -10.1) * mm});
            skLineSegment(sketch, "E34.0.2.3", {"start": v(0, 3.42) * mm, "end": v(-15.88, -3.34) * mm});
            skLineSegment(sketch, "E34.0.3.0", {"start": v(15.87, 15.58) * mm, "end": v(0, 22.34) * mm});
            skLineSegment(sketch, "E34.0.3.1", {"start": v(0, 8.82) * mm, "end": v(15.87, 15.58) * mm});
            skLineSegment(sketch, "E34.0.3.2", {"start": v(-15.88, 15.58) * mm, "end": v(0, 8.82) * mm});
            skLineSegment(sketch, "E34.0.3.3", {"start": v(0, 22.34) * mm, "end": v(-15.88, 15.58) * mm});
            skLineSegment(sketch, "E34.1.0.0", {"start": v(53.97, -41.2) * mm, "end": v(38.1, -34.43) * mm});
            skLineSegment(sketch, "E34.1.0.1", {"start": v(38.1, -47.95) * mm, "end": v(53.97, -41.2) * mm});
            skLineSegment(sketch, "E34.1.0.2", {"start": v(22.22, -41.2) * mm, "end": v(38.1, -47.95) * mm});
            skLineSegment(sketch, "E34.1.0.3", {"start": v(38.1, -34.43) * mm, "end": v(22.23, -41.2) * mm});
            skLineSegment(sketch, "E34.1.1.0", {"start": v(53.97, -22.27) * mm, "end": v(38.1, -15.5) * mm});
            skLineSegment(sketch, "E34.1.1.1", {"start": v(38.1, -29.03) * mm, "end": v(53.97, -22.27) * mm});
            skLineSegment(sketch, "E34.1.1.2", {"start": v(22.22, -22.27) * mm, "end": v(38.1, -29.03) * mm});
            skLineSegment(sketch, "E34.1.1.3", {"start": v(38.1, -15.5) * mm, "end": v(22.23, -22.27) * mm});
            skLineSegment(sketch, "E34.1.2.0", {"start": v(53.97, -3.34) * mm, "end": v(38.1, 3.42) * mm});
            skLineSegment(sketch, "E34.1.2.1", {"start": v(38.1, -10.1) * mm, "end": v(53.97, -3.34) * mm});
            skLineSegment(sketch, "E34.1.2.2", {"start": v(22.22, -3.34) * mm, "end": v(38.1, -10.1) * mm});
            skLineSegment(sketch, "E34.1.2.3", {"start": v(38.1, 3.42) * mm, "end": v(22.23, -3.34) * mm});
            skLineSegment(sketch, "E34.1.3.0", {"start": v(53.97, 15.58) * mm, "end": v(38.1, 22.34) * mm});
            skLineSegment(sketch, "E34.1.3.1", {"start": v(38.1, 8.82) * mm, "end": v(53.97, 15.58) * mm});
            skLineSegment(sketch, "E34.1.3.2", {"start": v(22.22, 15.58) * mm, "end": v(38.1, 8.82) * mm});
            skLineSegment(sketch, "E34.1.3.3", {"start": v(38.1, 22.34) * mm, "end": v(22.23, 15.58) * mm});
            skLineSegment(sketch, "E34.2.0.0", {"start": v(92.07, -41.2) * mm, "end": v(76.2, -34.43) * mm});
            skLineSegment(sketch, "E34.2.0.1", {"start": v(76.2, -47.95) * mm, "end": v(92.08, -41.2) * mm});
            skLineSegment(sketch, "E34.2.0.2", {"start": v(60.32, -41.2) * mm, "end": v(76.2, -47.95) * mm});
            skLineSegment(sketch, "E34.2.0.3", {"start": v(76.2, -34.43) * mm, "end": v(60.32, -41.2) * mm});
            skLineSegment(sketch, "E34.2.1.0", {"start": v(92.07, -22.27) * mm, "end": v(76.2, -15.5) * mm});
            skLineSegment(sketch, "E34.2.1.1", {"start": v(76.2, -29.03) * mm, "end": v(92.08, -22.27) * mm});
            skLineSegment(sketch, "E34.2.1.2", {"start": v(60.32, -22.27) * mm, "end": v(76.2, -29.03) * mm});
            skLineSegment(sketch, "E34.2.1.3", {"start": v(76.2, -15.5) * mm, "end": v(60.32, -22.27) * mm});
            skLineSegment(sketch, "E34.2.2.0", {"start": v(92.07, -3.34) * mm, "end": v(76.2, 3.42) * mm});
            skLineSegment(sketch, "E34.2.2.1", {"start": v(76.2, -10.1) * mm, "end": v(92.08, -3.34) * mm});
            skLineSegment(sketch, "E34.2.2.2", {"start": v(60.32, -3.34) * mm, "end": v(76.2, -10.1) * mm});
            skLineSegment(sketch, "E34.2.2.3", {"start": v(76.2, 3.42) * mm, "end": v(60.32, -3.34) * mm});
            skLineSegment(sketch, "E34.2.3.0", {"start": v(92.07, 15.58) * mm, "end": v(76.2, 22.34) * mm});
            skLineSegment(sketch, "E34.2.3.1", {"start": v(76.2, 8.82) * mm, "end": v(92.08, 15.58) * mm});
            skLineSegment(sketch, "E34.2.3.2", {"start": v(60.32, 15.58) * mm, "end": v(76.2, 8.82) * mm});
            skLineSegment(sketch, "E34.2.3.3", {"start": v(76.2, 22.34) * mm, "end": v(60.32, 15.58) * mm});
            skLineSegment(sketch, "E34.3.0.0", {"start": v(130.17, -41.2) * mm, "end": v(114.3, -34.43) * mm});
            skLineSegment(sketch, "E34.3.0.1", {"start": v(114.3, -47.95) * mm, "end": v(130.18, -41.2) * mm});
            skLineSegment(sketch, "E34.3.0.2", {"start": v(98.43, -41.2) * mm, "end": v(114.3, -47.95) * mm});
            skLineSegment(sketch, "E34.3.0.3", {"start": v(114.3, -34.43) * mm, "end": v(98.42, -41.2) * mm});
            skLineSegment(sketch, "E34.3.1.0", {"start": v(130.17, -22.27) * mm, "end": v(114.3, -15.5) * mm});
            skLineSegment(sketch, "E34.3.1.1", {"start": v(114.3, -29.03) * mm, "end": v(130.18, -22.27) * mm});
            skLineSegment(sketch, "E34.3.1.2", {"start": v(98.43, -22.27) * mm, "end": v(114.3, -29.03) * mm});
            skLineSegment(sketch, "E34.3.1.3", {"start": v(114.3, -15.5) * mm, "end": v(98.42, -22.27) * mm});
            skLineSegment(sketch, "E34.3.2.0", {"start": v(130.17, -3.34) * mm, "end": v(114.3, 3.42) * mm});
            skLineSegment(sketch, "E34.3.2.1", {"start": v(114.3, -10.1) * mm, "end": v(130.18, -3.34) * mm});
            skLineSegment(sketch, "E34.3.2.2", {"start": v(98.43, -3.34) * mm, "end": v(114.3, -10.1) * mm});
            skLineSegment(sketch, "E34.3.2.3", {"start": v(114.3, 3.42) * mm, "end": v(98.42, -3.34) * mm});
            skLineSegment(sketch, "E34.3.3.0", {"start": v(130.17, 15.58) * mm, "end": v(114.3, 22.34) * mm});
            skLineSegment(sketch, "E34.3.3.1", {"start": v(114.3, 8.82) * mm, "end": v(130.18, 15.58) * mm});
            skLineSegment(sketch, "E34.3.3.2", {"start": v(98.43, 15.58) * mm, "end": v(114.3, 8.82) * mm});
            skLineSegment(sketch, "E34.3.3.3", {"start": v(114.3, 22.34) * mm, "end": v(98.42, 15.58) * mm});
            skLineSegment(sketch, "E34.4.0.0", {"start": v(168.28, -41.2) * mm, "end": v(152.4, -34.43) * mm});
            skLineSegment(sketch, "E34.4.0.1", {"start": v(152.4, -47.95) * mm, "end": v(168.28, -41.2) * mm});
            skLineSegment(sketch, "E34.4.0.2", {"start": v(136.53, -41.2) * mm, "end": v(152.4, -47.95) * mm});
            skLineSegment(sketch, "E34.4.0.3", {"start": v(152.4, -34.43) * mm, "end": v(136.53, -41.2) * mm});
            skLineSegment(sketch, "E34.4.1.0", {"start": v(168.28, -22.27) * mm, "end": v(152.4, -15.5) * mm});
            skLineSegment(sketch, "E34.4.1.1", {"start": v(152.4, -29.03) * mm, "end": v(168.28, -22.27) * mm});
            skLineSegment(sketch, "E34.4.1.2", {"start": v(136.53, -22.27) * mm, "end": v(152.4, -29.03) * mm});
            skLineSegment(sketch, "E34.4.1.3", {"start": v(152.4, -15.5) * mm, "end": v(136.53, -22.27) * mm});
            skLineSegment(sketch, "E34.4.2.0", {"start": v(168.28, -3.34) * mm, "end": v(152.4, 3.42) * mm});
            skLineSegment(sketch, "E34.4.2.1", {"start": v(152.4, -10.1) * mm, "end": v(168.28, -3.34) * mm});
            skLineSegment(sketch, "E34.4.2.2", {"start": v(136.53, -3.34) * mm, "end": v(152.4, -10.1) * mm});
            skLineSegment(sketch, "E34.4.2.3", {"start": v(152.4, 3.42) * mm, "end": v(136.53, -3.34) * mm});
            skLineSegment(sketch, "E34.4.3.0", {"start": v(168.28, 15.58) * mm, "end": v(152.4, 22.34) * mm});
            skLineSegment(sketch, "E34.4.3.1", {"start": v(152.4, 8.82) * mm, "end": v(168.28, 15.58) * mm});
            skLineSegment(sketch, "E34.4.3.2", {"start": v(136.53, 15.58) * mm, "end": v(152.4, 8.82) * mm});
            skLineSegment(sketch, "E34.4.3.3", {"start": v(152.4, 22.34) * mm, "end": v(136.53, 15.58) * mm});
            skLineSegment(sketch, "E34.direction1", {"start": v(-15.88, -41.2) * mm, "end": v(22.22, -41.2) * mm, "construction": true});
            skLineSegment(sketch, "E34.direction2", {"start": v(-15.88, -41.2) * mm, "end": v(-15.88, -22.27) * mm, "construction": true});
            skLineSegment(sketch, "E35.0.1.0", {"start": v(0, -53.35) * mm, "end": v(-15.88, -60.11) * mm});
            skLineSegment(sketch, "E35.0.1.1", {"start": v(-15.88, -60.11) * mm, "end": v(0, -66.88) * mm});
            skLineSegment(sketch, "E35.0.1.2", {"start": v(0, -66.88) * mm, "end": v(15.87, -60.11) * mm});
            skLineSegment(sketch, "E35.0.1.3", {"start": v(15.87, -60.11) * mm, "end": v(0, -53.35) * mm});
            skLineSegment(sketch, "E35.0.1.4", {"start": v(168.28, -60.11) * mm, "end": v(152.4, -53.35) * mm});
            skLineSegment(sketch, "E35.0.1.5", {"start": v(130.17, -60.11) * mm, "end": v(114.3, -53.35) * mm});
            skLineSegment(sketch, "E35.0.1.6", {"start": v(92.07, -60.11) * mm, "end": v(76.2, -53.35) * mm});
            skLineSegment(sketch, "E35.0.1.7", {"start": v(53.97, -60.11) * mm, "end": v(38.1, -53.35) * mm});
            skLineSegment(sketch, "E35.0.1.8", {"start": v(152.4, -66.88) * mm, "end": v(168.28, -60.11) * mm});
            skLineSegment(sketch, "E35.0.1.9", {"start": v(114.3, -66.88) * mm, "end": v(130.18, -60.11) * mm});
            skLineSegment(sketch, "E35.0.1.10", {"start": v(76.2, -66.88) * mm, "end": v(92.08, -60.11) * mm});
            skLineSegment(sketch, "E35.0.1.11", {"start": v(38.1, -66.88) * mm, "end": v(53.97, -60.11) * mm});
            skLineSegment(sketch, "E35.0.1.12", {"start": v(136.53, -60.11) * mm, "end": v(152.4, -66.88) * mm});
            skLineSegment(sketch, "E35.0.1.13", {"start": v(98.43, -60.11) * mm, "end": v(114.3, -66.88) * mm});
            skLineSegment(sketch, "E35.0.1.14", {"start": v(60.32, -60.11) * mm, "end": v(76.2, -66.88) * mm});
            skLineSegment(sketch, "E35.0.1.15", {"start": v(22.22, -60.11) * mm, "end": v(38.1, -66.88) * mm});
            skLineSegment(sketch, "E35.0.1.16", {"start": v(152.4, -53.35) * mm, "end": v(136.53, -60.11) * mm});
            skLineSegment(sketch, "E35.0.1.17", {"start": v(114.3, -53.35) * mm, "end": v(98.42, -60.11) * mm});
            skLineSegment(sketch, "E35.0.1.18", {"start": v(76.2, -53.35) * mm, "end": v(60.32, -60.11) * mm});
            skLineSegment(sketch, "E35.0.1.19", {"start": v(38.1, -53.35) * mm, "end": v(22.23, -60.11) * mm});
            skLineSegment(sketch, "E35.0.2.0", {"start": v(0, -72.27) * mm, "end": v(-15.88, -79.04) * mm});
            skLineSegment(sketch, "E35.0.2.1", {"start": v(-15.88, -79.04) * mm, "end": v(0, -85.8) * mm});
            skLineSegment(sketch, "E35.0.2.2", {"start": v(0, -85.8) * mm, "end": v(15.87, -79.04) * mm});
            skLineSegment(sketch, "E35.0.2.3", {"start": v(15.87, -79.04) * mm, "end": v(0, -72.27) * mm});
            skLineSegment(sketch, "E35.0.2.4", {"start": v(168.28, -79.04) * mm, "end": v(152.4, -72.27) * mm});
            skLineSegment(sketch, "E35.0.2.5", {"start": v(130.17, -79.04) * mm, "end": v(114.3, -72.27) * mm});
            skLineSegment(sketch, "E35.0.2.6", {"start": v(92.07, -79.04) * mm, "end": v(76.2, -72.27) * mm});
            skLineSegment(sketch, "E35.0.2.7", {"start": v(53.97, -79.04) * mm, "end": v(38.1, -72.27) * mm});
            skLineSegment(sketch, "E35.0.2.8", {"start": v(152.4, -85.8) * mm, "end": v(168.28, -79.04) * mm});
            skLineSegment(sketch, "E35.0.2.9", {"start": v(114.3, -85.8) * mm, "end": v(130.18, -79.04) * mm});
            skLineSegment(sketch, "E35.0.2.10", {"start": v(76.2, -85.8) * mm, "end": v(92.08, -79.04) * mm});
            skLineSegment(sketch, "E35.0.2.11", {"start": v(38.1, -85.8) * mm, "end": v(53.97, -79.04) * mm});
            skLineSegment(sketch, "E35.0.2.12", {"start": v(136.53, -79.04) * mm, "end": v(152.4, -85.8) * mm});
            skLineSegment(sketch, "E35.0.2.13", {"start": v(98.43, -79.04) * mm, "end": v(114.3, -85.8) * mm});
            skLineSegment(sketch, "E35.0.2.14", {"start": v(60.32, -79.04) * mm, "end": v(76.2, -85.8) * mm});
            skLineSegment(sketch, "E35.0.2.15", {"start": v(22.22, -79.04) * mm, "end": v(38.1, -85.8) * mm});
            skLineSegment(sketch, "E35.0.2.16", {"start": v(152.4, -72.27) * mm, "end": v(136.53, -79.04) * mm});
            skLineSegment(sketch, "E35.0.2.17", {"start": v(114.3, -72.27) * mm, "end": v(98.42, -79.04) * mm});
            skLineSegment(sketch, "E35.0.2.18", {"start": v(76.2, -72.27) * mm, "end": v(60.32, -79.04) * mm});
            skLineSegment(sketch, "E35.0.2.19", {"start": v(38.1, -72.27) * mm, "end": v(22.23, -79.04) * mm});
            skLineSegment(sketch, "E35.0.3.0", {"start": v(0, -91.2) * mm, "end": v(-15.88, -97.96) * mm});
            skLineSegment(sketch, "E35.0.3.1", {"start": v(-15.88, -97.96) * mm, "end": v(0, -104.72) * mm});
            skLineSegment(sketch, "E35.0.3.2", {"start": v(0, -104.72) * mm, "end": v(15.87, -97.96) * mm});
            skLineSegment(sketch, "E35.0.3.3", {"start": v(15.87, -97.96) * mm, "end": v(0, -91.2) * mm});
            skLineSegment(sketch, "E35.0.3.4", {"start": v(168.28, -97.96) * mm, "end": v(152.4, -91.2) * mm});
            skLineSegment(sketch, "E35.0.3.5", {"start": v(130.17, -97.96) * mm, "end": v(114.3, -91.2) * mm});
            skLineSegment(sketch, "E35.0.3.6", {"start": v(92.07, -97.96) * mm, "end": v(76.2, -91.2) * mm});
            skLineSegment(sketch, "E35.0.3.7", {"start": v(53.97, -97.96) * mm, "end": v(38.1, -91.2) * mm});
            skLineSegment(sketch, "E35.0.3.8", {"start": v(152.4, -104.72) * mm, "end": v(168.28, -97.96) * mm});
            skLineSegment(sketch, "E35.0.3.9", {"start": v(114.3, -104.72) * mm, "end": v(130.18, -97.96) * mm});
            skLineSegment(sketch, "E35.0.3.10", {"start": v(76.2, -104.72) * mm, "end": v(92.08, -97.96) * mm});
            skLineSegment(sketch, "E35.0.3.11", {"start": v(38.1, -104.72) * mm, "end": v(53.97, -97.96) * mm});
            skLineSegment(sketch, "E35.0.3.12", {"start": v(136.53, -97.96) * mm, "end": v(152.4, -104.72) * mm});
            skLineSegment(sketch, "E35.0.3.13", {"start": v(98.43, -97.96) * mm, "end": v(114.3, -104.72) * mm});
            skLineSegment(sketch, "E35.0.3.14", {"start": v(60.32, -97.96) * mm, "end": v(76.2, -104.72) * mm});
            skLineSegment(sketch, "E35.0.3.15", {"start": v(22.22, -97.96) * mm, "end": v(38.1, -104.72) * mm});
            skLineSegment(sketch, "E35.0.3.16", {"start": v(152.4, -91.2) * mm, "end": v(136.53, -97.96) * mm});
            skLineSegment(sketch, "E35.0.3.17", {"start": v(114.3, -91.2) * mm, "end": v(98.42, -97.96) * mm});
            skLineSegment(sketch, "E35.0.3.18", {"start": v(76.2, -91.2) * mm, "end": v(60.32, -97.96) * mm});
            skLineSegment(sketch, "E35.0.3.19", {"start": v(38.1, -91.2) * mm, "end": v(22.23, -97.96) * mm});
            skLineSegment(sketch, "E35.direction1", {"start": v(-15.88, -41.2) * mm, "end": v(9.52, -41.2) * mm, "construction": true});
            skLineSegment(sketch, "E35.direction2", {"start": v(-15.88, -41.2) * mm, "end": v(-15.88, -60.11) * mm, "construction": true});
            skLineSegment(sketch, "E36.1.0.0", {"start": v(-38.1, -72.27) * mm, "end": v(-53.98, -79.04) * mm});
            skLineSegment(sketch, "E36.1.0.1", {"start": v(-22.23, -60.11) * mm, "end": v(-38.1, -53.35) * mm});
            skLineSegment(sketch, "E36.1.0.2", {"start": v(-38.1, -66.88) * mm, "end": v(-22.23, -60.11) * mm});
            skLineSegment(sketch, "E36.1.0.3", {"start": v(-53.98, -60.11) * mm, "end": v(-38.1, -66.88) * mm});
            skLineSegment(sketch, "E36.1.0.4", {"start": v(-53.98, -3.34) * mm, "end": v(-38.1, -10.1) * mm});
            skLineSegment(sketch, "E36.1.0.5", {"start": v(-38.1, -10.1) * mm, "end": v(-22.23, -3.34) * mm});
            skLineSegment(sketch, "E36.1.0.6", {"start": v(-22.23, -3.34) * mm, "end": v(-38.1, 3.42) * mm});
            skLineSegment(sketch, "E36.1.0.7", {"start": v(-38.1, -15.5) * mm, "end": v(-53.98, -22.27) * mm});
            skLineSegment(sketch, "E36.1.0.8", {"start": v(-53.98, -22.27) * mm, "end": v(-38.1, -29.03) * mm});
            skLineSegment(sketch, "E36.1.0.9", {"start": v(-38.1, -29.03) * mm, "end": v(-22.23, -22.27) * mm});
            skLineSegment(sketch, "E36.1.0.10", {"start": v(-38.1, -53.35) * mm, "end": v(-53.98, -60.11) * mm});
            skLineSegment(sketch, "E36.1.0.11", {"start": v(-22.23, -22.27) * mm, "end": v(-38.1, -15.5) * mm});
            skLineSegment(sketch, "E36.1.0.12", {"start": v(-22.23, -41.2) * mm, "end": v(-38.1, -34.43) * mm});
            skLineSegment(sketch, "E36.1.0.13", {"start": v(-38.1, -47.95) * mm, "end": v(-22.23, -41.2) * mm});
            skLineSegment(sketch, "E36.1.0.14", {"start": v(-53.98, -41.2) * mm, "end": v(-38.1, -47.95) * mm});
            skLineSegment(sketch, "E36.1.0.15", {"start": v(-38.1, -34.43) * mm, "end": v(-53.98, -41.2) * mm});
            skLineSegment(sketch, "E36.1.0.16", {"start": v(-38.1, 8.82) * mm, "end": v(-22.23, 15.58) * mm});
            skLineSegment(sketch, "E36.1.0.17", {"start": v(-22.23, 15.58) * mm, "end": v(-38.1, 22.34) * mm});
            skLineSegment(sketch, "E36.1.0.18", {"start": v(-38.1, 3.42) * mm, "end": v(-53.98, -3.34) * mm});
            skLineSegment(sketch, "E36.1.0.19", {"start": v(-38.1, 22.34) * mm, "end": v(-53.98, 15.58) * mm});
            skLineSegment(sketch, "E36.1.0.20", {"start": v(-53.98, -79.04) * mm, "end": v(-38.1, -85.8) * mm});
            skLineSegment(sketch, "E36.1.0.21", {"start": v(-38.1, -85.8) * mm, "end": v(-22.23, -79.04) * mm});
            skLineSegment(sketch, "E36.1.0.22", {"start": v(-22.23, -79.04) * mm, "end": v(-38.1, -72.27) * mm});
            skLineSegment(sketch, "E36.1.0.23", {"start": v(-53.98, -97.96) * mm, "end": v(-38.1, -104.72) * mm});
            skLineSegment(sketch, "E36.1.0.24", {"start": v(-38.1, -91.2) * mm, "end": v(-53.98, -97.96) * mm});
            skLineSegment(sketch, "E36.1.0.25", {"start": v(-38.1, -104.72) * mm, "end": v(-22.23, -97.96) * mm});
            skLineSegment(sketch, "E36.1.0.26", {"start": v(-22.23, -97.96) * mm, "end": v(-38.1, -91.2) * mm});
            skLineSegment(sketch, "E36.1.0.27", {"start": v(-53.98, 15.58) * mm, "end": v(-38.1, 8.82) * mm});
            skLineSegment(sketch, "E36.2.0.0", {"start": v(-76.2, -72.27) * mm, "end": v(-92.08, -79.04) * mm});
            skLineSegment(sketch, "E36.2.0.1", {"start": v(-60.33, -60.11) * mm, "end": v(-76.2, -53.35) * mm});
            skLineSegment(sketch, "E36.2.0.2", {"start": v(-76.2, -66.88) * mm, "end": v(-60.33, -60.11) * mm});
            skLineSegment(sketch, "E36.2.0.3", {"start": v(-92.08, -60.11) * mm, "end": v(-76.2, -66.88) * mm});
            skLineSegment(sketch, "E36.2.0.4", {"start": v(-92.08, -3.34) * mm, "end": v(-76.2, -10.1) * mm});
            skLineSegment(sketch, "E36.2.0.5", {"start": v(-76.2, -10.1) * mm, "end": v(-60.33, -3.34) * mm});
            skLineSegment(sketch, "E36.2.0.6", {"start": v(-60.33, -3.34) * mm, "end": v(-76.2, 3.42) * mm});
            skLineSegment(sketch, "E36.2.0.7", {"start": v(-76.2, -15.5) * mm, "end": v(-92.08, -22.27) * mm});
            skLineSegment(sketch, "E36.2.0.8", {"start": v(-92.08, -22.27) * mm, "end": v(-76.2, -29.03) * mm});
            skLineSegment(sketch, "E36.2.0.9", {"start": v(-76.2, -29.03) * mm, "end": v(-60.33, -22.27) * mm});
            skLineSegment(sketch, "E36.2.0.10", {"start": v(-76.2, -53.35) * mm, "end": v(-92.08, -60.11) * mm});
            skLineSegment(sketch, "E36.2.0.11", {"start": v(-60.33, -22.27) * mm, "end": v(-76.2, -15.5) * mm});
            skLineSegment(sketch, "E36.2.0.12", {"start": v(-60.33, -41.2) * mm, "end": v(-76.2, -34.43) * mm});
            skLineSegment(sketch, "E36.2.0.13", {"start": v(-76.2, -47.95) * mm, "end": v(-60.33, -41.2) * mm});
            skLineSegment(sketch, "E36.2.0.14", {"start": v(-92.08, -41.2) * mm, "end": v(-76.2, -47.95) * mm});
            skLineSegment(sketch, "E36.2.0.15", {"start": v(-76.2, -34.43) * mm, "end": v(-92.08, -41.2) * mm});
            skLineSegment(sketch, "E36.2.0.16", {"start": v(-76.2, 8.82) * mm, "end": v(-60.33, 15.58) * mm});
            skLineSegment(sketch, "E36.2.0.17", {"start": v(-60.33, 15.58) * mm, "end": v(-76.2, 22.34) * mm});
            skLineSegment(sketch, "E36.2.0.18", {"start": v(-76.2, 3.42) * mm, "end": v(-92.08, -3.34) * mm});
            skLineSegment(sketch, "E36.2.0.19", {"start": v(-76.2, 22.34) * mm, "end": v(-92.08, 15.58) * mm});
            skLineSegment(sketch, "E36.2.0.20", {"start": v(-92.08, -79.04) * mm, "end": v(-76.2, -85.8) * mm});
            skLineSegment(sketch, "E36.2.0.21", {"start": v(-76.2, -85.8) * mm, "end": v(-60.33, -79.04) * mm});
            skLineSegment(sketch, "E36.2.0.22", {"start": v(-60.33, -79.04) * mm, "end": v(-76.2, -72.27) * mm});
            skLineSegment(sketch, "E36.2.0.23", {"start": v(-92.08, -97.96) * mm, "end": v(-76.2, -104.72) * mm});
            skLineSegment(sketch, "E36.2.0.24", {"start": v(-76.2, -91.2) * mm, "end": v(-92.08, -97.96) * mm});
            skLineSegment(sketch, "E36.2.0.25", {"start": v(-76.2, -104.72) * mm, "end": v(-60.33, -97.96) * mm});
            skLineSegment(sketch, "E36.2.0.26", {"start": v(-60.33, -97.96) * mm, "end": v(-76.2, -91.2) * mm});
            skLineSegment(sketch, "E36.2.0.27", {"start": v(-92.08, 15.58) * mm, "end": v(-76.2, 8.82) * mm});
            skLineSegment(sketch, "E36.3.0.0", {"start": v(-114.3, -72.27) * mm, "end": v(-130.18, -79.04) * mm});
            skLineSegment(sketch, "E36.3.0.1", {"start": v(-98.43, -60.11) * mm, "end": v(-114.3, -53.35) * mm});
            skLineSegment(sketch, "E36.3.0.2", {"start": v(-114.3, -66.88) * mm, "end": v(-98.43, -60.11) * mm});
            skLineSegment(sketch, "E36.3.0.3", {"start": v(-130.18, -60.11) * mm, "end": v(-114.3, -66.88) * mm});
            skLineSegment(sketch, "E36.3.0.4", {"start": v(-130.18, -3.34) * mm, "end": v(-114.3, -10.1) * mm});
            skLineSegment(sketch, "E36.3.0.5", {"start": v(-114.3, -10.1) * mm, "end": v(-98.43, -3.34) * mm});
            skLineSegment(sketch, "E36.3.0.6", {"start": v(-98.43, -3.34) * mm, "end": v(-114.3, 3.42) * mm});
            skLineSegment(sketch, "E36.3.0.7", {"start": v(-114.3, -15.5) * mm, "end": v(-130.18, -22.27) * mm});
            skLineSegment(sketch, "E36.3.0.8", {"start": v(-130.18, -22.27) * mm, "end": v(-114.3, -29.03) * mm});
            skLineSegment(sketch, "E36.3.0.9", {"start": v(-114.3, -29.03) * mm, "end": v(-98.43, -22.27) * mm});
            skLineSegment(sketch, "E36.3.0.10", {"start": v(-114.3, -53.35) * mm, "end": v(-130.18, -60.11) * mm});
            skLineSegment(sketch, "E36.3.0.11", {"start": v(-98.43, -22.27) * mm, "end": v(-114.3, -15.5) * mm});
            skLineSegment(sketch, "E36.3.0.12", {"start": v(-98.43, -41.2) * mm, "end": v(-114.3, -34.43) * mm});
            skLineSegment(sketch, "E36.3.0.13", {"start": v(-114.3, -47.95) * mm, "end": v(-98.43, -41.2) * mm});
            skLineSegment(sketch, "E36.3.0.14", {"start": v(-130.18, -41.2) * mm, "end": v(-114.3, -47.95) * mm});
            skLineSegment(sketch, "E36.3.0.15", {"start": v(-114.3, -34.43) * mm, "end": v(-130.18, -41.2) * mm});
            skLineSegment(sketch, "E36.3.0.16", {"start": v(-114.3, 8.82) * mm, "end": v(-98.43, 15.58) * mm});
            skLineSegment(sketch, "E36.3.0.17", {"start": v(-98.43, 15.58) * mm, "end": v(-114.3, 22.34) * mm});
            skLineSegment(sketch, "E36.3.0.18", {"start": v(-114.3, 3.42) * mm, "end": v(-130.18, -3.34) * mm});
            skLineSegment(sketch, "E36.3.0.19", {"start": v(-114.3, 22.34) * mm, "end": v(-130.18, 15.58) * mm});
            skLineSegment(sketch, "E36.3.0.20", {"start": v(-130.18, -79.04) * mm, "end": v(-114.3, -85.8) * mm});
            skLineSegment(sketch, "E36.3.0.21", {"start": v(-114.3, -85.8) * mm, "end": v(-98.43, -79.04) * mm});
            skLineSegment(sketch, "E36.3.0.22", {"start": v(-98.43, -79.04) * mm, "end": v(-114.3, -72.27) * mm});
            skLineSegment(sketch, "E36.3.0.23", {"start": v(-130.18, -97.96) * mm, "end": v(-114.3, -104.72) * mm});
            skLineSegment(sketch, "E36.3.0.24", {"start": v(-114.3, -91.2) * mm, "end": v(-130.18, -97.96) * mm});
            skLineSegment(sketch, "E36.3.0.25", {"start": v(-114.3, -104.72) * mm, "end": v(-98.43, -97.96) * mm});
            skLineSegment(sketch, "E36.3.0.26", {"start": v(-98.43, -97.96) * mm, "end": v(-114.3, -91.2) * mm});
            skLineSegment(sketch, "E36.3.0.27", {"start": v(-130.18, 15.58) * mm, "end": v(-114.3, 8.82) * mm});
            skLineSegment(sketch, "E36.4.0.0", {"start": v(-152.4, -72.27) * mm, "end": v(-168.28, -79.04) * mm});
            skLineSegment(sketch, "E36.4.0.1", {"start": v(-136.53, -60.11) * mm, "end": v(-152.4, -53.35) * mm});
            skLineSegment(sketch, "E36.4.0.2", {"start": v(-152.4, -66.88) * mm, "end": v(-136.53, -60.11) * mm});
            skLineSegment(sketch, "E36.4.0.3", {"start": v(-168.28, -60.11) * mm, "end": v(-152.4, -66.88) * mm});
            skLineSegment(sketch, "E36.4.0.4", {"start": v(-168.28, -3.34) * mm, "end": v(-152.4, -10.1) * mm});
            skLineSegment(sketch, "E36.4.0.5", {"start": v(-152.4, -10.1) * mm, "end": v(-136.53, -3.34) * mm});
            skLineSegment(sketch, "E36.4.0.6", {"start": v(-136.53, -3.34) * mm, "end": v(-152.4, 3.42) * mm});
            skLineSegment(sketch, "E36.4.0.7", {"start": v(-152.4, -15.5) * mm, "end": v(-168.28, -22.27) * mm});
            skLineSegment(sketch, "E36.4.0.8", {"start": v(-168.28, -22.27) * mm, "end": v(-152.4, -29.03) * mm});
            skLineSegment(sketch, "E36.4.0.9", {"start": v(-152.4, -29.03) * mm, "end": v(-136.53, -22.27) * mm});
            skLineSegment(sketch, "E36.4.0.10", {"start": v(-152.4, -53.35) * mm, "end": v(-168.28, -60.11) * mm});
            skLineSegment(sketch, "E36.4.0.11", {"start": v(-136.53, -22.27) * mm, "end": v(-152.4, -15.5) * mm});
            skLineSegment(sketch, "E36.4.0.12", {"start": v(-136.53, -41.2) * mm, "end": v(-152.4, -34.43) * mm});
            skLineSegment(sketch, "E36.4.0.13", {"start": v(-152.4, -47.95) * mm, "end": v(-136.53, -41.2) * mm});
            skLineSegment(sketch, "E36.4.0.14", {"start": v(-168.28, -41.2) * mm, "end": v(-152.4, -47.95) * mm});
            skLineSegment(sketch, "E36.4.0.15", {"start": v(-152.4, -34.43) * mm, "end": v(-168.28, -41.2) * mm});
            skLineSegment(sketch, "E36.4.0.16", {"start": v(-152.4, 8.82) * mm, "end": v(-136.53, 15.58) * mm});
            skLineSegment(sketch, "E36.4.0.17", {"start": v(-136.53, 15.58) * mm, "end": v(-152.4, 22.34) * mm});
            skLineSegment(sketch, "E36.4.0.18", {"start": v(-152.4, 3.42) * mm, "end": v(-168.28, -3.34) * mm});
            skLineSegment(sketch, "E36.4.0.19", {"start": v(-152.4, 22.34) * mm, "end": v(-168.28, 15.58) * mm});
            skLineSegment(sketch, "E36.4.0.20", {"start": v(-168.28, -79.04) * mm, "end": v(-152.4, -85.8) * mm});
            skLineSegment(sketch, "E36.4.0.21", {"start": v(-152.4, -85.8) * mm, "end": v(-136.53, -79.04) * mm});
            skLineSegment(sketch, "E36.4.0.22", {"start": v(-136.53, -79.04) * mm, "end": v(-152.4, -72.27) * mm});
            skLineSegment(sketch, "E36.4.0.23", {"start": v(-168.28, -97.96) * mm, "end": v(-152.4, -104.72) * mm});
            skLineSegment(sketch, "E36.4.0.24", {"start": v(-152.4, -91.2) * mm, "end": v(-168.28, -97.96) * mm});
            skLineSegment(sketch, "E36.4.0.25", {"start": v(-152.4, -104.72) * mm, "end": v(-136.53, -97.96) * mm});
            skLineSegment(sketch, "E36.4.0.26", {"start": v(-136.53, -97.96) * mm, "end": v(-152.4, -91.2) * mm});
            skLineSegment(sketch, "E36.4.0.27", {"start": v(-168.28, 15.58) * mm, "end": v(-152.4, 8.82) * mm});
            skLineSegment(sketch, "E36.direction1", {"start": v(-15.88, -97.96) * mm, "end": v(-53.98, -97.96) * mm, "construction": true});
            skLineSegment(sketch, "E37", {"start": v(155.57, -88.5) * mm, "end": v(171.45, -81.73) * mm});
            skLineSegment(sketch, "E38", {"start": v(171.45, -81.73) * mm, "end": v(187.32, -88.5) * mm});
            skLineSegment(sketch, "E39", {"start": v(187.32, -88.5) * mm, "end": v(171.45, -95.26) * mm});
            skLineSegment(sketch, "E40", {"start": v(171.45, -95.26) * mm, "end": v(155.57, -88.5) * mm});
            skLineSegment(sketch, "E41.0.1.0", {"start": v(171.45, -76.34) * mm, "end": v(155.57, -69.57) * mm});
            skLineSegment(sketch, "E41.0.1.1", {"start": v(187.32, -69.57) * mm, "end": v(171.45, -76.34) * mm});
            skLineSegment(sketch, "E41.0.1.2", {"start": v(171.45, -62.81) * mm, "end": v(187.32, -69.57) * mm});
            skLineSegment(sketch, "E41.0.1.3", {"start": v(155.57, -69.57) * mm, "end": v(171.45, -62.81) * mm});
            skLineSegment(sketch, "E41.0.2.0", {"start": v(171.45, -57.41) * mm, "end": v(155.57, -50.65) * mm});
            skLineSegment(sketch, "E41.0.2.1", {"start": v(187.32, -50.65) * mm, "end": v(171.45, -57.41) * mm});
            skLineSegment(sketch, "E41.0.2.2", {"start": v(171.45, -43.89) * mm, "end": v(187.32, -50.65) * mm});
            skLineSegment(sketch, "E41.0.2.3", {"start": v(155.57, -50.65) * mm, "end": v(171.45, -43.89) * mm});
            skLineSegment(sketch, "E41.0.3.0", {"start": v(171.45, -38.5) * mm, "end": v(155.57, -31.73) * mm});
            skLineSegment(sketch, "E41.0.3.1", {"start": v(187.32, -31.73) * mm, "end": v(171.45, -38.5) * mm});
            skLineSegment(sketch, "E41.0.3.2", {"start": v(171.45, -24.97) * mm, "end": v(187.32, -31.73) * mm});
            skLineSegment(sketch, "E41.0.3.3", {"start": v(155.57, -31.73) * mm, "end": v(171.45, -24.97) * mm});
            skLineSegment(sketch, "E41.0.4.0", {"start": v(171.45, -19.57) * mm, "end": v(155.57, -12.8) * mm});
            skLineSegment(sketch, "E41.0.4.1", {"start": v(187.32, -12.8) * mm, "end": v(171.45, -19.57) * mm});
            skLineSegment(sketch, "E41.0.4.2", {"start": v(171.45, -6.04) * mm, "end": v(187.32, -12.8) * mm});
            skLineSegment(sketch, "E41.0.4.3", {"start": v(155.57, -12.8) * mm, "end": v(171.45, -6.04) * mm});
            skLineSegment(sketch, "E41.0.5.0", {"start": v(171.45, -0.65) * mm, "end": v(155.57, 6.12) * mm});
            skLineSegment(sketch, "E41.0.5.1", {"start": v(187.32, 6.12) * mm, "end": v(171.45, -0.65) * mm});
            skLineSegment(sketch, "E41.0.5.2", {"start": v(171.45, 12.88) * mm, "end": v(187.32, 6.12) * mm});
            skLineSegment(sketch, "E41.0.5.3", {"start": v(155.57, 6.12) * mm, "end": v(171.45, 12.88) * mm});
            skLineSegment(sketch, "E41.1.0.0", {"start": v(133.35, -95.26) * mm, "end": v(117.47, -88.5) * mm});
            skLineSegment(sketch, "E41.1.0.1", {"start": v(149.22, -88.5) * mm, "end": v(133.35, -95.26) * mm});
            skLineSegment(sketch, "E41.1.0.2", {"start": v(133.35, -81.73) * mm, "end": v(149.22, -88.5) * mm});
            skLineSegment(sketch, "E41.1.0.3", {"start": v(117.47, -88.5) * mm, "end": v(133.35, -81.73) * mm});
            skLineSegment(sketch, "E41.1.1.0", {"start": v(133.35, -76.34) * mm, "end": v(117.47, -69.57) * mm});
            skLineSegment(sketch, "E41.1.1.1", {"start": v(149.22, -69.57) * mm, "end": v(133.35, -76.34) * mm});
            skLineSegment(sketch, "E41.1.1.2", {"start": v(133.35, -62.81) * mm, "end": v(149.22, -69.57) * mm});
            skLineSegment(sketch, "E41.1.1.3", {"start": v(117.47, -69.57) * mm, "end": v(133.35, -62.81) * mm});
            skLineSegment(sketch, "E41.1.2.0", {"start": v(133.35, -57.41) * mm, "end": v(117.47, -50.65) * mm});
            skLineSegment(sketch, "E41.1.2.1", {"start": v(149.22, -50.65) * mm, "end": v(133.35, -57.41) * mm});
            skLineSegment(sketch, "E41.1.2.2", {"start": v(133.35, -43.89) * mm, "end": v(149.22, -50.65) * mm});
            skLineSegment(sketch, "E41.1.2.3", {"start": v(117.47, -50.65) * mm, "end": v(133.35, -43.89) * mm});
            skLineSegment(sketch, "E41.1.3.0", {"start": v(133.35, -38.5) * mm, "end": v(117.47, -31.73) * mm});
            skLineSegment(sketch, "E41.1.3.1", {"start": v(149.22, -31.73) * mm, "end": v(133.35, -38.5) * mm});
            skLineSegment(sketch, "E41.1.3.2", {"start": v(133.35, -24.97) * mm, "end": v(149.22, -31.73) * mm});
            skLineSegment(sketch, "E41.1.3.3", {"start": v(117.47, -31.73) * mm, "end": v(133.35, -24.97) * mm});
            skLineSegment(sketch, "E41.1.4.0", {"start": v(133.35, -19.57) * mm, "end": v(117.47, -12.8) * mm});
            skLineSegment(sketch, "E41.1.4.1", {"start": v(149.22, -12.8) * mm, "end": v(133.35, -19.57) * mm});
            skLineSegment(sketch, "E41.1.4.2", {"start": v(133.35, -6.04) * mm, "end": v(149.22, -12.8) * mm});
            skLineSegment(sketch, "E41.1.4.3", {"start": v(117.47, -12.8) * mm, "end": v(133.35, -6.04) * mm});
            skLineSegment(sketch, "E41.1.5.0", {"start": v(133.35, -0.65) * mm, "end": v(117.47, 6.12) * mm});
            skLineSegment(sketch, "E41.1.5.1", {"start": v(149.22, 6.12) * mm, "end": v(133.35, -0.65) * mm});
            skLineSegment(sketch, "E41.1.5.2", {"start": v(133.35, 12.88) * mm, "end": v(149.22, 6.12) * mm});
            skLineSegment(sketch, "E41.1.5.3", {"start": v(117.47, 6.12) * mm, "end": v(133.35, 12.88) * mm});
            skLineSegment(sketch, "E41.2.0.0", {"start": v(95.25, -95.26) * mm, "end": v(79.37, -88.5) * mm});
            skLineSegment(sketch, "E41.2.0.1", {"start": v(111.12, -88.5) * mm, "end": v(95.25, -95.26) * mm});
            skLineSegment(sketch, "E41.2.0.2", {"start": v(95.25, -81.73) * mm, "end": v(111.12, -88.5) * mm});
            skLineSegment(sketch, "E41.2.0.3", {"start": v(79.37, -88.5) * mm, "end": v(95.25, -81.73) * mm});
            skLineSegment(sketch, "E41.2.1.0", {"start": v(95.25, -76.34) * mm, "end": v(79.37, -69.57) * mm});
            skLineSegment(sketch, "E41.2.1.1", {"start": v(111.12, -69.57) * mm, "end": v(95.25, -76.34) * mm});
            skLineSegment(sketch, "E41.2.1.2", {"start": v(95.25, -62.81) * mm, "end": v(111.12, -69.57) * mm});
            skLineSegment(sketch, "E41.2.1.3", {"start": v(79.37, -69.57) * mm, "end": v(95.25, -62.81) * mm});
            skLineSegment(sketch, "E41.2.2.0", {"start": v(95.25, -57.41) * mm, "end": v(79.37, -50.65) * mm});
            skLineSegment(sketch, "E41.2.2.1", {"start": v(111.12, -50.65) * mm, "end": v(95.25, -57.41) * mm});
            skLineSegment(sketch, "E41.2.2.2", {"start": v(95.25, -43.89) * mm, "end": v(111.12, -50.65) * mm});
            skLineSegment(sketch, "E41.2.2.3", {"start": v(79.37, -50.65) * mm, "end": v(95.25, -43.89) * mm});
            skLineSegment(sketch, "E41.2.3.0", {"start": v(95.25, -38.5) * mm, "end": v(79.37, -31.73) * mm});
            skLineSegment(sketch, "E41.2.3.1", {"start": v(111.12, -31.73) * mm, "end": v(95.25, -38.5) * mm});
            skLineSegment(sketch, "E41.2.3.2", {"start": v(95.25, -24.97) * mm, "end": v(111.12, -31.73) * mm});
            skLineSegment(sketch, "E41.2.3.3", {"start": v(79.37, -31.73) * mm, "end": v(95.25, -24.97) * mm});
            skLineSegment(sketch, "E41.2.4.0", {"start": v(95.25, -19.57) * mm, "end": v(79.37, -12.8) * mm});
            skLineSegment(sketch, "E41.2.4.1", {"start": v(111.12, -12.8) * mm, "end": v(95.25, -19.57) * mm});
            skLineSegment(sketch, "E41.2.4.2", {"start": v(95.25, -6.04) * mm, "end": v(111.12, -12.8) * mm});
            skLineSegment(sketch, "E41.2.4.3", {"start": v(79.37, -12.8) * mm, "end": v(95.25, -6.04) * mm});
            skLineSegment(sketch, "E41.2.5.0", {"start": v(95.25, -0.65) * mm, "end": v(79.37, 6.12) * mm});
            skLineSegment(sketch, "E41.2.5.1", {"start": v(111.12, 6.12) * mm, "end": v(95.25, -0.65) * mm});
            skLineSegment(sketch, "E41.2.5.2", {"start": v(95.25, 12.88) * mm, "end": v(111.12, 6.12) * mm});
            skLineSegment(sketch, "E41.2.5.3", {"start": v(79.37, 6.12) * mm, "end": v(95.25, 12.88) * mm});
            skLineSegment(sketch, "E41.3.0.0", {"start": v(57.15, -95.26) * mm, "end": v(41.27, -88.5) * mm});
            skLineSegment(sketch, "E41.3.0.1", {"start": v(73.02, -88.5) * mm, "end": v(57.15, -95.26) * mm});
            skLineSegment(sketch, "E41.3.0.2", {"start": v(57.15, -81.73) * mm, "end": v(73.02, -88.5) * mm});
            skLineSegment(sketch, "E41.3.0.3", {"start": v(41.27, -88.5) * mm, "end": v(57.15, -81.73) * mm});
            skLineSegment(sketch, "E41.3.1.0", {"start": v(57.15, -76.34) * mm, "end": v(41.27, -69.57) * mm});
            skLineSegment(sketch, "E41.3.1.1", {"start": v(73.02, -69.57) * mm, "end": v(57.15, -76.34) * mm});
            skLineSegment(sketch, "E41.3.1.2", {"start": v(57.15, -62.81) * mm, "end": v(73.02, -69.57) * mm});
            skLineSegment(sketch, "E41.3.1.3", {"start": v(41.27, -69.57) * mm, "end": v(57.15, -62.81) * mm});
            skLineSegment(sketch, "E41.3.2.0", {"start": v(57.15, -57.41) * mm, "end": v(41.27, -50.65) * mm});
            skLineSegment(sketch, "E41.3.2.1", {"start": v(73.02, -50.65) * mm, "end": v(57.15, -57.41) * mm});
            skLineSegment(sketch, "E41.3.2.2", {"start": v(57.15, -43.89) * mm, "end": v(73.02, -50.65) * mm});
            skLineSegment(sketch, "E41.3.2.3", {"start": v(41.27, -50.65) * mm, "end": v(57.15, -43.89) * mm});
            skLineSegment(sketch, "E41.3.3.0", {"start": v(57.15, -38.5) * mm, "end": v(41.27, -31.73) * mm});
            skLineSegment(sketch, "E41.3.3.1", {"start": v(73.02, -31.73) * mm, "end": v(57.15, -38.5) * mm});
            skLineSegment(sketch, "E41.3.3.2", {"start": v(57.15, -24.97) * mm, "end": v(73.02, -31.73) * mm});
            skLineSegment(sketch, "E41.3.3.3", {"start": v(41.27, -31.73) * mm, "end": v(57.15, -24.97) * mm});
            skLineSegment(sketch, "E41.3.4.0", {"start": v(57.15, -19.57) * mm, "end": v(41.27, -12.8) * mm});
            skLineSegment(sketch, "E41.3.4.1", {"start": v(73.02, -12.8) * mm, "end": v(57.15, -19.57) * mm});
            skLineSegment(sketch, "E41.3.4.2", {"start": v(57.15, -6.04) * mm, "end": v(73.02, -12.8) * mm});
            skLineSegment(sketch, "E41.3.4.3", {"start": v(41.27, -12.8) * mm, "end": v(57.15, -6.04) * mm});
            skLineSegment(sketch, "E41.3.5.0", {"start": v(57.15, -0.65) * mm, "end": v(41.27, 6.12) * mm});
            skLineSegment(sketch, "E41.3.5.1", {"start": v(73.02, 6.12) * mm, "end": v(57.15, -0.65) * mm});
            skLineSegment(sketch, "E41.3.5.2", {"start": v(57.15, 12.88) * mm, "end": v(73.02, 6.12) * mm});
            skLineSegment(sketch, "E41.3.5.3", {"start": v(41.27, 6.12) * mm, "end": v(57.15, 12.88) * mm});
            skLineSegment(sketch, "E41.4.0.0", {"start": v(19.05, -95.26) * mm, "end": v(3.17, -88.5) * mm});
            skLineSegment(sketch, "E41.4.0.1", {"start": v(34.92, -88.5) * mm, "end": v(19.05, -95.26) * mm});
            skLineSegment(sketch, "E41.4.0.2", {"start": v(19.05, -81.73) * mm, "end": v(34.92, -88.5) * mm});
            skLineSegment(sketch, "E41.4.0.3", {"start": v(3.17, -88.5) * mm, "end": v(19.05, -81.73) * mm});
            skLineSegment(sketch, "E41.4.1.0", {"start": v(19.05, -76.34) * mm, "end": v(3.17, -69.57) * mm});
            skLineSegment(sketch, "E41.4.1.1", {"start": v(34.92, -69.57) * mm, "end": v(19.05, -76.34) * mm});
            skLineSegment(sketch, "E41.4.1.2", {"start": v(19.05, -62.81) * mm, "end": v(34.92, -69.57) * mm});
            skLineSegment(sketch, "E41.4.1.3", {"start": v(3.17, -69.57) * mm, "end": v(19.05, -62.81) * mm});
            skLineSegment(sketch, "E41.4.2.0", {"start": v(19.05, -57.41) * mm, "end": v(3.17, -50.65) * mm});
            skLineSegment(sketch, "E41.4.2.1", {"start": v(34.92, -50.65) * mm, "end": v(19.05, -57.41) * mm});
            skLineSegment(sketch, "E41.4.2.2", {"start": v(19.05, -43.89) * mm, "end": v(34.92, -50.65) * mm});
            skLineSegment(sketch, "E41.4.2.3", {"start": v(3.17, -50.65) * mm, "end": v(19.05, -43.89) * mm});
            skLineSegment(sketch, "E41.4.3.0", {"start": v(19.05, -38.5) * mm, "end": v(3.17, -31.73) * mm});
            skLineSegment(sketch, "E41.4.3.1", {"start": v(34.92, -31.73) * mm, "end": v(19.05, -38.5) * mm});
            skLineSegment(sketch, "E41.4.3.2", {"start": v(19.05, -24.97) * mm, "end": v(34.92, -31.73) * mm});
            skLineSegment(sketch, "E41.4.3.3", {"start": v(3.17, -31.73) * mm, "end": v(19.05, -24.97) * mm});
            skLineSegment(sketch, "E41.4.4.0", {"start": v(19.05, -19.57) * mm, "end": v(3.17, -12.8) * mm});
            skLineSegment(sketch, "E41.4.4.1", {"start": v(34.92, -12.8) * mm, "end": v(19.05, -19.57) * mm});
            skLineSegment(sketch, "E41.4.4.2", {"start": v(19.05, -6.04) * mm, "end": v(34.92, -12.8) * mm});
            skLineSegment(sketch, "E41.4.4.3", {"start": v(3.17, -12.8) * mm, "end": v(19.05, -6.04) * mm});
            skLineSegment(sketch, "E41.4.5.0", {"start": v(19.05, -0.65) * mm, "end": v(3.17, 6.12) * mm});
            skLineSegment(sketch, "E41.4.5.1", {"start": v(34.92, 6.12) * mm, "end": v(19.05, -0.65) * mm});
            skLineSegment(sketch, "E41.4.5.2", {"start": v(19.05, 12.88) * mm, "end": v(34.92, 6.12) * mm});
            skLineSegment(sketch, "E41.4.5.3", {"start": v(3.17, 6.12) * mm, "end": v(19.05, 12.88) * mm});
            skLineSegment(sketch, "E41.5.0.0", {"start": v(-19.05, -95.26) * mm, "end": v(-34.93, -88.5) * mm});
            skLineSegment(sketch, "E41.5.0.1", {"start": v(-3.18, -88.5) * mm, "end": v(-19.05, -95.26) * mm});
            skLineSegment(sketch, "E41.5.0.2", {"start": v(-19.05, -81.73) * mm, "end": v(-3.18, -88.5) * mm});
            skLineSegment(sketch, "E41.5.0.3", {"start": v(-34.93, -88.5) * mm, "end": v(-19.05, -81.73) * mm});
            skLineSegment(sketch, "E41.5.1.0", {"start": v(-19.05, -76.34) * mm, "end": v(-34.93, -69.57) * mm});
            skLineSegment(sketch, "E41.5.1.1", {"start": v(-3.18, -69.57) * mm, "end": v(-19.05, -76.34) * mm});
            skLineSegment(sketch, "E41.5.1.2", {"start": v(-19.05, -62.81) * mm, "end": v(-3.18, -69.57) * mm});
            skLineSegment(sketch, "E41.5.1.3", {"start": v(-34.93, -69.57) * mm, "end": v(-19.05, -62.81) * mm});
            skLineSegment(sketch, "E41.5.2.0", {"start": v(-19.05, -57.41) * mm, "end": v(-34.93, -50.65) * mm});
            skLineSegment(sketch, "E41.5.2.1", {"start": v(-3.18, -50.65) * mm, "end": v(-19.05, -57.41) * mm});
            skLineSegment(sketch, "E41.5.2.2", {"start": v(-19.05, -43.89) * mm, "end": v(-3.18, -50.65) * mm});
            skLineSegment(sketch, "E41.5.2.3", {"start": v(-34.93, -50.65) * mm, "end": v(-19.05, -43.89) * mm});
            skLineSegment(sketch, "E41.5.3.0", {"start": v(-19.05, -38.5) * mm, "end": v(-34.93, -31.73) * mm});
            skLineSegment(sketch, "E41.5.3.1", {"start": v(-3.18, -31.73) * mm, "end": v(-19.05, -38.5) * mm});
            skLineSegment(sketch, "E41.5.3.2", {"start": v(-19.05, -24.97) * mm, "end": v(-3.18, -31.73) * mm});
            skLineSegment(sketch, "E41.5.3.3", {"start": v(-34.93, -31.73) * mm, "end": v(-19.05, -24.97) * mm});
            skLineSegment(sketch, "E41.5.4.0", {"start": v(-19.05, -19.57) * mm, "end": v(-34.93, -12.8) * mm});
            skLineSegment(sketch, "E41.5.4.1", {"start": v(-3.18, -12.8) * mm, "end": v(-19.05, -19.57) * mm});
            skLineSegment(sketch, "E41.5.4.2", {"start": v(-19.05, -6.04) * mm, "end": v(-3.18, -12.8) * mm});
            skLineSegment(sketch, "E41.5.4.3", {"start": v(-34.93, -12.8) * mm, "end": v(-19.05, -6.04) * mm});
            skLineSegment(sketch, "E41.5.5.0", {"start": v(-19.05, -0.65) * mm, "end": v(-34.93, 6.12) * mm});
            skLineSegment(sketch, "E41.5.5.1", {"start": v(-3.18, 6.12) * mm, "end": v(-19.05, -0.65) * mm});
            skLineSegment(sketch, "E41.5.5.2", {"start": v(-19.05, 12.88) * mm, "end": v(-3.18, 6.12) * mm});
            skLineSegment(sketch, "E41.5.5.3", {"start": v(-34.93, 6.12) * mm, "end": v(-19.05, 12.88) * mm});
            skLineSegment(sketch, "E41.6.0.0", {"start": v(-57.15, -95.26) * mm, "end": v(-73.03, -88.5) * mm});
            skLineSegment(sketch, "E41.6.0.1", {"start": v(-41.28, -88.5) * mm, "end": v(-57.15, -95.26) * mm});
            skLineSegment(sketch, "E41.6.0.2", {"start": v(-57.15, -81.73) * mm, "end": v(-41.28, -88.5) * mm});
            skLineSegment(sketch, "E41.6.0.3", {"start": v(-73.03, -88.5) * mm, "end": v(-57.15, -81.73) * mm});
            skLineSegment(sketch, "E41.6.1.0", {"start": v(-57.15, -76.34) * mm, "end": v(-73.03, -69.57) * mm});
            skLineSegment(sketch, "E41.6.1.1", {"start": v(-41.28, -69.57) * mm, "end": v(-57.15, -76.34) * mm});
            skLineSegment(sketch, "E41.6.1.2", {"start": v(-57.15, -62.81) * mm, "end": v(-41.28, -69.57) * mm});
            skLineSegment(sketch, "E41.6.1.3", {"start": v(-73.03, -69.57) * mm, "end": v(-57.15, -62.81) * mm});
            skLineSegment(sketch, "E41.6.2.0", {"start": v(-57.15, -57.41) * mm, "end": v(-73.03, -50.65) * mm});
            skLineSegment(sketch, "E41.6.2.1", {"start": v(-41.28, -50.65) * mm, "end": v(-57.15, -57.41) * mm});
            skLineSegment(sketch, "E41.6.2.2", {"start": v(-57.15, -43.89) * mm, "end": v(-41.28, -50.65) * mm});
            skLineSegment(sketch, "E41.6.2.3", {"start": v(-73.03, -50.65) * mm, "end": v(-57.15, -43.89) * mm});
            skLineSegment(sketch, "E41.6.3.0", {"start": v(-57.15, -38.5) * mm, "end": v(-73.03, -31.73) * mm});
            skLineSegment(sketch, "E41.6.3.1", {"start": v(-41.28, -31.73) * mm, "end": v(-57.15, -38.5) * mm});
            skLineSegment(sketch, "E41.6.3.2", {"start": v(-57.15, -24.97) * mm, "end": v(-41.28, -31.73) * mm});
            skLineSegment(sketch, "E41.6.3.3", {"start": v(-73.03, -31.73) * mm, "end": v(-57.15, -24.97) * mm});
            skLineSegment(sketch, "E41.6.4.0", {"start": v(-57.15, -19.57) * mm, "end": v(-73.03, -12.8) * mm});
            skLineSegment(sketch, "E41.6.4.1", {"start": v(-41.28, -12.8) * mm, "end": v(-57.15, -19.57) * mm});
            skLineSegment(sketch, "E41.6.4.2", {"start": v(-57.15, -6.04) * mm, "end": v(-41.28, -12.8) * mm});
            skLineSegment(sketch, "E41.6.4.3", {"start": v(-73.03, -12.8) * mm, "end": v(-57.15, -6.04) * mm});
            skLineSegment(sketch, "E41.6.5.0", {"start": v(-57.15, -0.65) * mm, "end": v(-73.03, 6.12) * mm});
            skLineSegment(sketch, "E41.6.5.1", {"start": v(-41.28, 6.12) * mm, "end": v(-57.15, -0.65) * mm});
            skLineSegment(sketch, "E41.6.5.2", {"start": v(-57.15, 12.88) * mm, "end": v(-41.28, 6.12) * mm});
            skLineSegment(sketch, "E41.6.5.3", {"start": v(-73.03, 6.12) * mm, "end": v(-57.15, 12.88) * mm});
            skLineSegment(sketch, "E41.7.0.0", {"start": v(-95.25, -95.26) * mm, "end": v(-111.13, -88.5) * mm});
            skLineSegment(sketch, "E41.7.0.1", {"start": v(-79.38, -88.5) * mm, "end": v(-95.25, -95.26) * mm});
            skLineSegment(sketch, "E41.7.0.2", {"start": v(-95.25, -81.73) * mm, "end": v(-79.38, -88.5) * mm});
            skLineSegment(sketch, "E41.7.0.3", {"start": v(-111.13, -88.5) * mm, "end": v(-95.25, -81.73) * mm});
            skLineSegment(sketch, "E41.7.1.0", {"start": v(-95.25, -76.34) * mm, "end": v(-111.13, -69.57) * mm});
            skLineSegment(sketch, "E41.7.1.1", {"start": v(-79.38, -69.57) * mm, "end": v(-95.25, -76.34) * mm});
            skLineSegment(sketch, "E41.7.1.2", {"start": v(-95.25, -62.81) * mm, "end": v(-79.38, -69.57) * mm});
            skLineSegment(sketch, "E41.7.1.3", {"start": v(-111.13, -69.57) * mm, "end": v(-95.25, -62.81) * mm});
            skLineSegment(sketch, "E41.7.2.0", {"start": v(-95.25, -57.41) * mm, "end": v(-111.13, -50.65) * mm});
            skLineSegment(sketch, "E41.7.2.1", {"start": v(-79.38, -50.65) * mm, "end": v(-95.25, -57.41) * mm});
            skLineSegment(sketch, "E41.7.2.2", {"start": v(-95.25, -43.89) * mm, "end": v(-79.38, -50.65) * mm});
            skLineSegment(sketch, "E41.7.2.3", {"start": v(-111.13, -50.65) * mm, "end": v(-95.25, -43.89) * mm});
            skLineSegment(sketch, "E41.7.3.0", {"start": v(-95.25, -38.5) * mm, "end": v(-111.13, -31.73) * mm});
            skLineSegment(sketch, "E41.7.3.1", {"start": v(-79.38, -31.73) * mm, "end": v(-95.25, -38.5) * mm});
            skLineSegment(sketch, "E41.7.3.2", {"start": v(-95.25, -24.97) * mm, "end": v(-79.38, -31.73) * mm});
            skLineSegment(sketch, "E41.7.3.3", {"start": v(-111.13, -31.73) * mm, "end": v(-95.25, -24.97) * mm});
            skLineSegment(sketch, "E41.7.4.0", {"start": v(-95.25, -19.57) * mm, "end": v(-111.13, -12.8) * mm});
            skLineSegment(sketch, "E41.7.4.1", {"start": v(-79.38, -12.8) * mm, "end": v(-95.25, -19.57) * mm});
            skLineSegment(sketch, "E41.7.4.2", {"start": v(-95.25, -6.04) * mm, "end": v(-79.38, -12.8) * mm});
            skLineSegment(sketch, "E41.7.4.3", {"start": v(-111.13, -12.8) * mm, "end": v(-95.25, -6.04) * mm});
            skLineSegment(sketch, "E41.7.5.0", {"start": v(-95.25, -0.65) * mm, "end": v(-111.13, 6.12) * mm});
            skLineSegment(sketch, "E41.7.5.1", {"start": v(-79.38, 6.12) * mm, "end": v(-95.25, -0.65) * mm});
            skLineSegment(sketch, "E41.7.5.2", {"start": v(-95.25, 12.88) * mm, "end": v(-79.38, 6.12) * mm});
            skLineSegment(sketch, "E41.7.5.3", {"start": v(-111.13, 6.12) * mm, "end": v(-95.25, 12.88) * mm});
            skLineSegment(sketch, "E41.8.0.0", {"start": v(-133.35, -95.26) * mm, "end": v(-149.23, -88.5) * mm});
            skLineSegment(sketch, "E41.8.0.1", {"start": v(-117.48, -88.5) * mm, "end": v(-133.35, -95.26) * mm});
            skLineSegment(sketch, "E41.8.0.2", {"start": v(-133.35, -81.73) * mm, "end": v(-117.48, -88.5) * mm});
            skLineSegment(sketch, "E41.8.0.3", {"start": v(-149.23, -88.5) * mm, "end": v(-133.35, -81.73) * mm});
            skLineSegment(sketch, "E41.8.1.0", {"start": v(-133.35, -76.34) * mm, "end": v(-149.23, -69.57) * mm});
            skLineSegment(sketch, "E41.8.1.1", {"start": v(-117.48, -69.57) * mm, "end": v(-133.35, -76.34) * mm});
            skLineSegment(sketch, "E41.8.1.2", {"start": v(-133.35, -62.81) * mm, "end": v(-117.48, -69.57) * mm});
            skLineSegment(sketch, "E41.8.1.3", {"start": v(-149.23, -69.57) * mm, "end": v(-133.35, -62.81) * mm});
            skLineSegment(sketch, "E41.8.2.0", {"start": v(-133.35, -57.41) * mm, "end": v(-149.23, -50.65) * mm});
            skLineSegment(sketch, "E41.8.2.1", {"start": v(-117.48, -50.65) * mm, "end": v(-133.35, -57.41) * mm});
            skLineSegment(sketch, "E41.8.2.2", {"start": v(-133.35, -43.89) * mm, "end": v(-117.48, -50.65) * mm});
            skLineSegment(sketch, "E41.8.2.3", {"start": v(-149.23, -50.65) * mm, "end": v(-133.35, -43.89) * mm});
            skLineSegment(sketch, "E41.8.3.0", {"start": v(-133.35, -38.5) * mm, "end": v(-149.23, -31.73) * mm});
            skLineSegment(sketch, "E41.8.3.1", {"start": v(-117.48, -31.73) * mm, "end": v(-133.35, -38.5) * mm});
            skLineSegment(sketch, "E41.8.3.2", {"start": v(-133.35, -24.97) * mm, "end": v(-117.48, -31.73) * mm});
            skLineSegment(sketch, "E41.8.3.3", {"start": v(-149.23, -31.73) * mm, "end": v(-133.35, -24.97) * mm});
            skLineSegment(sketch, "E41.8.4.0", {"start": v(-133.35, -19.57) * mm, "end": v(-149.23, -12.8) * mm});
            skLineSegment(sketch, "E41.8.4.1", {"start": v(-117.48, -12.8) * mm, "end": v(-133.35, -19.57) * mm});
            skLineSegment(sketch, "E41.8.4.2", {"start": v(-133.35, -6.04) * mm, "end": v(-117.48, -12.8) * mm});
            skLineSegment(sketch, "E41.8.4.3", {"start": v(-149.23, -12.8) * mm, "end": v(-133.35, -6.04) * mm});
            skLineSegment(sketch, "E41.8.5.0", {"start": v(-133.35, -0.65) * mm, "end": v(-149.23, 6.12) * mm});
            skLineSegment(sketch, "E41.8.5.1", {"start": v(-117.48, 6.12) * mm, "end": v(-133.35, -0.65) * mm});
            skLineSegment(sketch, "E41.8.5.2", {"start": v(-133.35, 12.88) * mm, "end": v(-117.48, 6.12) * mm});
            skLineSegment(sketch, "E41.8.5.3", {"start": v(-149.23, 6.12) * mm, "end": v(-133.35, 12.88) * mm});
            skLineSegment(sketch, "E41.9.0.0", {"start": v(-171.45, -95.26) * mm, "end": v(-187.33, -88.5) * mm});
            skLineSegment(sketch, "E41.9.0.1", {"start": v(-155.58, -88.5) * mm, "end": v(-171.45, -95.26) * mm});
            skLineSegment(sketch, "E41.9.0.2", {"start": v(-171.45, -81.73) * mm, "end": v(-155.58, -88.5) * mm});
            skLineSegment(sketch, "E41.9.0.3", {"start": v(-187.33, -88.5) * mm, "end": v(-171.45, -81.73) * mm});
            skLineSegment(sketch, "E41.9.1.0", {"start": v(-171.45, -76.34) * mm, "end": v(-187.33, -69.57) * mm});
            skLineSegment(sketch, "E41.9.1.1", {"start": v(-155.58, -69.57) * mm, "end": v(-171.45, -76.34) * mm});
            skLineSegment(sketch, "E41.9.1.2", {"start": v(-171.45, -62.81) * mm, "end": v(-155.58, -69.57) * mm});
            skLineSegment(sketch, "E41.9.1.3", {"start": v(-187.33, -69.57) * mm, "end": v(-171.45, -62.81) * mm});
            skLineSegment(sketch, "E41.9.2.0", {"start": v(-171.45, -57.41) * mm, "end": v(-187.33, -50.65) * mm});
            skLineSegment(sketch, "E41.9.2.1", {"start": v(-155.58, -50.65) * mm, "end": v(-171.45, -57.41) * mm});
            skLineSegment(sketch, "E41.9.2.2", {"start": v(-171.45, -43.89) * mm, "end": v(-155.58, -50.65) * mm});
            skLineSegment(sketch, "E41.9.2.3", {"start": v(-187.33, -50.65) * mm, "end": v(-171.45, -43.89) * mm});
            skLineSegment(sketch, "E41.9.3.0", {"start": v(-171.45, -38.5) * mm, "end": v(-187.33, -31.73) * mm});
            skLineSegment(sketch, "E41.9.3.1", {"start": v(-155.58, -31.73) * mm, "end": v(-171.45, -38.5) * mm});
            skLineSegment(sketch, "E41.9.3.2", {"start": v(-171.45, -24.97) * mm, "end": v(-155.58, -31.73) * mm});
            skLineSegment(sketch, "E41.9.3.3", {"start": v(-187.33, -31.73) * mm, "end": v(-171.45, -24.97) * mm});
            skLineSegment(sketch, "E41.9.4.0", {"start": v(-171.45, -19.57) * mm, "end": v(-187.33, -12.8) * mm});
            skLineSegment(sketch, "E41.9.4.1", {"start": v(-155.58, -12.8) * mm, "end": v(-171.45, -19.57) * mm});
            skLineSegment(sketch, "E41.9.4.2", {"start": v(-171.45, -6.04) * mm, "end": v(-155.58, -12.8) * mm});
            skLineSegment(sketch, "E41.9.4.3", {"start": v(-187.33, -12.8) * mm, "end": v(-171.45, -6.04) * mm});
            skLineSegment(sketch, "E41.9.5.0", {"start": v(-171.45, -0.65) * mm, "end": v(-187.33, 6.12) * mm});
            skLineSegment(sketch, "E41.9.5.1", {"start": v(-155.58, 6.12) * mm, "end": v(-171.45, -0.65) * mm});
            skLineSegment(sketch, "E41.9.5.2", {"start": v(-171.45, 12.88) * mm, "end": v(-155.58, 6.12) * mm});
            skLineSegment(sketch, "E41.9.5.3", {"start": v(-187.33, 6.12) * mm, "end": v(-171.45, 12.88) * mm});
            skLineSegment(sketch, "E41.direction1", {"start": v(155.57, -88.5) * mm, "end": v(117.47, -88.5) * mm, "construction": true});
            skLineSegment(sketch, "E41.direction2", {"start": v(155.57, -88.5) * mm, "end": v(155.57, -69.57) * mm, "construction": true});
            skSolve(sketch);
        }
        {
            var Q0;
            Q0 = qSketchRegion(id + "F8", true);
            extrude(context, id + "F9", {"entities" : qUnion([Q0]), "operationType" : NewBodyOperationType.REMOVE, "oppositeDirection" : true, "depth" : 25.4 * mm});
        }
    });
